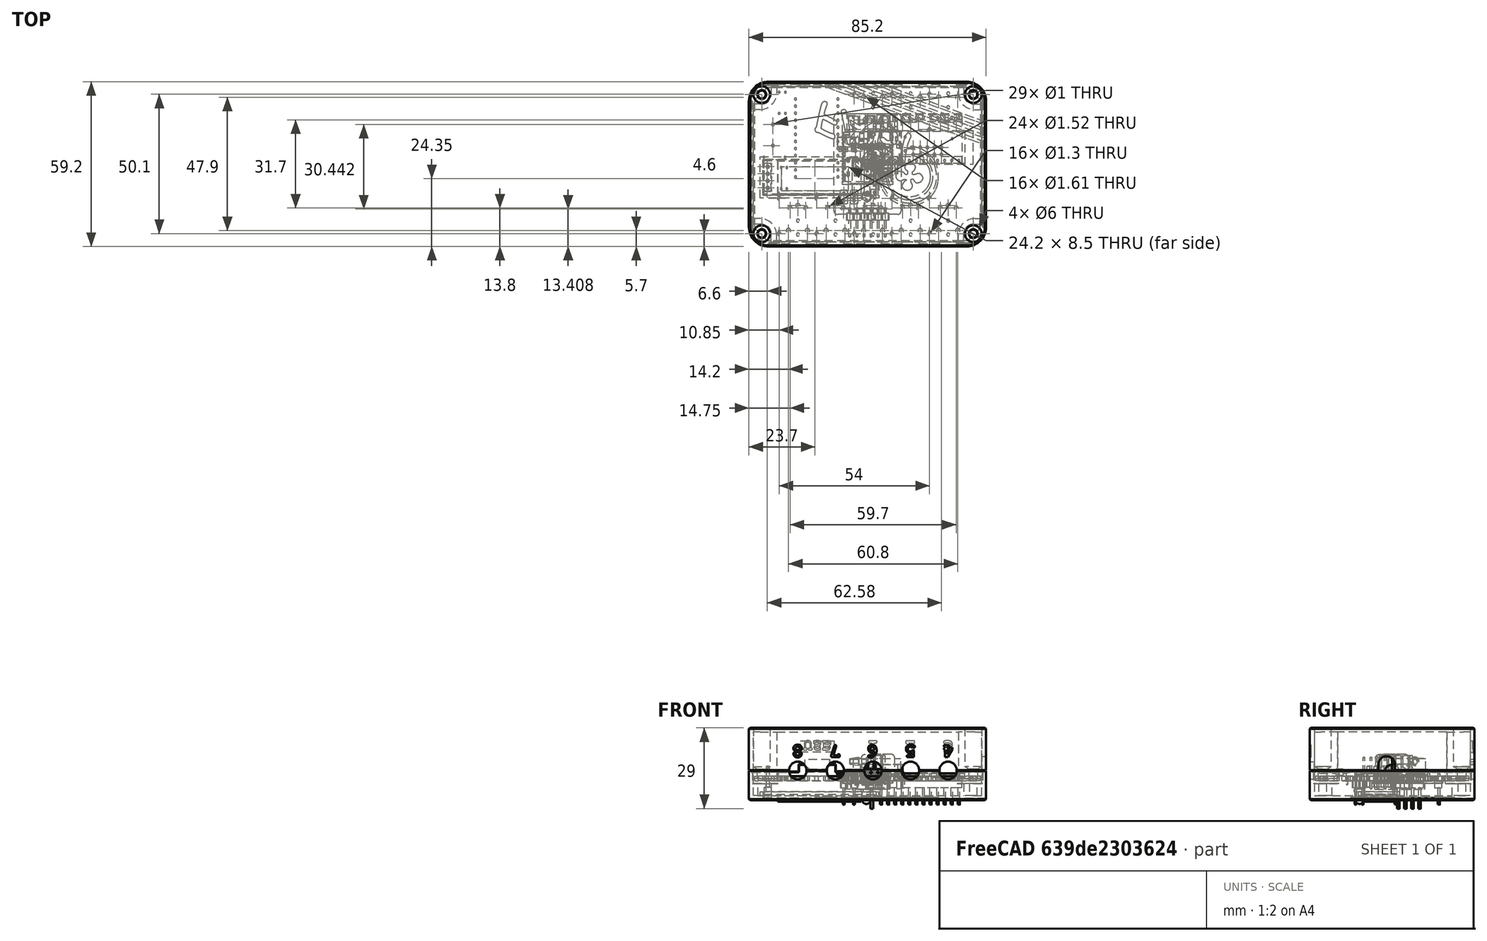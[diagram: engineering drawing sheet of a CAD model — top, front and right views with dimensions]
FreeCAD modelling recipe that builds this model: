
FCSTD DOCUMENT  (FreeCAD 0.18R4 (GitTag))
Label: FABIv3
License: All rights reserved
LicenseURL: http://en.wikipedia.org/wiki/All_rights_reserved
objects: Part::Feature×93, App::Part×90, Sketcher::SketchObject×32, PartDesign::Pocket×25, PartDesign::Mirrored×11, Mesh::Feature×7, PartDesign::Pad×5, PartDesign::MultiTransform×5, PartDesign::Plane×3, Part::Part2DObjectPython×3, PartDesign::Chamfer×2, PartDesign::Body×2, Part::FeaturePython×1, Part::Extrusion×1, PartDesign::Hole×1, PartDesign::LinearPattern×1, Part::Cut×1
note: 217 computed .brp shape members not serialized (recipe doc carries the construction recipe); baked Part::Feature solids carry a one-line shape summary decoded from their .brp

FEATURE [Part::Feature] Part__Feature086  label="SOLID080"
  Placement = pos=(-37.25,1.25,-4.85) rot=(1,0,0;3.14159rad)
  shape: bbox 38 x 12 x 12.6 mm, 32 faces (baked)
FEATURE [Part::Feature] Part__Feature176  label="SOLID162"
  shape: bbox 12.99 x 12.99 x 12.53 mm, 13 faces (baked)
FEATURE [App::Part] Buzzer_12x9_5RM7_6001  label="Buzzer_12x9.5RM7.007"
  Group = -> [Part__Feature176]
  Origin = -> Origin171
  Placement = pos=(-34.008,14.25,1.65) rot=(0,0,-1;1.5708rad)
FEATURE [Part::Feature] Part__Feature177  label="SOLID163"
  shape: bbox 15.1 x 7.1 x 8.8 mm, 33 faces (baked)
FEATURE [App::Part] JackPlug_FC68125031  label="JackPlug_FC68156"
  Group = -> [Part__Feature177]
  Origin = -> Origin172
  Placement = pos=(-1.5,27.4,2.15) rot=(0,0,-1;1.5708rad)
FEATURE [Part::Feature] Part__Feature178  label="SOLID164"
  shape: bbox 15.1 x 7.1 x 8.8 mm, 33 faces (baked)
FEATURE [App::Part] JackPlug_FC68125032  label="JackPlug_FC68157"
  Group = -> [Part__Feature178]
  Origin = -> Origin173
  Placement = pos=(12,27.4,2.15) rot=(0,0,-1;1.5708rad)
FEATURE [Part::Feature] Part__Feature179  label="SOLID165"
  shape: bbox 15.1 x 7.1 x 8.8 mm, 33 faces (baked)
FEATURE [App::Part] JackPlug_FC68125033  label="JackPlug_FC68158"
  Group = -> [Part__Feature179]
  Origin = -> Origin174
  Placement = pos=(25.5,27.4,2.15) rot=(0,0,-1;1.5708rad)
FEATURE [Part::Feature] Part__Feature180  label="SOLID166"
  shape: bbox 15.1 x 7.1 x 8.8 mm, 33 faces (baked)
FEATURE [App::Part] JackPlug_FC68125034  label="JackPlug_FC68159"
  Group = -> [Part__Feature180]
  Origin = -> Origin175
  Placement = pos=(32.5,-27.3,2.15) rot=(0,0,1;1.5708rad)
FEATURE [Part::Feature] Part__Feature181  label="SOLID167"
  shape: bbox 14.07 x 5.32 x 8.31 mm, 15 faces (baked)
FEATURE [App::Part] D_DO_201AE_P12_70mm_Horizontal031  label="D_DO-201AE_P12.70mm_Horizontal031"
  Group = -> [Part__Feature181]
  Origin = -> Origin176
  Placement = pos=(-4.75,25.1,1.65) rot=(0,0,-1;1.5708rad)
FEATURE [Part::Feature] Part__Feature182  label="SOLID168"
  shape: bbox 14.07 x 5.32 x 8.31 mm, 15 faces (baked)
FEATURE [App::Part] D_DO_201AE_P12_70mm_Horizontal032  label="D_DO-201AE_P12.70mm_Horizontal032"
  Group = -> [Part__Feature182]
  Origin = -> Origin177
  Placement = pos=(8.75,25.1,1.65) rot=(0,0,-1;1.5708rad)
FEATURE [Part::Feature] Part__Feature183  label="SOLID169"
  shape: bbox 14.07 x 5.32 x 8.31 mm, 15 faces (baked)
FEATURE [App::Part] D_DO_201AE_P12_70mm_Horizontal033  label="D_DO-201AE_P12.70mm_Horizontal033"
  Group = -> [Part__Feature183]
  Origin = -> Origin178
  Placement = pos=(22.25,25.1,1.65) rot=(0,0,-1;1.5708rad)
FEATURE [Part::Feature] Part__Feature184  label="SOLID170"
  shape: bbox 14.07 x 5.32 x 8.31 mm, 15 faces (baked)
FEATURE [App::Part] D_DO_201AE_P12_70mm_Horizontal034  label="D_DO-201AE_P12.70mm_Horizontal034"
  Group = -> [Part__Feature184]
  Origin = -> Origin179
  Placement = pos=(22.25,-25,1.65) rot=(0,0,1;1.5708rad)
FEATURE [Part::Feature] Part__Feature185  label="SOLID171"
  shape: bbox 15.1 x 7.1 x 8.8 mm, 33 faces (baked)
FEATURE [App::Part] JackPlug_FC68125035  label="JackPlug_FC68160"
  Group = -> [Part__Feature185]
  Origin = -> Origin180
  Placement = pos=(19,-27.3,2.15) rot=(0,0,1;1.5708rad)
FEATURE [Part::Feature] Part__Feature186  label="SOLID172"
  shape: bbox 15.1 x 7.1 x 8.8 mm, 33 faces (baked)
FEATURE [App::Part] JackPlug_FC68125036  label="JackPlug_FC68161"
  Group = -> [Part__Feature186]
  Origin = -> Origin181
  Placement = pos=(5.5,-27.3,2.15) rot=(0,0,1;1.5708rad)
FEATURE [Part::Feature] Part__Feature187  label="SOLID173"
  shape: bbox 15.1 x 7.1 x 8.8 mm, 33 faces (baked)
FEATURE [App::Part] JackPlug_FC68125037  label="JackPlug_FC68162"
  Group = -> [Part__Feature187]
  Origin = -> Origin182
  Placement = pos=(-8,-27.3,2.15) rot=(0,0,1;1.5708rad)
FEATURE [Part::Feature] Part__Feature188  label="SOLID174"
  shape: bbox 14.07 x 5.32 x 8.31 mm, 15 faces (baked)
FEATURE [App::Part] D_DO_201AE_P12_70mm_Horizontal035  label="D_DO-201AE_P12.70mm_Horizontal035"
  Group = -> [Part__Feature188]
  Origin = -> Origin183
  Placement = pos=(8.75,-25,1.65) rot=(0,0,1;1.5708rad)
FEATURE [Part::Feature] Part__Feature189  label="SOLID175"
  shape: bbox 14.07 x 5.32 x 8.31 mm, 15 faces (baked)
FEATURE [App::Part] D_DO_201AE_P12_70mm_Horizontal036  label="D_DO-201AE_P12.70mm_Horizontal036"
  Group = -> [Part__Feature189]
  Origin = -> Origin184
  Placement = pos=(-4.75,-25,1.65) rot=(0,0,1;1.5708rad)
FEATURE [Part::Feature] Part__Feature190  label="SOLID176"
  shape: bbox 14.07 x 5.32 x 8.31 mm, 15 faces (baked)
FEATURE [App::Part] D_DO_201AE_P12_70mm_Horizontal037  label="D_DO-201AE_P12.70mm_Horizontal037"
  Group = -> [Part__Feature190]
  Origin = -> Origin185
  Placement = pos=(-18.25,-25,1.65) rot=(0,0,1;1.5708rad)
FEATURE [Part::Feature] Part__Feature191  label="SOLID177"
  shape: bbox 15.1 x 7.1 x 8.8 mm, 33 faces (baked)
FEATURE [App::Part] JackPlug_FC68125038  label="JackPlug_FC68163"
  Group = -> [Part__Feature191]
  Origin = -> Origin186
  Placement = pos=(-21.5,-27.3,2.15) rot=(0,0,1;1.5708rad)
FEATURE [Part::Feature] Part__Feature192  label="SOLID178"
  shape: bbox 8.285 x 1.732 x 4.666 mm, 17 faces (baked)
FEATURE [App::Part] R_Axial_DIN0204_L3_6mm_D1_6mm_P7_62mm_Horizontal028  label="R_Axial_DIN0204_L3.6mm_D1.6mm_P7.62mm_Horizontal028"
  Group = -> [Part__Feature192]
  Origin = -> Origin187
  Placement = pos=(-8.1,-1.4,1.65) rot=(0,0,1;0rad)
FEATURE [Part::Feature] Part__Feature193  label="SOLID179"
  shape: bbox 8.285 x 1.732 x 4.666 mm, 17 faces (baked)
FEATURE [App::Part] R_Axial_DIN0204_L3_6mm_D1_6mm_P7_62mm_Horizontal029  label="R_Axial_DIN0204_L3.6mm_D1.6mm_P7.62mm_Horizontal029"
  Group = -> [Part__Feature193]
  Origin = -> Origin188
  Placement = pos=(-8.1,-4,1.65) rot=(0,0,1;0rad)
FEATURE [Part::Feature] Part__Feature194  label="SOLID180"
  shape: bbox 8.285 x 1.732 x 4.666 mm, 17 faces (baked)
FEATURE [App::Part] R_Axial_DIN0204_L3_6mm_D1_6mm_P7_62mm_Horizontal030  label="R_Axial_DIN0204_L3.6mm_D1.6mm_P7.62mm_Horizontal030"
  Group = -> [Part__Feature194]
  Origin = -> Origin189
  Placement = pos=(30.4,1.5,1.65) rot=(0,0,1;1.5708rad)
FEATURE [Part::Feature] Part__Feature195  label="SOLID181"
  shape: bbox 2 x 1.2 x 0.45 mm, 26 faces (baked)
FEATURE [App::Part] R_0805_2012Metric028
  Group = -> [Part__Feature195]
  Origin = -> Origin190
  Placement = pos=(30.4,5.35,1.65) rot=(0,0,1;1.5708rad)
FEATURE [Part::Feature] Part__Feature196  label="SOLID182"
  shape: bbox 35.2 x 18 x 12.54 mm, 122 faces (baked)
FEATURE [App::Part] ProMicro003
  Group = -> [Part__Feature196]
  Origin = -> Origin191
  Placement = pos=(-27.25,28.25,4.65) rot=(0,0,-1;1.5708rad)
FEATURE [Part::Feature] Part__Feature197  label="SOLID183"
  shape: bbox 2.8 x 2.9 x 1.55 mm, 109 faces (baked)
FEATURE [App::Part] SOT_23_5007  label="SOT-23-012"
  Group = -> [Part__Feature197]
  Origin = -> Origin192
  Placement = pos=(-14.2,-0.7,1.65) rot=(0,0,1;0rad)
FEATURE [Part::Feature] Part__Feature198  label="SOLID184"
  shape: bbox 38 x 12 x 12.6 mm, 32 faces (baked)
FEATURE [App::Part] OLED092_display002
  Group = -> [Part__Feature198]
  Origin = -> Origin193
  Placement = pos=(-37.5,1.25,-2.85) rot=(1,0,0;3.14159rad)
FEATURE [Part::Feature] Part__Feature199  label="COMPOUND013"
  shape: bbox 10.08 x 3.946 x 9.8 mm, 102 faces, 25 solids (baked)
FEATURE [App::Part] _1601_304LF003  label="91601-304LF003"
  Group = -> [Part__Feature199]
  Origin = -> Origin194
  Placement = pos=(-36,-4.75,1.65) rot=(0,0,-1;1.5708rad)
FEATURE [Part::Feature] Part__Feature200  label="SOLID185"
  shape: bbox 18.35 x 12 x 8.506 mm, 25 faces (baked)
FEATURE [Part::Feature] Part__Feature201  label="COMPOUND014"
  shape: bbox 8.62 x 19 x 4 mm, 48 faces, 8 solids (baked)
FEATURE [App::Part] mp003
  Group = -> [Part__Feature200,Part__Feature201]
  Origin = -> Origin195
  Placement = pos=(12.5,6,1.65) rot=(0,0,1;3.14159rad)
FEATURE [Part::Feature] Part__Feature202  label="COMPOUND015"
  shape: bbox 24.13 x 44.38 x 17.54 mm, 1943 faces, 18 solids (baked)
FEATURE [App::Part] esp32miniBT002
  Group = -> [Part__Feature202]
  Origin = -> Origin196
  Placement = pos=(20.52,0.92,14.15) rot=(0.707107,0.707107,0;3.14159rad)
FEATURE [Part::Feature] Part__Feature203  label="SOLID186"
  shape: bbox 2 x 1.2 x 0.45 mm, 26 faces (baked)
FEATURE [App::Part] R_0805_2012Metric029
  Group = -> [Part__Feature203]
  Origin = -> Origin197
  Placement = pos=(-29.5,22,1.65) rot=(0,0,-1;1.5708rad)
FEATURE [Part::Feature] Part__Feature204  label="SOLID187"
  shape: bbox 2 x 1.2 x 0.45 mm, 26 faces (baked)
FEATURE [App::Part] R_0805_2012Metric030
  Group = -> [Part__Feature204]
  Origin = -> Origin198
  Placement = pos=(-31.75,22,1.65) rot=(0,0,1;1.5708rad)
FEATURE [Part::Feature] Part__Feature205  label="SOLID188"
  shape: bbox 8.285 x 1.732 x 4.666 mm, 17 faces (baked)
FEATURE [App::Part] R_Axial_DIN0204_L3_6mm_D1_6mm_P7_62mm_Horizontal031  label="R_Axial_DIN0204_L3.6mm_D1.6mm_P7.62mm_Horizontal031"
  Group = -> [Part__Feature205]
  Origin = -> Origin199
  Placement = pos=(-31,-1.25,1.65) rot=(0,0,-1;1.5708rad)
FEATURE [Part::Feature] Part__Feature206  label="SOLID189"
  shape: bbox 5.08 x 12.7 x 11.54 mm, 214 faces (baked)
FEATURE [App::Part] PinHeader_2x05_P2_54mm_Vertical003  label="PinHeader_2x05_P2.54mm_Vertical003"
  Group = -> [Part__Feature206]
  Origin = -> Origin200
  Placement = pos=(16.42,3.46,1.65) rot=(0,0,1;1.5708rad)
FEATURE [Part::Feature] Part__Feature207  label="SOLID190"
  shape: bbox 2.54 x 7.62 x 11.54 mm, 76 faces (baked)
FEATURE [App::Part] PinHeader_1x03_P2_54mm_Vertical003  label="PinHeader_1x03_P2.54mm_Vertical003"
  Group = -> [Part__Feature207]
  Origin = -> Origin201
  Placement = pos=(-4.3,7.3,1.65) rot=(0,0,1;0rad)
FEATURE [Part::Feature] Part__Feature208  label="SOLID191"
  shape: bbox 8.285 x 1.732 x 4.666 mm, 17 faces (baked)
FEATURE [App::Part] R_Axial_DIN0204_L3_6mm_D1_6mm_P7_62mm_Horizontal032  label="R_Axial_DIN0204_L3.6mm_D1.6mm_P7.62mm_Horizontal032"
  Group = -> [Part__Feature208]
  Origin = -> Origin202
  Placement = pos=(-29,-1.25,1.65) rot=(0,0,-1;1.5708rad)
FEATURE [Part::Feature] Part__Feature209  label="SOLID192"
  shape: bbox 2 x 1.2 x 0.45 mm, 26 faces (baked)
FEATURE [App::Part] R_0805_2012Metric031
  Group = -> [Part__Feature209]
  Origin = -> Origin203
  Placement = pos=(-4.3,-4,1.65) rot=(0,0,1;0rad)
FEATURE [Part::Feature] Part__Feature210  label="SOLID193"
  shape: bbox 2 x 1.2 x 0.45 mm, 26 faces (baked)
FEATURE [App::Part] R_0805_2012Metric032
  Group = -> [Part__Feature210]
  Origin = -> Origin204
  Placement = pos=(-4.3,-1.4,1.65) rot=(0,0,1;0rad)
FEATURE [Part::Feature] Part__Feature211  label="SOLID194"
  shape: bbox 2 x 1.2 x 0.45 mm, 26 faces (baked)
FEATURE [App::Part] R_0805_2012Metric033
  Group = -> [Part__Feature211]
  Origin = -> Origin205
  Placement = pos=(-33.5,2.5,1.65) rot=(0,0,1;0rad)
FEATURE [Part::Feature] Part__Feature212  label="SOLID195"
  shape: bbox 2 x 1.2 x 0.45 mm, 26 faces (baked)
FEATURE [App::Part] R_0805_2012Metric034
  Group = -> [Part__Feature212]
  Origin = -> Origin206
  Placement = pos=(-30,-6,1.65) rot=(0,0,1;0rad)
FEATURE [Part::Feature] Part__Feature213  label="SOLID196"
  shape: bbox 2 x 1.2 x 0.45 mm, 26 faces (baked)
FEATURE [App::Part] R_0805_2012Metric035
  Group = -> [Part__Feature213]
  Origin = -> Origin207
  Placement = pos=(-30,-4,1.65) rot=(0,0,1;0rad)
FEATURE [Part::Feature] Part__Feature214  label="SOLID197"
  shape: bbox 2 x 1.25 x 1.25 mm, 28 faces (baked)
FEATURE [App::Part] C_0805_2012Metric003
  Group = -> [Part__Feature214]
  Origin = -> Origin208
  Placement = pos=(6,10.7,1.65) rot=(0,0,1;3.14159rad)
FEATURE [Part::Feature] Part__Feature215  label="SOLID198"
  shape: bbox 5.5 x 2.5 x 7.1 mm, 10 faces (baked)
FEATURE [App::Part] C_Disc_D5_0mm_W2_5mm_P5_00mm003  label="C_Disc_D5.0mm_W2.5mm_P5.00mm003"
  Group = -> [Part__Feature215]
  Origin = -> Origin209
  Placement = pos=(13.5,9.75,1.65) rot=(0,0,-1;1.5708rad)
FEATURE [Part::Feature] Part__Feature216  label="SOLID199"
  shape: bbox 14.07 x 5.32 x 8.31 mm, 15 faces (baked)
FEATURE [App::Part] D_DO_201AE_P12_70mm_Horizontal038  label="D_DO-201AE_P12.70mm_Horizontal038"
  Group = -> [Part__Feature216]
  Origin = -> Origin210
  Placement = pos=(-31.75,-25,1.65) rot=(0,0,1;1.5708rad)
FEATURE [Part::Feature] Part__Feature217  label="SOLID200"
  shape: bbox 8.285 x 1.732 x 4.666 mm, 17 faces (baked)
FEATURE [App::Part] R_Axial_DIN0204_L3_6mm_D1_6mm_P7_62mm_Horizontal033  label="R_Axial_DIN0204_L3.6mm_D1.6mm_P7.62mm_Horizontal033"
  Group = -> [Part__Feature217]
  Origin = -> Origin211
  Placement = pos=(-37.25,2.5,1.65) rot=(0,0,1;0rad)
FEATURE [Part::Feature] Part__Feature218  label="SOLID201"
  shape: bbox 8.285 x 1.732 x 4.666 mm, 17 faces (baked)
FEATURE [App::Part] R_Axial_DIN0204_L3_6mm_D1_6mm_P7_62mm_Horizontal034  label="R_Axial_DIN0204_L3.6mm_D1.6mm_P7.62mm_Horizontal034"
  Group = -> [Part__Feature218]
  Origin = -> Origin212
  Placement = pos=(-29.5,25.87,1.65) rot=(0,0,-1;1.5708rad)
FEATURE [Part::Feature] Part__Feature219  label="SOLID202"
  shape: bbox 8.285 x 1.732 x 4.666 mm, 17 faces (baked)
FEATURE [App::Part] R_Axial_DIN0204_L3_6mm_D1_6mm_P7_62mm_Horizontal035  label="R_Axial_DIN0204_L3.6mm_D1.6mm_P7.62mm_Horizontal035"
  Group = -> [Part__Feature219]
  Origin = -> Origin213
  Placement = pos=(-31.75,18.25,1.65) rot=(0,0,1;1.5708rad)
FEATURE [Part::Feature] Part__Feature220  label="SOLID203"
  shape: bbox 2.8 x 2.9 x 1.55 mm, 109 faces (baked)
FEATURE [App::Part] SOT_23_5008  label="SOT-23-013"
  Group = -> [Part__Feature220]
  Origin = -> Origin214
  Placement = pos=(-19.5,-8.7,1.65) rot=(0,0,1;1.5708rad)
FEATURE [Part::Feature] Part__Feature221  label="COMPOUND016"
  shape: bbox 81 x 55 x 1.6 mm, 174 faces (baked)
FEATURE [App::Part] Open_CASCADE_STEP_translator_6_9_1003  label="FABI_PCB001"
  Group = -> [Buzzer_12x9_5RM7_6001,JackPlug_FC68125031,JackPlug_FC68125032,JackPlug_FC68125033,JackPlug_FC68125034,D_DO_201AE_P12_70mm_Horizontal031,D_DO_201AE_P12_70mm_Horizontal032,D_DO_201AE_P12_70mm_Horizontal033,D_DO_201AE_P12_70mm_Horizontal034,JackPlug_FC68125035,JackPlug_FC68125036,JackPlug_FC68125037,D_DO_201AE_P12_70mm_Horizontal035,D_DO_201AE_P12_70mm_Horizontal036,D_DO_201AE_P12_70mm_Horizontal037,+30 more]
  Origin = -> Origin215
  Placement = pos=(0,0,-1.6) rot=(0,0,1;0rad)
FEATURE [Part::Feature] Part__Feature222  label="SOLID204"
  shape: bbox 12.99 x 12.99 x 12.53 mm, 13 faces (baked)
FEATURE [App::Part] Buzzer_12x9_5RM7_6002  label="Buzzer_12x9.5RM7.008"
  Group = -> [Part__Feature222]
  Origin = -> Origin216
  Placement = pos=(-34.008,14.25,1.65) rot=(0,0,-1;1.5708rad)
FEATURE [Part::Feature] Part__Feature223  label="SOLID205"
  shape: bbox 15.1 x 7.1 x 8.8 mm, 33 faces (baked)
FEATURE [App::Part] JackPlug_FC68125039  label="JackPlug_FC68164"
  Group = -> [Part__Feature223]
  Origin = -> Origin217
  Placement = pos=(-1.55,27.4,2.15) rot=(0,0,-1;1.5708rad)
FEATURE [Part::Feature] Part__Feature224  label="SOLID206"
  shape: bbox 15.1 x 7.1 x 8.8 mm, 33 faces (baked)
FEATURE [App::Part] JackPlug_FC68125040  label="JackPlug_FC68165"
  Group = -> [Part__Feature224]
  Origin = -> Origin218
  Placement = pos=(11.95,27.4,2.15) rot=(0,0,-1;1.5708rad)
FEATURE [Part::Feature] Part__Feature225  label="SOLID207"
  shape: bbox 15.1 x 7.1 x 8.8 mm, 33 faces (baked)
FEATURE [App::Part] JackPlug_FC68125041  label="JackPlug_FC68166"
  Group = -> [Part__Feature225]
  Origin = -> Origin219
  Placement = pos=(25.45,27.4,2.15) rot=(0,0,-1;1.5708rad)
FEATURE [Part::Feature] Part__Feature226  label="SOLID208"
  shape: bbox 15.1 x 7.1 x 8.8 mm, 33 faces (baked)
FEATURE [App::Part] JackPlug_FC68125042  label="JackPlug_FC68167"
  Group = -> [Part__Feature226]
  Origin = -> Origin220
  Placement = pos=(32.55,-27.3,2.15) rot=(0,0,1;1.5708rad)
FEATURE [Part::Feature] Part__Feature227  label="SOLID209"
  shape: bbox 14.07 x 5.32 x 8.31 mm, 15 faces (baked)
FEATURE [App::Part] D_DO_201AE_P12_70mm_Horizontal039  label="D_DO-201AE_P12.70mm_Horizontal039"
  Group = -> [Part__Feature227]
  Origin = -> Origin221
  Placement = pos=(-4.75,25.1,1.65) rot=(0,0,-1;1.5708rad)
FEATURE [Part::Feature] Part__Feature228  label="SOLID210"
  shape: bbox 14.07 x 5.32 x 8.31 mm, 15 faces (baked)
FEATURE [App::Part] D_DO_201AE_P12_70mm_Horizontal040  label="D_DO-201AE_P12.70mm_Horizontal040"
  Group = -> [Part__Feature228]
  Origin = -> Origin222
  Placement = pos=(8.75,25.1,1.65) rot=(0,0,-1;1.5708rad)
FEATURE [Part::Feature] Part__Feature229  label="SOLID211"
  shape: bbox 14.07 x 5.32 x 8.31 mm, 15 faces (baked)
FEATURE [App::Part] D_DO_201AE_P12_70mm_Horizontal041  label="D_DO-201AE_P12.70mm_Horizontal041"
  Group = -> [Part__Feature229]
  Origin = -> Origin223
  Placement = pos=(22.25,25.1,1.65) rot=(0,0,-1;1.5708rad)
FEATURE [Part::Feature] Part__Feature230  label="SOLID212"
  shape: bbox 14.07 x 5.32 x 8.31 mm, 15 faces (baked)
FEATURE [App::Part] D_DO_201AE_P12_70mm_Horizontal042  label="D_DO-201AE_P12.70mm_Horizontal042"
  Group = -> [Part__Feature230]
  Origin = -> Origin224
  Placement = pos=(22.25,-25,1.65) rot=(0,0,1;1.5708rad)
FEATURE [Part::Feature] Part__Feature231  label="SOLID213"
  shape: bbox 15.1 x 7.1 x 8.8 mm, 33 faces (baked)
FEATURE [App::Part] JackPlug_FC68125043  label="JackPlug_FC68168"
  Group = -> [Part__Feature231]
  Origin = -> Origin225
  Placement = pos=(19.05,-27.3,2.15) rot=(0,0,1;1.5708rad)
FEATURE [Part::Feature] Part__Feature232  label="SOLID214"
  shape: bbox 15.1 x 7.1 x 8.8 mm, 33 faces (baked)
FEATURE [App::Part] JackPlug_FC68125044  label="JackPlug_FC68169"
  Group = -> [Part__Feature232]
  Origin = -> Origin226
  Placement = pos=(5.55,-27.3,2.15) rot=(0,0,1;1.5708rad)
FEATURE [Part::Feature] Part__Feature233  label="SOLID215"
  shape: bbox 15.1 x 7.1 x 8.8 mm, 33 faces (baked)
FEATURE [App::Part] JackPlug_FC68125045  label="JackPlug_FC68170"
  Group = -> [Part__Feature233]
  Origin = -> Origin227
  Placement = pos=(-7.95,-27.3,2.15) rot=(0,0,1;1.5708rad)
FEATURE [Part::Feature] Part__Feature234  label="SOLID216"
  shape: bbox 14.07 x 5.32 x 8.31 mm, 15 faces (baked)
FEATURE [App::Part] D_DO_201AE_P12_70mm_Horizontal043  label="D_DO-201AE_P12.70mm_Horizontal043"
  Group = -> [Part__Feature234]
  Origin = -> Origin228
  Placement = pos=(8.75,-25,1.65) rot=(0,0,1;1.5708rad)
FEATURE [Part::Feature] Part__Feature235  label="SOLID217"
  shape: bbox 14.07 x 5.32 x 8.31 mm, 15 faces (baked)
FEATURE [App::Part] D_DO_201AE_P12_70mm_Horizontal044  label="D_DO-201AE_P12.70mm_Horizontal044"
  Group = -> [Part__Feature235]
  Origin = -> Origin229
  Placement = pos=(-4.75,-25,1.65) rot=(0,0,1;1.5708rad)
FEATURE [Part::Feature] Part__Feature236  label="SOLID218"
  shape: bbox 14.07 x 5.32 x 8.31 mm, 15 faces (baked)
FEATURE [App::Part] D_DO_201AE_P12_70mm_Horizontal045  label="D_DO-201AE_P12.70mm_Horizontal045"
  Group = -> [Part__Feature236]
  Origin = -> Origin230
  Placement = pos=(-18.25,-25,1.65) rot=(0,0,1;1.5708rad)
FEATURE [Part::Feature] Part__Feature237  label="SOLID219"
  shape: bbox 15.1 x 7.1 x 8.8 mm, 33 faces (baked)
FEATURE [App::Part] JackPlug_FC68125046  label="JackPlug_FC68171"
  Group = -> [Part__Feature237]
  Origin = -> Origin231
  Placement = pos=(-21.45,-27.3,2.15) rot=(0,0,1;1.5708rad)
FEATURE [Part::Feature] Part__Feature238  label="SOLID220"
  shape: bbox 8.285 x 1.732 x 4.666 mm, 17 faces (baked)
FEATURE [App::Part] R_Axial_DIN0204_L3_6mm_D1_6mm_P7_62mm_Horizontal036  label="R_Axial_DIN0204_L3.6mm_D1.6mm_P7.62mm_Horizontal036"
  Group = -> [Part__Feature238]
  Origin = -> Origin232
  Placement = pos=(-8.1,-1.4,1.65) rot=(0,0,1;0rad)
FEATURE [Part::Feature] Part__Feature239  label="SOLID221"
  shape: bbox 8.285 x 1.732 x 4.666 mm, 17 faces (baked)
FEATURE [App::Part] R_Axial_DIN0204_L3_6mm_D1_6mm_P7_62mm_Horizontal037  label="R_Axial_DIN0204_L3.6mm_D1.6mm_P7.62mm_Horizontal037"
  Group = -> [Part__Feature239]
  Origin = -> Origin233
  Placement = pos=(-8.1,-4,1.65) rot=(0,0,1;0rad)
FEATURE [Part::Feature] Part__Feature240  label="SOLID222"
  shape: bbox 8.285 x 1.732 x 4.666 mm, 17 faces (baked)
FEATURE [App::Part] R_Axial_DIN0204_L3_6mm_D1_6mm_P7_62mm_Horizontal038  label="R_Axial_DIN0204_L3.6mm_D1.6mm_P7.62mm_Horizontal038"
  Group = -> [Part__Feature240]
  Origin = -> Origin234
  Placement = pos=(30.4,1.5,1.65) rot=(0,0,1;1.5708rad)
FEATURE [Part::Feature] Part__Feature241  label="SOLID223"
  shape: bbox 2 x 1.2 x 0.45 mm, 26 faces (baked)
FEATURE [App::Part] R_0805_2012Metric036
  Group = -> [Part__Feature241]
  Origin = -> Origin235
  Placement = pos=(30.4,5.35,1.65) rot=(0,0,1;1.5708rad)
FEATURE [Part::Feature] Part__Feature242  label="SOLID224"
  shape: bbox 35.2 x 18 x 12.54 mm, 122 faces (baked)
FEATURE [App::Part] ProMicro004
  Group = -> [Part__Feature242]
  Origin = -> Origin236
  Placement = pos=(-27.25,28.25,4.65) rot=(0,0,-1;1.5708rad)
FEATURE [Part::Feature] Part__Feature243  label="SOLID225"
  shape: bbox 2.8 x 2.9 x 1.55 mm, 109 faces (baked)
FEATURE [App::Part] SOT_23_5009  label="SOT-23-014"
  Group = -> [Part__Feature243]
  Origin = -> Origin237
  Placement = pos=(-14.2,-0.7,1.65) rot=(0,0,1;0rad)
FEATURE [Part::Feature] Part__Feature244  label="SOLID226"
  shape: bbox 38 x 12 x 12.6 mm, 32 faces (baked)
FEATURE [App::Part] OLED092_display003
  Group = -> [Part__Feature244]
  Origin = -> Origin238
  Placement = pos=(-37.5,1.25,-2.85) rot=(1,0,0;3.14159rad)
FEATURE [Part::Feature] Part__Feature245  label="COMPOUND017"
  shape: bbox 10.08 x 3.946 x 9.8 mm, 102 faces, 25 solids (baked)
FEATURE [App::Part] _1601_304LF004  label="91601-304LF004"
  Group = -> [Part__Feature245]
  Origin = -> Origin239
  Placement = pos=(-36,-4.75,1.65) rot=(0,0,-1;1.5708rad)
FEATURE [Part::Feature] Part__Feature246  label="SOLID227"
  shape: bbox 18.35 x 12 x 8.506 mm, 25 faces (baked)
FEATURE [Part::Feature] Part__Feature247  label="COMPOUND018"
  shape: bbox 8.62 x 19 x 4 mm, 48 faces, 8 solids (baked)
FEATURE [App::Part] mp004
  Group = -> [Part__Feature246,Part__Feature247]
  Origin = -> Origin240
  Placement = pos=(12.5,6,1.65) rot=(0,0,1;3.14159rad)
FEATURE [Part::Feature] Part__Feature248  label="COMPOUND019"
  shape: bbox 24.13 x 44.38 x 17.54 mm, 1943 faces, 18 solids (baked)
FEATURE [App::Part] esp32miniBT
  Group = -> [Part__Feature248]
  Origin = -> Origin241
  Placement = pos=(20.52,0.92,14.15) rot=(0.707107,0.707107,0;3.14159rad)
FEATURE [Part::Feature] Part__Feature249  label="SOLID228"
  shape: bbox 2 x 1.2 x 0.45 mm, 26 faces (baked)
FEATURE [App::Part] R_0805_2012Metric037
  Group = -> [Part__Feature249]
  Origin = -> Origin242
  Placement = pos=(-29.5,22,1.65) rot=(0,0,-1;1.5708rad)
FEATURE [Part::Feature] Part__Feature250  label="SOLID229"
  shape: bbox 2 x 1.2 x 0.45 mm, 26 faces (baked)
FEATURE [App::Part] R_0805_2012Metric038
  Group = -> [Part__Feature250]
  Origin = -> Origin243
  Placement = pos=(-31.75,22,1.65) rot=(0,0,1;1.5708rad)
FEATURE [Part::Feature] Part__Feature251  label="SOLID230"
  shape: bbox 8.285 x 1.732 x 4.666 mm, 17 faces (baked)
FEATURE [App::Part] R_Axial_DIN0204_L3_6mm_D1_6mm_P7_62mm_Horizontal039  label="R_Axial_DIN0204_L3.6mm_D1.6mm_P7.62mm_Horizontal039"
  Group = -> [Part__Feature251]
  Origin = -> Origin244
  Placement = pos=(-31,-1.25,1.65) rot=(0,0,-1;1.5708rad)
FEATURE [Part::Feature] Part__Feature252  label="SOLID231"
  shape: bbox 5.08 x 12.7 x 11.54 mm, 214 faces (baked)
FEATURE [App::Part] PinHeader_2x05_P2_54mm_Vertical004  label="PinHeader_2x05_P2.54mm_Vertical004"
  Group = -> [Part__Feature252]
  Origin = -> Origin245
  Placement = pos=(16.42,3.46,1.65) rot=(0,0,1;1.5708rad)
FEATURE [Part::Feature] Part__Feature253  label="SOLID232"
  shape: bbox 2.54 x 7.62 x 11.54 mm, 76 faces (baked)
FEATURE [App::Part] PinHeader_1x03_P2_54mm_Vertical004  label="PinHeader_1x03_P2.54mm_Vertical004"
  Group = -> [Part__Feature253]
  Origin = -> Origin246
  Placement = pos=(-4.3,7.3,1.65) rot=(0,0,1;0rad)
FEATURE [Part::Feature] Part__Feature254  label="SOLID233"
  shape: bbox 8.285 x 1.732 x 4.666 mm, 17 faces (baked)
FEATURE [App::Part] R_Axial_DIN0204_L3_6mm_D1_6mm_P7_62mm_Horizontal040  label="R_Axial_DIN0204_L3.6mm_D1.6mm_P7.62mm_Horizontal040"
  Group = -> [Part__Feature254]
  Origin = -> Origin247
  Placement = pos=(-29,-1.25,1.65) rot=(0,0,-1;1.5708rad)
FEATURE [Part::Feature] Part__Feature255  label="SOLID234"
  shape: bbox 2 x 1.2 x 0.45 mm, 26 faces (baked)
FEATURE [App::Part] R_0805_2012Metric039
  Group = -> [Part__Feature255]
  Origin = -> Origin248
  Placement = pos=(-4.3,-4,1.65) rot=(0,0,1;0rad)
FEATURE [Part::Feature] Part__Feature256  label="SOLID235"
  shape: bbox 2 x 1.2 x 0.45 mm, 26 faces (baked)
FEATURE [App::Part] R_0805_2012Metric040
  Group = -> [Part__Feature256]
  Origin = -> Origin249
  Placement = pos=(-4.3,-1.4,1.65) rot=(0,0,1;0rad)
FEATURE [Part::Feature] Part__Feature257  label="SOLID236"
  shape: bbox 2 x 1.2 x 0.45 mm, 26 faces (baked)
FEATURE [App::Part] R_0805_2012Metric041
  Group = -> [Part__Feature257]
  Origin = -> Origin250
  Placement = pos=(-33.5,2.5,1.65) rot=(0,0,1;0rad)
FEATURE [Part::Feature] Part__Feature258  label="SOLID237"
  shape: bbox 2 x 1.2 x 0.45 mm, 26 faces (baked)
FEATURE [App::Part] R_0805_2012Metric042
  Group = -> [Part__Feature258]
  Origin = -> Origin251
  Placement = pos=(-30,-6,1.65) rot=(0,0,1;0rad)
FEATURE [Part::Feature] Part__Feature259  label="SOLID238"
  shape: bbox 2 x 1.2 x 0.45 mm, 26 faces (baked)
FEATURE [App::Part] R_0805_2012Metric043
  Group = -> [Part__Feature259]
  Origin = -> Origin252
  Placement = pos=(-30,-4,1.65) rot=(0,0,1;0rad)
FEATURE [Part::Feature] Part__Feature260  label="SOLID239"
  shape: bbox 2 x 1.25 x 1.25 mm, 28 faces (baked)
FEATURE [App::Part] C_0805_2012Metric004
  Group = -> [Part__Feature260]
  Origin = -> Origin253
  Placement = pos=(6,10.7,1.65) rot=(0,0,1;3.14159rad)
FEATURE [Part::Feature] Part__Feature261  label="SOLID240"
  shape: bbox 5.5 x 2.5 x 7.1 mm, 10 faces (baked)
FEATURE [App::Part] C_Disc_D5_0mm_W2_5mm_P5_00mm004  label="C_Disc_D5.0mm_W2.5mm_P5.00mm004"
  Group = -> [Part__Feature261]
  Origin = -> Origin254
  Placement = pos=(13.5,9.75,1.65) rot=(0,0,-1;1.5708rad)
FEATURE [Part::Feature] Part__Feature262  label="SOLID241"
  shape: bbox 14.07 x 5.32 x 8.31 mm, 15 faces (baked)
FEATURE [App::Part] D_DO_201AE_P12_70mm_Horizontal046  label="D_DO-201AE_P12.70mm_Horizontal046"
  Group = -> [Part__Feature262]
  Origin = -> Origin255
  Placement = pos=(-31.75,-25,1.65) rot=(0,0,1;1.5708rad)
FEATURE [Part::Feature] Part__Feature263  label="SOLID242"
  shape: bbox 8.285 x 1.732 x 4.666 mm, 17 faces (baked)
FEATURE [App::Part] R_Axial_DIN0204_L3_6mm_D1_6mm_P7_62mm_Horizontal041  label="R_Axial_DIN0204_L3.6mm_D1.6mm_P7.62mm_Horizontal041"
  Group = -> [Part__Feature263]
  Origin = -> Origin256
  Placement = pos=(-37.25,2.5,1.65) rot=(0,0,1;0rad)
FEATURE [Part::Feature] Part__Feature264  label="SOLID243"
  shape: bbox 8.285 x 1.732 x 4.666 mm, 17 faces (baked)
FEATURE [App::Part] R_Axial_DIN0204_L3_6mm_D1_6mm_P7_62mm_Horizontal042  label="R_Axial_DIN0204_L3.6mm_D1.6mm_P7.62mm_Horizontal042"
  Group = -> [Part__Feature264]
  Origin = -> Origin257
  Placement = pos=(-29.5,25.87,1.65) rot=(0,0,-1;1.5708rad)
FEATURE [Part::Feature] Part__Feature265  label="SOLID244"
  shape: bbox 8.285 x 1.732 x 4.666 mm, 17 faces (baked)
FEATURE [App::Part] R_Axial_DIN0204_L3_6mm_D1_6mm_P7_62mm_Horizontal043  label="R_Axial_DIN0204_L3.6mm_D1.6mm_P7.62mm_Horizontal043"
  Group = -> [Part__Feature265]
  Origin = -> Origin258
  Placement = pos=(-31.75,18.25,1.65) rot=(0,0,1;1.5708rad)
FEATURE [Part::Feature] Part__Feature266  label="SOLID245"
  shape: bbox 2.8 x 2.9 x 1.55 mm, 109 faces (baked)
FEATURE [App::Part] SOT_23_5010  label="SOT-23-015"
  Group = -> [Part__Feature266]
  Origin = -> Origin259
  Placement = pos=(-19.5,-8.7,1.65) rot=(0,0,1;1.5708rad)
FEATURE [Part::Feature] Part__Feature267  label="COMPOUND020"
  shape: bbox 81 x 55 x 1.6 mm, 174 faces (baked)
FEATURE [App::Part] Open_CASCADE_STEP_translator_6_9_1004  label="Open CASCADE STEP translator 6.9 002"
  Group = -> [Buzzer_12x9_5RM7_6002,JackPlug_FC68125039,JackPlug_FC68125040,JackPlug_FC68125041,JackPlug_FC68125042,D_DO_201AE_P12_70mm_Horizontal039,D_DO_201AE_P12_70mm_Horizontal040,D_DO_201AE_P12_70mm_Horizontal041,D_DO_201AE_P12_70mm_Horizontal042,JackPlug_FC68125043,JackPlug_FC68125044,JackPlug_FC68125045,D_DO_201AE_P12_70mm_Horizontal043,D_DO_201AE_P12_70mm_Horizontal044,D_DO_201AE_P12_70mm_Horizontal045,+30 more]
  Origin = -> Origin260
  Placement = pos=(0,0,-1.6) rot=(0,0,1;0rad)
FEATURE [Sketcher::SketchObject] CopySketch014  label="Base"
  sketch-geometry (12):
    g0: LineSegment StartX=-35.5 StartY=29.5 StartZ=0 EndX=35.5 EndY=29.5 EndZ=0
    g1: LineSegment StartX=42.5 StartY=22.5 StartZ=0 EndX=42.5 EndY=-22.5 EndZ=0
    g2: LineSegment StartX=35.5 StartY=-29.5 StartZ=0 EndX=-35.5 EndY=-29.5 EndZ=0
    g3: LineSegment [constr] StartX=-40.5 StartY=27.5 StartZ=0 EndX=40.5 EndY=27.5 EndZ=0
    g4: LineSegment [constr] StartX=40.5 StartY=27.5 StartZ=0 EndX=40.5 EndY=-27.5 EndZ=0
    g5: LineSegment [constr] StartX=40.5 StartY=-27.5 StartZ=0 EndX=-40.5 EndY=-27.5 EndZ=0
    g6: LineSegment [constr] StartX=-40.5 StartY=-27.5 StartZ=0 EndX=-40.5 EndY=27.5 EndZ=0
    g7: LineSegment StartX=-42.5 StartY=22.5 StartZ=0 EndX=-42.5 EndY=-22.5 EndZ=0
    g8: ArcOfCircle CenterX=-35.5 CenterY=-22.5 CenterZ=0 NormalX=0 NormalY=0 NormalZ=1 AngleXU=0 Radius=7 StartAngle=3.14159 EndAngle=4.71239
    g9: ArcOfCircle CenterX=35.5 CenterY=-22.5 CenterZ=0 NormalX=0 NormalY=0 NormalZ=1 AngleXU=0 Radius=7 StartAngle=4.71239 EndAngle=6.28319
    g10: ArcOfCircle CenterX=35.5 CenterY=22.5 CenterZ=0 NormalX=0 NormalY=0 NormalZ=1 AngleXU=0 Radius=7 StartAngle=0 EndAngle=1.5708
    g11: ArcOfCircle CenterX=-35.5 CenterY=22.5 CenterZ=0 NormalX=0 NormalY=0 NormalZ=1 AngleXU=0 Radius=7 StartAngle=1.5708 EndAngle=3.14159
  constraints (39):
    c: Coincident(g5,g6)
    c: Coincident(g3,g6)
    c: Coincident(g4,g5)
    c: Coincident(g3,g4)
    c: Horizontal(g0)
    c: Horizontal(g2)
    c: Vertical(g1)
    c: Vertical(g7)
    c: DistanceX(g3,g3) = 81
    c: DistanceY(g4,g3) = 55
    c: DistanceY(g4,g-1) = 27.5
    c: Horizontal(g3)
    c: Vertical(g6)
    c: Vertical(g4)
    c: Radius(g8) = 7
    c: Coincident(g7,g8)
    c: Coincident(g8,g2)
    c: DistanceY(g2,g7) = 7
    c: DistanceX(g7,g2) = 7
    c: Equal(g8,g9) = 7
    c: DistanceY(g2,g5) = 2
    c: Coincident(g2,g9)
    c: Coincident(g1,g9)
    c: DistanceY(g2,g1) = 7
    c: DistanceX(g2,g1) = 7
    c: Coincident(g0,g10)
    c: Coincident(g1,g10)
    c: Equal(g10,g9)
    c: DistanceY(g1,g0) = 7
    c: DistanceX(g0,g1) = 7
    c: Coincident(g11,g7)
    c: Coincident(g11,g0)
    c: Equal(g0,g2)
    c: Equal(g7,g1)
    c: DistanceX(g7,g3) = 2
    c: DistanceX(g3,g1) = 2
    c: DistanceY(g3,g0) = 2
    c: Equal(g11,g8)
    c: Symmetric(g5,g3,g-1)
FEATURE [Sketcher::SketchObject] Sketch002  label="AuxHoles"
  MapMode = 5
  Placement = pos=(0,-29.5,0) rot=(1,0,0;1.5708rad)
  sketch-geometry (5):
    g0: Circle CenterX=28.95 CenterY=9.55 CenterZ=0 NormalX=0 NormalY=0 NormalZ=1 AngleXU=0 Radius=3.1
    g1: Circle CenterX=15.45 CenterY=9.55 CenterZ=0 NormalX=0 NormalY=0 NormalZ=1 AngleXU=0 Radius=3.1
    g2: Circle CenterX=1.95 CenterY=9.55 CenterZ=0 NormalX=0 NormalY=0 NormalZ=1 AngleXU=0 Radius=3.1
    g3: LineSegment [constr] StartX=28.95 StartY=9.55 StartZ=0 EndX=15.45 EndY=9.55 EndZ=0
    g4: LineSegment [constr] StartX=1.95 StartY=9.55 StartZ=0 EndX=15.45 EndY=9.55 EndZ=0
  constraints (13):
    c: Radius(g0) = 3.1
    c: Equal(g0,g1) = 3
    c: Equal(g2,g1)
    c: Coincident(g3,g0)
    c: Coincident(g3,g1)
    c: Horizontal(g3)
    c: Coincident(g4,g2)
    c: Coincident(g4,g1)
    c: Horizontal(g4)
    c: Equal(g4,g3)
    c: DistanceX(g3,g3) = 13.5
    c: DistanceY(g-1,g2) = 9.55
    c: DistanceX(g-1,g2) = 1.95
FEATURE [PartDesign::Mirrored] Mirrored003
  MirrorPlane = -> XZ_Plane041
  Refine = true
FEATURE [Sketcher::SketchObject] Sketch011  label="AuxHoles001"
  MapMode = 5
  Placement = pos=(0,-29.5,0) rot=(1,0,0;1.5708rad)
  sketch-geometry (3):
    g0: Circle CenterX=-11.55 CenterY=9.55 CenterZ=0 NormalX=0 NormalY=0 NormalZ=1 AngleXU=0 Radius=3.1
    g1: Circle CenterX=-25.05 CenterY=9.55 CenterZ=0 NormalX=0 NormalY=0 NormalZ=1 AngleXU=0 Radius=3.1
    g2: LineSegment [constr] StartX=-25.05 StartY=9.55 StartZ=0 EndX=-11.55 EndY=9.55 EndZ=0
  constraints (6):
    c: Equal(g0,g1)
    c: Coincident(g2,g1)
    c: Coincident(g2,g0)
    c: Horizontal(g2)
    c: Block(g2)
    c: Radius(g1) = 3.1
FEATURE [Sketcher::SketchObject] Sketch016
  MapMode = 5
  Support = -> [XY_Plane262]
  sketch-geometry (12):
    g0: LineSegment StartX=-35.6 StartY=29.6 StartZ=0 EndX=35.6 EndY=29.6 EndZ=0
    g1: LineSegment StartX=42.6 StartY=22.6 StartZ=0 EndX=42.6 EndY=-22.6 EndZ=0
    g2: LineSegment StartX=35.6 StartY=-29.6 StartZ=0 EndX=-35.6 EndY=-29.6 EndZ=0
    g3: LineSegment [constr] StartX=-40.5 StartY=27.5 StartZ=0 EndX=40.5 EndY=27.5 EndZ=0
    g4: LineSegment [constr] StartX=40.5 StartY=27.5 StartZ=0 EndX=40.5 EndY=-27.5 EndZ=0
    g5: LineSegment [constr] StartX=40.5 StartY=-27.5 StartZ=0 EndX=-40.5 EndY=-27.5 EndZ=0
    g6: LineSegment [constr] StartX=-40.5 StartY=-27.5 StartZ=0 EndX=-40.5 EndY=27.5 EndZ=0
    g7: LineSegment StartX=-42.6 StartY=22.6 StartZ=0 EndX=-42.6 EndY=-22.6 EndZ=0
    g8: ArcOfCircle CenterX=-35.6 CenterY=-22.6 CenterZ=0 NormalX=0 NormalY=0 NormalZ=1 AngleXU=0 Radius=7 StartAngle=3.14159 EndAngle=4.71239
    g9: ArcOfCircle CenterX=35.6 CenterY=-22.6 CenterZ=0 NormalX=0 NormalY=0 NormalZ=1 AngleXU=0 Radius=7 StartAngle=4.71239 EndAngle=6.28319
    g10: ArcOfCircle CenterX=35.6 CenterY=22.6 CenterZ=0 NormalX=0 NormalY=0 NormalZ=1 AngleXU=0 Radius=7 StartAngle=0 EndAngle=1.5708
    g11: ArcOfCircle CenterX=-35.6 CenterY=22.6 CenterZ=0 NormalX=0 NormalY=0 NormalZ=1 AngleXU=0 Radius=7 StartAngle=1.5708 EndAngle=3.14159
  constraints (39):
    c: Coincident(g5,g6)
    c: Coincident(g3,g6)
    c: Coincident(g4,g5)
    c: Coincident(g3,g4)
    c: Horizontal(g0)
    c: Horizontal(g2)
    c: Vertical(g1)
    c: Vertical(g7)
    c: DistanceX(g3,g3) = 81
    c: DistanceY(g4,g3) = 55
    c: DistanceY(g4,g-1) = 27.5
    c: Horizontal(g3)
    c: Vertical(g6)
    c: Vertical(g4)
    c: Radius(g8) = 7
    c: Coincident(g7,g8)
    c: Coincident(g8,g2)
    c: DistanceY(g2,g7) = 7
    c: DistanceX(g7,g2) = 7
    c: Equal(g8,g9) = 7
    c: DistanceY(g2,g5) = 2.1
    c: Coincident(g2,g9)
    c: Coincident(g1,g9)
    c: DistanceY(g2,g1) = 7
    c: DistanceX(g2,g1) = 7
    c: Coincident(g0,g10)
    c: Coincident(g1,g10)
    c: Equal(g10,g9)
    c: DistanceY(g1,g0) = 7
    c: DistanceX(g0,g1) = 7
    c: Coincident(g11,g7)
    c: Coincident(g11,g0)
    c: Equal(g0,g2)
    c: Equal(g7,g1)
    c: DistanceX(g7,g3) = 2.1
    c: DistanceX(g3,g1) = 2.1
    c: DistanceY(g3,g0) = 2.1
    c: Equal(g11,g8)
    c: Symmetric(g5,g3,g-1)
FEATURE [Sketcher::SketchObject] Sketch017  label="AuxHoles002"
  MapMode = 5
  Placement = pos=(0,-29.5,0) rot=(1,0,0;1.5708rad)
  sketch-geometry (5):
    g0: Circle CenterX=28.95 CenterY=9.55 CenterZ=0 NormalX=0 NormalY=0 NormalZ=1 AngleXU=0 Radius=3.1
    g1: Circle CenterX=15.45 CenterY=9.55 CenterZ=0 NormalX=0 NormalY=0 NormalZ=1 AngleXU=0 Radius=3.1
    g2: Circle CenterX=1.95 CenterY=9.55 CenterZ=0 NormalX=0 NormalY=0 NormalZ=1 AngleXU=0 Radius=3.1
    g3: LineSegment [constr] StartX=28.95 StartY=9.55 StartZ=0 EndX=15.45 EndY=9.55 EndZ=0
    g4: LineSegment [constr] StartX=1.95 StartY=9.55 StartZ=0 EndX=15.45 EndY=9.55 EndZ=0
  constraints (13):
    c: Radius(g0) = 3.1
    c: Equal(g0,g1) = 3
    c: Equal(g2,g1)
    c: Coincident(g3,g0)
    c: Coincident(g3,g1)
    c: Horizontal(g3)
    c: Coincident(g4,g2)
    c: Coincident(g4,g1)
    c: Horizontal(g4)
    c: Equal(g4,g3)
    c: DistanceX(g3,g3) = 13.5
    c: DistanceY(g-1,g2) = 9.55
    c: DistanceX(g-1,g2) = 1.95
FEATURE [PartDesign::Pad] Pad003  label="body_Box"
  Length = 10.05
  Length2 = 5.7
  Profile = -> Sketch016
  Refine = true
  Type = 4
FEATURE [Sketcher::SketchObject] Sketch014  label="BoxCut002"
  AttachmentOffset = pos=(0,0,0.5) rot=(0,0,1;0rad)
  ExternalGeometry = -> [Pad003]
  MapMode = 5
  Placement = pos=(0,0,0.5) rot=(0,0,1;0rad)
  Support = -> [XY_Plane262]
  sketch-geometry (8):
    g0: LineSegment StartX=-35.6 StartY=28 StartZ=0 EndX=35.6 EndY=28 EndZ=0
    g1: ArcOfCircle CenterX=35.6 CenterY=22.6 CenterZ=0 NormalX=0 NormalY=0 NormalZ=1 AngleXU=0 Radius=5.4 StartAngle=1e-16 EndAngle=1.5708
    g2: LineSegment StartX=41 StartY=22.6 StartZ=0 EndX=41 EndY=-22.6 EndZ=0
    g3: LineSegment StartX=35.6 StartY=-28 StartZ=0 EndX=-35.6 EndY=-28 EndZ=0
    g4: ArcOfCircle CenterX=-35.6 CenterY=-22.6 CenterZ=0 NormalX=0 NormalY=0 NormalZ=1 AngleXU=0 Radius=5.4 StartAngle=3.14159 EndAngle=4.71239
    g5: LineSegment StartX=-41 StartY=-22.6 StartZ=0 EndX=-41 EndY=22.6 EndZ=0
    g6: ArcOfCircle CenterX=-35.6 CenterY=22.6 CenterZ=0 NormalX=0 NormalY=0 NormalZ=1 AngleXU=0 Radius=5.4 StartAngle=1.5708 EndAngle=3.14159
    g7: ArcOfCircle CenterX=35.6 CenterY=-22.6 CenterZ=0 NormalX=0 NormalY=0 NormalZ=1 AngleXU=0 Radius=5.4 StartAngle=4.71239 EndAngle=6.28318
  constraints (19):
    c: Horizontal(g0)
    c: Tangent(g0,g1) = 1.5708
    c: Tangent(g1,g2) = 1.5708
    c: Tangent(g3,g4) = 1.5708
    c: Tangent(g4,g5) = 1.5708
    c: Tangent(g5,g6) = 1.5708
    c: Coincident(g6,g0)
    c: Coincident(g6,g-4)
    c: Coincident(g1,g-10)
    c: Coincident(g4,g-6)
    c: Vertical(g5)
    c: Horizontal(g3)
    c: DistanceY(g0,g-4) = 1.6
    c: Vertical(g2)
    c: Tangent(g0,g6,g0) = 1.5708
    c: Equal(g4,g7)
    c: Coincident(g7,g2)
    c: Coincident(g7,g3)
    c: Coincident(g-8,g7)
FEATURE [Sketcher::SketchObject] Sketch019  label="EdgePCBHolder002"
  ExternalGeometry = -> [Pad003]
  MapMode = 5
  Support = -> [XY_Plane262]
  sketch-geometry (6):
    g0: LineSegment StartX=38.6 StartY=-19.6 StartZ=0 EndX=41.2 EndY=-19.6 EndZ=0
    g1: ArcOfCircle CenterX=38.6 CenterY=-25.6 CenterZ=0 NormalX=0 NormalY=0 NormalZ=1 AngleXU=0 Radius=6 StartAngle=1.5708 EndAngle=3.14159
    g2: LineSegment StartX=32.6 StartY=-28.2 StartZ=0 EndX=32.6 EndY=-25.6 EndZ=0
    g3: LineSegment StartX=41.2 StartY=-19.6 StartZ=0 EndX=41.2 EndY=-22.6 EndZ=0
    g4: ArcOfCircle CenterX=35.6 CenterY=-22.6 CenterZ=0 NormalX=0 NormalY=0 NormalZ=1 AngleXU=0 Radius=5.6 StartAngle=4.71239 EndAngle=6.28319
    g5: LineSegment StartX=32.6 StartY=-28.2 StartZ=0 EndX=35.6 EndY=-28.2 EndZ=0
  constraints (19):
    c: Horizontal(g0)
    c: Coincident(g1,g0)
    c: Coincident(g2,g1)
    c: Vertical(g2)
    c: Coincident(g3,g0)
    c: Vertical(g3)
    c: DistanceY(g3,g3) = 3
    c: Coincident(g2,g5)
    c: Coincident(g5,g4)
    c: Horizontal(g5)
    c: DistanceX(g5,g5) = 3
    c: Coincident(g-10,g4)
    c: Coincident(g3,g4)
    c: Radius(g1) = 6
    c: Vertical(g0,g1)
    c: Horizontal(g1,g1)
    c: Horizontal(g3,g-10)
    c: Vertical(g4,g-10)
    c: DistanceY(g-10,g4) = 1.4
FEATURE [PartDesign::Pocket] Pocket007  label="body_Box_cut"
  BaseFeature = -> Pad003
  Length = 4.7
  Length2 = 22
  Profile = -> Sketch014
  Refine = true
  Reversed = true
  Type = 4
FEATURE [Sketcher::SketchObject] Sketch020  label="AuxHoles003"
  MapMode = 5
  Placement = pos=(0,0,0) rot=(1,0,0;1.5708rad)
  sketch-geometry (3):
    g0: Circle CenterX=-11.55 CenterY=9.55 CenterZ=0 NormalX=0 NormalY=0 NormalZ=1 AngleXU=0 Radius=3.1
    g1: Circle CenterX=-25.05 CenterY=9.55 CenterZ=0 NormalX=0 NormalY=0 NormalZ=1 AngleXU=0 Radius=3.1
    g2: LineSegment [constr] StartX=-25.05 StartY=9.55 StartZ=0 EndX=-11.55 EndY=9.55 EndZ=0
  constraints (6):
    c: Equal(g0,g1)
    c: Coincident(g2,g1)
    c: Coincident(g2,g0)
    c: Horizontal(g2)
    c: Block(g2)
    c: Radius(g1) = 3.1
FEATURE [Sketcher::SketchObject] Sketch022
  ExternalGeometry = -> [Pad003]
  MapMode = 5
  Placement = pos=(0,0,9.55) rot=(0,0,1;0rad)
  sketch-geometry (12):
    g0: LineSegment StartX=-35.6 StartY=28.6 StartZ=0 EndX=35.6 EndY=28.6 EndZ=0
    g1: ArcOfCircle CenterX=35.6 CenterY=22.6 CenterZ=0 NormalX=0 NormalY=0 NormalZ=1 AngleXU=0 Radius=6 StartAngle=3e-16 EndAngle=1.5708
    g2: LineSegment StartX=41.6 StartY=22.6 StartZ=0 EndX=41.6 EndY=-22.6 EndZ=0
    g3: ArcOfCircle CenterX=35.6 CenterY=-22.6 CenterZ=0 NormalX=0 NormalY=0 NormalZ=1 AngleXU=0 Radius=6 StartAngle=4.71239 EndAngle=6.28319
    g4: LineSegment StartX=35.6 StartY=-28.6 StartZ=0 EndX=-35.6 EndY=-28.6 EndZ=0
    g5: ArcOfCircle CenterX=-35.6 CenterY=-22.6 CenterZ=0 NormalX=0 NormalY=0 NormalZ=1 AngleXU=0 Radius=6 StartAngle=3.14159 EndAngle=4.71239
    g6: LineSegment StartX=-41.6 StartY=-22.6 StartZ=0 EndX=-41.6 EndY=22.6 EndZ=0
    g7: ArcOfCircle CenterX=-35.6 CenterY=22.6 CenterZ=0 NormalX=0 NormalY=0 NormalZ=1 AngleXU=0 Radius=6 StartAngle=1.5708 EndAngle=3.14159
    g8: LineSegment StartX=-73.2412 StartY=65.8475 StartZ=0 EndX=83.9868 EndY=65.8475 EndZ=0
    g9: LineSegment StartX=83.9868 StartY=65.8475 StartZ=0 EndX=83.9868 EndY=-54.3566 EndZ=0
    g10: LineSegment StartX=83.9868 StartY=-54.3566 StartZ=0 EndX=-73.2412 EndY=-54.3566 EndZ=0
    g11: LineSegment StartX=-73.2412 StartY=-54.3566 StartZ=0 EndX=-73.2412 EndY=65.8475 EndZ=0
  constraints (25):
    c: Horizontal(g0)
    c: Tangent(g0,g1) = 1.5708
    c: Tangent(g1,g2) = 1.5708
    c: Tangent(g2,g3) = 1.5708
    c: Tangent(g3,g4) = 1.5708
    c: Tangent(g4,g5) = 1.5708
    c: Tangent(g5,g6) = 1.5708
    c: Tangent(g6,g7) = 1.5708
    c: Coincident(g7,g0)
    c: Horizontal(g4)
    c: Coincident(g5,g-6)
    c: Coincident(g3,g-8)
    c: Coincident(g-10,g1)
    c: Coincident(g7,g-4)
    c: Vertical(g6)
    c: DistanceY(g0,g-4) = 1
    c: DistanceX(g-5,g6) = 1
    c: Coincident(g8,g9)
    c: Coincident(g9,g10)
    c: Coincident(g10,g11)
    c: Coincident(g11,g8)
    c: Horizontal(g8)
    c: Horizontal(g10)
    c: Vertical(g9)
    c: Vertical(g11)
FEATURE [PartDesign::Pocket] Pocket011  label="Aux_Holes_003"
  BaseFeature = -> Pocket007
  Length = 92
  Length2 = 1
  Profile = -> Sketch020
  Refine = true
  Type = 4
FEATURE [PartDesign::Pocket] Pocket008  label="AuxHoles_007"
  BaseFeature = -> Pocket011
  Length = 60
  Length2 = 1
  Profile = -> Sketch017
  Refine = true
  Type = 4
FEATURE [PartDesign::Pocket] Pocket012  label="MountingEdge001"
  BaseFeature = -> Pocket008
  Length = 5
  Length2 = 100
  Profile = -> Sketch022
  Refine = true
  Reversed = true
  Type = 0
FEATURE [Sketcher::SketchObject] Sketch032  label="Logo"
  Placement = pos=(-2.83251,-58.1877,-7) rot=(0,1,0;3.14159rad)
  sketch-geometry (282):
    g0: BSplineCurve PolesCount=4 KnotsCount=2 Degree=3 IsPeriodic=0
    g1: BSplineCurve PolesCount=4 KnotsCount=2 Degree=3 IsPeriodic=0
    g2: BSplineCurve PolesCount=4 KnotsCount=2 Degree=3 IsPeriodic=0
    g3: BSplineCurve PolesCount=4 KnotsCount=2 Degree=3 IsPeriodic=0
    g4: BSplineCurve PolesCount=4 KnotsCount=2 Degree=3 IsPeriodic=0
    g5: BSplineCurve PolesCount=4 KnotsCount=2 Degree=3 IsPeriodic=0
    g6: BSplineCurve PolesCount=4 KnotsCount=2 Degree=3 IsPeriodic=0
    g7: BSplineCurve PolesCount=4 KnotsCount=2 Degree=3 IsPeriodic=0
    g8: BSplineCurve PolesCount=4 KnotsCount=2 Degree=3 IsPeriodic=0
    g9: BSplineCurve PolesCount=4 KnotsCount=2 Degree=3 IsPeriodic=0
    g10: BSplineCurve PolesCount=4 KnotsCount=2 Degree=3 IsPeriodic=0
    g11: BSplineCurve PolesCount=4 KnotsCount=2 Degree=3 IsPeriodic=0
    g12: BSplineCurve PolesCount=4 KnotsCount=2 Degree=3 IsPeriodic=0
    g13: BSplineCurve PolesCount=4 KnotsCount=2 Degree=3 IsPeriodic=0
    g14: BSplineCurve PolesCount=4 KnotsCount=2 Degree=3 IsPeriodic=0
    g15: BSplineCurve PolesCount=4 KnotsCount=2 Degree=3 IsPeriodic=0
    g16: BSplineCurve PolesCount=4 KnotsCount=2 Degree=3 IsPeriodic=0
    g17: BSplineCurve PolesCount=4 KnotsCount=2 Degree=3 IsPeriodic=0
    g18: BSplineCurve PolesCount=4 KnotsCount=2 Degree=3 IsPeriodic=0
    g19: BSplineCurve PolesCount=4 KnotsCount=2 Degree=3 IsPeriodic=0
    g20: BSplineCurve PolesCount=4 KnotsCount=2 Degree=3 IsPeriodic=0
    g21: BSplineCurve PolesCount=4 KnotsCount=2 Degree=3 IsPeriodic=0
    g22: BSplineCurve PolesCount=4 KnotsCount=2 Degree=3 IsPeriodic=0
    g23: BSplineCurve PolesCount=4 KnotsCount=2 Degree=3 IsPeriodic=0
    g24: BSplineCurve PolesCount=4 KnotsCount=2 Degree=3 IsPeriodic=0
    g25: BSplineCurve PolesCount=4 KnotsCount=2 Degree=3 IsPeriodic=0
    g26: BSplineCurve PolesCount=4 KnotsCount=2 Degree=3 IsPeriodic=0
    g27: BSplineCurve PolesCount=4 KnotsCount=2 Degree=3 IsPeriodic=0
    g28: BSplineCurve PolesCount=4 KnotsCount=2 Degree=3 IsPeriodic=0
    g29: BSplineCurve PolesCount=4 KnotsCount=2 Degree=3 IsPeriodic=0
    g30: BSplineCurve PolesCount=4 KnotsCount=2 Degree=3 IsPeriodic=0
    g31: BSplineCurve PolesCount=4 KnotsCount=2 Degree=3 IsPeriodic=0
    g32: BSplineCurve PolesCount=4 KnotsCount=2 Degree=3 IsPeriodic=0
    g33: BSplineCurve PolesCount=4 KnotsCount=2 Degree=3 IsPeriodic=0
    g34: BSplineCurve PolesCount=4 KnotsCount=2 Degree=3 IsPeriodic=0
    g35: BSplineCurve PolesCount=4 KnotsCount=2 Degree=3 IsPeriodic=0
    g36: BSplineCurve PolesCount=4 KnotsCount=2 Degree=3 IsPeriodic=0
    g37: BSplineCurve PolesCount=4 KnotsCount=2 Degree=3 IsPeriodic=0
    g38: BSplineCurve PolesCount=4 KnotsCount=2 Degree=3 IsPeriodic=0
    g39: BSplineCurve PolesCount=4 KnotsCount=2 Degree=3 IsPeriodic=0
    g40: BSplineCurve PolesCount=4 KnotsCount=2 Degree=3 IsPeriodic=0
    g41: BSplineCurve PolesCount=4 KnotsCount=2 Degree=3 IsPeriodic=0
    g42: BSplineCurve PolesCount=4 KnotsCount=2 Degree=3 IsPeriodic=0
    g43: BSplineCurve PolesCount=4 KnotsCount=2 Degree=3 IsPeriodic=0
    g44: BSplineCurve PolesCount=4 KnotsCount=2 Degree=3 IsPeriodic=0
    g45: BSplineCurve PolesCount=4 KnotsCount=2 Degree=3 IsPeriodic=0
    g46: BSplineCurve PolesCount=4 KnotsCount=2 Degree=3 IsPeriodic=0
    g47: BSplineCurve PolesCount=4 KnotsCount=2 Degree=3 IsPeriodic=0
    g48: BSplineCurve PolesCount=4 KnotsCount=2 Degree=3 IsPeriodic=0
    g49: BSplineCurve PolesCount=4 KnotsCount=2 Degree=3 IsPeriodic=0
    g50: BSplineCurve PolesCount=4 KnotsCount=2 Degree=3 IsPeriodic=0
    g51: BSplineCurve PolesCount=4 KnotsCount=2 Degree=3 IsPeriodic=0
    g52: BSplineCurve PolesCount=4 KnotsCount=2 Degree=3 IsPeriodic=0
    g53: BSplineCurve PolesCount=4 KnotsCount=2 Degree=3 IsPeriodic=0
    g54: BSplineCurve PolesCount=4 KnotsCount=2 Degree=3 IsPeriodic=0
    g55: BSplineCurve PolesCount=4 KnotsCount=2 Degree=3 IsPeriodic=0
    g56: BSplineCurve PolesCount=4 KnotsCount=2 Degree=3 IsPeriodic=0
    g57: BSplineCurve PolesCount=4 KnotsCount=2 Degree=3 IsPeriodic=0
    g58: BSplineCurve PolesCount=4 KnotsCount=2 Degree=3 IsPeriodic=0
    g59: BSplineCurve PolesCount=4 KnotsCount=2 Degree=3 IsPeriodic=0
    g60: BSplineCurve PolesCount=4 KnotsCount=2 Degree=3 IsPeriodic=0
    g61: BSplineCurve PolesCount=4 KnotsCount=2 Degree=3 IsPeriodic=0
    g62: BSplineCurve PolesCount=4 KnotsCount=2 Degree=3 IsPeriodic=0
    g63: BSplineCurve PolesCount=4 KnotsCount=2 Degree=3 IsPeriodic=0
    g64: BSplineCurve PolesCount=4 KnotsCount=2 Degree=3 IsPeriodic=0
    g65: BSplineCurve PolesCount=4 KnotsCount=2 Degree=3 IsPeriodic=0
    g66: BSplineCurve PolesCount=4 KnotsCount=2 Degree=3 IsPeriodic=0
    g67: BSplineCurve PolesCount=4 KnotsCount=2 Degree=3 IsPeriodic=0
    g68: BSplineCurve PolesCount=4 KnotsCount=2 Degree=3 IsPeriodic=0
    g69: BSplineCurve PolesCount=4 KnotsCount=2 Degree=3 IsPeriodic=0
    g70: BSplineCurve PolesCount=4 KnotsCount=2 Degree=3 IsPeriodic=0
    g71: BSplineCurve PolesCount=4 KnotsCount=2 Degree=3 IsPeriodic=0
    g72: BSplineCurve PolesCount=4 KnotsCount=2 Degree=3 IsPeriodic=0
    g73: BSplineCurve PolesCount=4 KnotsCount=2 Degree=3 IsPeriodic=0
    g74: BSplineCurve PolesCount=4 KnotsCount=2 Degree=3 IsPeriodic=0
    g75: BSplineCurve PolesCount=4 KnotsCount=2 Degree=3 IsPeriodic=0
    g76: BSplineCurve PolesCount=4 KnotsCount=2 Degree=3 IsPeriodic=0
    g77: BSplineCurve PolesCount=4 KnotsCount=2 Degree=3 IsPeriodic=0
    g78: BSplineCurve PolesCount=4 KnotsCount=2 Degree=3 IsPeriodic=0
    g79: BSplineCurve PolesCount=4 KnotsCount=2 Degree=3 IsPeriodic=0
    g80: BSplineCurve PolesCount=4 KnotsCount=2 Degree=3 IsPeriodic=0
    g81: BSplineCurve PolesCount=4 KnotsCount=2 Degree=3 IsPeriodic=0
    g82: BSplineCurve PolesCount=4 KnotsCount=2 Degree=3 IsPeriodic=0
    g83: BSplineCurve PolesCount=4 KnotsCount=2 Degree=3 IsPeriodic=0
    g84: BSplineCurve PolesCount=4 KnotsCount=2 Degree=3 IsPeriodic=0
    g85: BSplineCurve PolesCount=4 KnotsCount=2 Degree=3 IsPeriodic=0
    g86: BSplineCurve PolesCount=4 KnotsCount=2 Degree=3 IsPeriodic=0
    g87: BSplineCurve PolesCount=4 KnotsCount=2 Degree=3 IsPeriodic=0
    g88: BSplineCurve PolesCount=4 KnotsCount=2 Degree=3 IsPeriodic=0
    g89: BSplineCurve PolesCount=4 KnotsCount=2 Degree=3 IsPeriodic=0
    g90: BSplineCurve PolesCount=4 KnotsCount=2 Degree=3 IsPeriodic=0
    g91: BSplineCurve PolesCount=4 KnotsCount=2 Degree=3 IsPeriodic=0
    g92: BSplineCurve PolesCount=4 KnotsCount=2 Degree=3 IsPeriodic=0
    g93: BSplineCurve PolesCount=4 KnotsCount=2 Degree=3 IsPeriodic=0
    g94: BSplineCurve PolesCount=4 KnotsCount=2 Degree=3 IsPeriodic=0
    g95: BSplineCurve PolesCount=4 KnotsCount=2 Degree=3 IsPeriodic=0
    g96: BSplineCurve PolesCount=4 KnotsCount=2 Degree=3 IsPeriodic=0
    g97: BSplineCurve PolesCount=4 KnotsCount=2 Degree=3 IsPeriodic=0
    g98: BSplineCurve PolesCount=4 KnotsCount=2 Degree=3 IsPeriodic=0
    g99: BSplineCurve PolesCount=4 KnotsCount=2 Degree=3 IsPeriodic=0
    g100: BSplineCurve PolesCount=4 KnotsCount=2 Degree=3 IsPeriodic=0
    g101: BSplineCurve PolesCount=4 KnotsCount=2 Degree=3 IsPeriodic=0
    g102: BSplineCurve PolesCount=4 KnotsCount=2 Degree=3 IsPeriodic=0
    g103: BSplineCurve PolesCount=4 KnotsCount=2 Degree=3 IsPeriodic=0
    g104: BSplineCurve PolesCount=4 KnotsCount=2 Degree=3 IsPeriodic=0
    g105: BSplineCurve PolesCount=4 KnotsCount=2 Degree=3 IsPeriodic=0
    g106: BSplineCurve PolesCount=4 KnotsCount=2 Degree=3 IsPeriodic=0
    g107: BSplineCurve PolesCount=4 KnotsCount=2 Degree=3 IsPeriodic=0
    g108: BSplineCurve PolesCount=4 KnotsCount=2 Degree=3 IsPeriodic=0
    g109: BSplineCurve PolesCount=4 KnotsCount=2 Degree=3 IsPeriodic=0
    g110: BSplineCurve PolesCount=4 KnotsCount=2 Degree=3 IsPeriodic=0
    g111: BSplineCurve PolesCount=4 KnotsCount=2 Degree=3 IsPeriodic=0
    g112: BSplineCurve PolesCount=4 KnotsCount=2 Degree=3 IsPeriodic=0
    g113: BSplineCurve PolesCount=4 KnotsCount=2 Degree=3 IsPeriodic=0
    g114: BSplineCurve PolesCount=4 KnotsCount=2 Degree=3 IsPeriodic=0
    g115: BSplineCurve PolesCount=4 KnotsCount=2 Degree=3 IsPeriodic=0
    g116: BSplineCurve PolesCount=4 KnotsCount=2 Degree=3 IsPeriodic=0
    g117: BSplineCurve PolesCount=4 KnotsCount=2 Degree=3 IsPeriodic=0
    g118: BSplineCurve PolesCount=4 KnotsCount=2 Degree=3 IsPeriodic=0
    g119: BSplineCurve PolesCount=4 KnotsCount=2 Degree=3 IsPeriodic=0
    g120: BSplineCurve PolesCount=4 KnotsCount=2 Degree=3 IsPeriodic=0
    g121: BSplineCurve PolesCount=4 KnotsCount=2 Degree=3 IsPeriodic=0
    g122: BSplineCurve PolesCount=4 KnotsCount=2 Degree=3 IsPeriodic=0
    g123: BSplineCurve PolesCount=4 KnotsCount=2 Degree=3 IsPeriodic=0
    g124: BSplineCurve PolesCount=4 KnotsCount=2 Degree=3 IsPeriodic=0
    g125: BSplineCurve PolesCount=4 KnotsCount=2 Degree=3 IsPeriodic=0
    g126: BSplineCurve PolesCount=4 KnotsCount=2 Degree=3 IsPeriodic=0
    g127: BSplineCurve PolesCount=4 KnotsCount=2 Degree=3 IsPeriodic=0
    g128: BSplineCurve PolesCount=4 KnotsCount=2 Degree=3 IsPeriodic=0
    g129: BSplineCurve PolesCount=4 KnotsCount=2 Degree=3 IsPeriodic=0
    g130: BSplineCurve PolesCount=4 KnotsCount=2 Degree=3 IsPeriodic=0
    g131: BSplineCurve PolesCount=4 KnotsCount=2 Degree=3 IsPeriodic=0
    g132: BSplineCurve PolesCount=4 KnotsCount=2 Degree=3 IsPeriodic=0
    g133: BSplineCurve PolesCount=4 KnotsCount=2 Degree=3 IsPeriodic=0
    g134: BSplineCurve PolesCount=4 KnotsCount=2 Degree=3 IsPeriodic=0
    g135: BSplineCurve PolesCount=4 KnotsCount=2 Degree=3 IsPeriodic=0
    g136: BSplineCurve PolesCount=4 KnotsCount=2 Degree=3 IsPeriodic=0
    g137: BSplineCurve PolesCount=4 KnotsCount=2 Degree=3 IsPeriodic=0
    g138: BSplineCurve PolesCount=4 KnotsCount=2 Degree=3 IsPeriodic=0
    g139: BSplineCurve PolesCount=4 KnotsCount=2 Degree=3 IsPeriodic=0
    g140: BSplineCurve PolesCount=4 KnotsCount=2 Degree=3 IsPeriodic=0
    g141: BSplineCurve PolesCount=4 KnotsCount=2 Degree=3 IsPeriodic=0
    g142: BSplineCurve PolesCount=4 KnotsCount=2 Degree=3 IsPeriodic=0
    g143: BSplineCurve PolesCount=4 KnotsCount=2 Degree=3 IsPeriodic=0
    g144: BSplineCurve PolesCount=4 KnotsCount=2 Degree=3 IsPeriodic=0
    g145: BSplineCurve PolesCount=4 KnotsCount=2 Degree=3 IsPeriodic=0
    g146: BSplineCurve PolesCount=4 KnotsCount=2 Degree=3 IsPeriodic=0
    g147: BSplineCurve PolesCount=4 KnotsCount=2 Degree=3 IsPeriodic=0
    g148: BSplineCurve PolesCount=4 KnotsCount=2 Degree=3 IsPeriodic=0
    g149: BSplineCurve PolesCount=4 KnotsCount=2 Degree=3 IsPeriodic=0
    g150: BSplineCurve PolesCount=4 KnotsCount=2 Degree=3 IsPeriodic=0
    g151: BSplineCurve PolesCount=4 KnotsCount=2 Degree=3 IsPeriodic=0
    g152: BSplineCurve PolesCount=4 KnotsCount=2 Degree=3 IsPeriodic=0
    g153: BSplineCurve PolesCount=4 KnotsCount=2 Degree=3 IsPeriodic=0
    g154: BSplineCurve PolesCount=4 KnotsCount=2 Degree=3 IsPeriodic=0
    g155: BSplineCurve PolesCount=4 KnotsCount=2 Degree=3 IsPeriodic=0
    g156: BSplineCurve PolesCount=4 KnotsCount=2 Degree=3 IsPeriodic=0
    g157: BSplineCurve PolesCount=4 KnotsCount=2 Degree=3 IsPeriodic=0
    g158: BSplineCurve PolesCount=4 KnotsCount=2 Degree=3 IsPeriodic=0
    g159: BSplineCurve PolesCount=4 KnotsCount=2 Degree=3 IsPeriodic=0
    g160: BSplineCurve PolesCount=4 KnotsCount=2 Degree=3 IsPeriodic=0
    g161: BSplineCurve PolesCount=4 KnotsCount=2 Degree=3 IsPeriodic=0
    g162: BSplineCurve PolesCount=4 KnotsCount=2 Degree=3 IsPeriodic=0
    g163: BSplineCurve PolesCount=4 KnotsCount=2 Degree=3 IsPeriodic=0
    g164: BSplineCurve PolesCount=4 KnotsCount=2 Degree=3 IsPeriodic=0
    g165: BSplineCurve PolesCount=4 KnotsCount=2 Degree=3 IsPeriodic=0
    g166: BSplineCurve PolesCount=4 KnotsCount=2 Degree=3 IsPeriodic=0
    g167: BSplineCurve PolesCount=4 KnotsCount=2 Degree=3 IsPeriodic=0
    g168: BSplineCurve PolesCount=4 KnotsCount=2 Degree=3 IsPeriodic=0
    g169: BSplineCurve PolesCount=4 KnotsCount=2 Degree=3 IsPeriodic=0
    g170: BSplineCurve PolesCount=4 KnotsCount=2 Degree=3 IsPeriodic=0
    g171: BSplineCurve PolesCount=4 KnotsCount=2 Degree=3 IsPeriodic=0
    g172: BSplineCurve PolesCount=4 KnotsCount=2 Degree=3 IsPeriodic=0
    g173: BSplineCurve PolesCount=4 KnotsCount=2 Degree=3 IsPeriodic=0
    g174: BSplineCurve PolesCount=4 KnotsCount=2 Degree=3 IsPeriodic=0
    g175: BSplineCurve PolesCount=4 KnotsCount=2 Degree=3 IsPeriodic=0
    g176: BSplineCurve PolesCount=4 KnotsCount=2 Degree=3 IsPeriodic=0
    g177: BSplineCurve PolesCount=4 KnotsCount=2 Degree=3 IsPeriodic=0
    g178: BSplineCurve PolesCount=4 KnotsCount=2 Degree=3 IsPeriodic=0
    g179: BSplineCurve PolesCount=4 KnotsCount=2 Degree=3 IsPeriodic=0
    g180: BSplineCurve PolesCount=4 KnotsCount=2 Degree=3 IsPeriodic=0
    g181: BSplineCurve PolesCount=4 KnotsCount=2 Degree=3 IsPeriodic=0
    g182: BSplineCurve PolesCount=4 KnotsCount=2 Degree=3 IsPeriodic=0
    g183: BSplineCurve PolesCount=4 KnotsCount=2 Degree=3 IsPeriodic=0
    g184: BSplineCurve PolesCount=4 KnotsCount=2 Degree=3 IsPeriodic=0
    g185: BSplineCurve PolesCount=4 KnotsCount=2 Degree=3 IsPeriodic=0
    g186: BSplineCurve PolesCount=4 KnotsCount=2 Degree=3 IsPeriodic=0
    g187: BSplineCurve PolesCount=4 KnotsCount=2 Degree=3 IsPeriodic=0
    g188: BSplineCurve PolesCount=4 KnotsCount=2 Degree=3 IsPeriodic=0
    g189: BSplineCurve PolesCount=4 KnotsCount=2 Degree=3 IsPeriodic=0
    g190: BSplineCurve PolesCount=4 KnotsCount=2 Degree=3 IsPeriodic=0
    g191: BSplineCurve PolesCount=4 KnotsCount=2 Degree=3 IsPeriodic=0
    g192: BSplineCurve PolesCount=4 KnotsCount=2 Degree=3 IsPeriodic=0
    g193: BSplineCurve PolesCount=4 KnotsCount=2 Degree=3 IsPeriodic=0
    g194: BSplineCurve PolesCount=4 KnotsCount=2 Degree=3 IsPeriodic=0
    g195: BSplineCurve PolesCount=4 KnotsCount=2 Degree=3 IsPeriodic=0
    g196: BSplineCurve PolesCount=4 KnotsCount=2 Degree=3 IsPeriodic=0
    g197: BSplineCurve PolesCount=4 KnotsCount=2 Degree=3 IsPeriodic=0
    g198: BSplineCurve PolesCount=4 KnotsCount=2 Degree=3 IsPeriodic=0
    g199: BSplineCurve PolesCount=4 KnotsCount=2 Degree=3 IsPeriodic=0
    g200: BSplineCurve PolesCount=4 KnotsCount=2 Degree=3 IsPeriodic=0
    g201: BSplineCurve PolesCount=4 KnotsCount=2 Degree=3 IsPeriodic=0
    g202: BSplineCurve PolesCount=4 KnotsCount=2 Degree=3 IsPeriodic=0
    g203: BSplineCurve PolesCount=4 KnotsCount=2 Degree=3 IsPeriodic=0
    g204: BSplineCurve PolesCount=4 KnotsCount=2 Degree=3 IsPeriodic=0
    g205: BSplineCurve PolesCount=4 KnotsCount=2 Degree=3 IsPeriodic=0
    g206: BSplineCurve PolesCount=4 KnotsCount=2 Degree=3 IsPeriodic=0
    g207: BSplineCurve PolesCount=4 KnotsCount=2 Degree=3 IsPeriodic=0
    g208: BSplineCurve PolesCount=4 KnotsCount=2 Degree=3 IsPeriodic=0
    g209: BSplineCurve PolesCount=4 KnotsCount=2 Degree=3 IsPeriodic=0
    g210: BSplineCurve PolesCount=4 KnotsCount=2 Degree=3 IsPeriodic=0
    g211: BSplineCurve PolesCount=4 KnotsCount=2 Degree=3 IsPeriodic=0
    g212: BSplineCurve PolesCount=4 KnotsCount=2 Degree=3 IsPeriodic=0
    g213: BSplineCurve PolesCount=4 KnotsCount=2 Degree=3 IsPeriodic=0
    g214: BSplineCurve PolesCount=4 KnotsCount=2 Degree=3 IsPeriodic=0
    g215: BSplineCurve PolesCount=4 KnotsCount=2 Degree=3 IsPeriodic=0
    g216: BSplineCurve PolesCount=4 KnotsCount=2 Degree=3 IsPeriodic=0
    g217: BSplineCurve PolesCount=4 KnotsCount=2 Degree=3 IsPeriodic=0
    g218: BSplineCurve PolesCount=4 KnotsCount=2 Degree=3 IsPeriodic=0
    g219: BSplineCurve PolesCount=4 KnotsCount=2 Degree=3 IsPeriodic=0
    g220: BSplineCurve PolesCount=4 KnotsCount=2 Degree=3 IsPeriodic=0
    g221: BSplineCurve PolesCount=4 KnotsCount=2 Degree=3 IsPeriodic=0
    g222: BSplineCurve PolesCount=4 KnotsCount=2 Degree=3 IsPeriodic=0
    g223: BSplineCurve PolesCount=4 KnotsCount=2 Degree=3 IsPeriodic=0
    g224: BSplineCurve PolesCount=4 KnotsCount=2 Degree=3 IsPeriodic=0
    g225: BSplineCurve PolesCount=4 KnotsCount=2 Degree=3 IsPeriodic=0
    g226: BSplineCurve PolesCount=4 KnotsCount=2 Degree=3 IsPeriodic=0
    g227: BSplineCurve PolesCount=4 KnotsCount=2 Degree=3 IsPeriodic=0
    g228: BSplineCurve PolesCount=4 KnotsCount=2 Degree=3 IsPeriodic=0
    g229: BSplineCurve PolesCount=4 KnotsCount=2 Degree=3 IsPeriodic=0
    g230: BSplineCurve PolesCount=4 KnotsCount=2 Degree=3 IsPeriodic=0
    g231: BSplineCurve PolesCount=4 KnotsCount=2 Degree=3 IsPeriodic=0
    g232: BSplineCurve PolesCount=4 KnotsCount=2 Degree=3 IsPeriodic=0
    g233: BSplineCurve PolesCount=4 KnotsCount=2 Degree=3 IsPeriodic=0
    g234: BSplineCurve PolesCount=4 KnotsCount=2 Degree=3 IsPeriodic=0
    g235: BSplineCurve PolesCount=4 KnotsCount=2 Degree=3 IsPeriodic=0
    g236: BSplineCurve PolesCount=4 KnotsCount=2 Degree=3 IsPeriodic=0
    g237: BSplineCurve PolesCount=4 KnotsCount=2 Degree=3 IsPeriodic=0
    g238: BSplineCurve PolesCount=4 KnotsCount=2 Degree=3 IsPeriodic=0
    g239: BSplineCurve PolesCount=4 KnotsCount=2 Degree=3 IsPeriodic=0
    g240: BSplineCurve PolesCount=4 KnotsCount=2 Degree=3 IsPeriodic=0
    g241: BSplineCurve PolesCount=4 KnotsCount=2 Degree=3 IsPeriodic=0
    g242: BSplineCurve PolesCount=4 KnotsCount=2 Degree=3 IsPeriodic=0
    g243: BSplineCurve PolesCount=4 KnotsCount=2 Degree=3 IsPeriodic=0
    g244: BSplineCurve PolesCount=4 KnotsCount=2 Degree=3 IsPeriodic=0
    g245: BSplineCurve PolesCount=4 KnotsCount=2 Degree=3 IsPeriodic=0
    g246: BSplineCurve PolesCount=4 KnotsCount=2 Degree=3 IsPeriodic=0
    g247: BSplineCurve PolesCount=4 KnotsCount=2 Degree=3 IsPeriodic=0
    g248: BSplineCurve PolesCount=4 KnotsCount=2 Degree=3 IsPeriodic=0
    g249: BSplineCurve PolesCount=4 KnotsCount=2 Degree=3 IsPeriodic=0
    g250: BSplineCurve PolesCount=4 KnotsCount=2 Degree=3 IsPeriodic=0
    g251: BSplineCurve PolesCount=4 KnotsCount=2 Degree=3 IsPeriodic=0
    g252: BSplineCurve PolesCount=4 KnotsCount=2 Degree=3 IsPeriodic=0
    g253: BSplineCurve PolesCount=4 KnotsCount=2 Degree=3 IsPeriodic=0
    g254: BSplineCurve PolesCount=4 KnotsCount=2 Degree=3 IsPeriodic=0
    g255: BSplineCurve PolesCount=4 KnotsCount=2 Degree=3 IsPeriodic=0
    g256: BSplineCurve PolesCount=4 KnotsCount=2 Degree=3 IsPeriodic=0
    g257: BSplineCurve PolesCount=4 KnotsCount=2 Degree=3 IsPeriodic=0
    g258: BSplineCurve PolesCount=4 KnotsCount=2 Degree=3 IsPeriodic=0
    g259: BSplineCurve PolesCount=4 KnotsCount=2 Degree=3 IsPeriodic=0
    g260: BSplineCurve PolesCount=4 KnotsCount=2 Degree=3 IsPeriodic=0
    g261: BSplineCurve PolesCount=4 KnotsCount=2 Degree=3 IsPeriodic=0
    g262: BSplineCurve PolesCount=4 KnotsCount=2 Degree=3 IsPeriodic=0
    g263: BSplineCurve PolesCount=4 KnotsCount=2 Degree=3 IsPeriodic=0
    g264: BSplineCurve PolesCount=4 KnotsCount=2 Degree=3 IsPeriodic=0
    g265: BSplineCurve PolesCount=4 KnotsCount=2 Degree=3 IsPeriodic=0
    g266: BSplineCurve PolesCount=4 KnotsCount=2 Degree=3 IsPeriodic=0
    g267: BSplineCurve PolesCount=4 KnotsCount=2 Degree=3 IsPeriodic=0
    g268: BSplineCurve PolesCount=4 KnotsCount=2 Degree=3 IsPeriodic=0
    g269: BSplineCurve PolesCount=4 KnotsCount=2 Degree=3 IsPeriodic=0
    g270: BSplineCurve PolesCount=4 KnotsCount=2 Degree=3 IsPeriodic=0
    g271: BSplineCurve PolesCount=4 KnotsCount=2 Degree=3 IsPeriodic=0
    g272: BSplineCurve PolesCount=4 KnotsCount=2 Degree=3 IsPeriodic=0
    g273: BSplineCurve PolesCount=4 KnotsCount=2 Degree=3 IsPeriodic=0
    g274: BSplineCurve PolesCount=4 KnotsCount=2 Degree=3 IsPeriodic=0
    g275: BSplineCurve PolesCount=4 KnotsCount=2 Degree=3 IsPeriodic=0
    g276: BSplineCurve PolesCount=4 KnotsCount=2 Degree=3 IsPeriodic=0
    g277: BSplineCurve PolesCount=4 KnotsCount=2 Degree=3 IsPeriodic=0
    g278: LineSegment StartX=-22.7835 StartY=52.5803 StartZ=0 EndX=-24.7911 EndY=49.0325 EndZ=0
    g279: LineSegment StartX=-24.7628 StartY=52.0337 StartZ=0 EndX=-26.2775 EndY=49.1697 EndZ=0
    g280: ArcOfCircle CenterX=-26.9498 CenterY=49.5253 CenterZ=0 NormalX=0 NormalY=0 NormalZ=1 AngleXU=0 Radius=0.760523 StartAngle=4.84877 EndAngle=5.7967
    g281: ArcOfCircle CenterX=-25.03 CenterY=52.1751 CenterZ=0 NormalX=0 NormalY=0 NormalZ=1 AngleXU=0 Radius=0.302288 StartAngle=5.7967 EndAngle=8.02385
  constraints (281):
    c: Coincident(g0,g1)
    c: Coincident(g1,g2)
    c: Coincident(g2,g3)
    c: Coincident(g3,g4)
    c: Coincident(g4,g5)
    c: Coincident(g5,g6)
    c: Coincident(g6,g7)
    c: Coincident(g7,g8)
    c: Coincident(g8,g9)
    c: Coincident(g9,g10)
    c: Coincident(g10,g11)
    c: Coincident(g11,g12)
    c: Coincident(g12,g13)
    c: Coincident(g13,g14)
    c: Coincident(g14,g15)
    c: Coincident(g15,g16)
    c: Coincident(g16,g17)
    c: Coincident(g17,g18)
    c: Coincident(g18,g19)
    c: Coincident(g19,g20)
    c: Coincident(g20,g21)
    c: Coincident(g21,g22)
    c: Coincident(g22,g23)
    c: Coincident(g23,g24)
    c: Coincident(g24,g25)
    c: Coincident(g25,g26)
    c: Coincident(g26,g27)
    c: Coincident(g27,g28)
    c: Coincident(g28,g29)
    c: Coincident(g29,g30)
    c: Coincident(g30,g31)
    c: Coincident(g31,g32)
    c: Coincident(g32,g33)
    c: Coincident(g33,g34)
    c: Coincident(g34,g35)
    c: Coincident(g35,g36)
    c: Coincident(g36,g37)
    c: Coincident(g37,g38)
    c: Coincident(g38,g39)
    c: Coincident(g39,g40)
    c: Coincident(g40,g41)
    c: Coincident(g41,g42)
    c: Coincident(g42,g43)
    c: Coincident(g43,g44)
    c: Coincident(g44,g45)
    c: Coincident(g45,g46)
    c: Coincident(g46,g47)
    c: Coincident(g47,g48)
    c: Coincident(g48,g49)
    c: Coincident(g49,g50)
    c: Coincident(g50,g51)
    c: Coincident(g51,g52)
    c: Coincident(g52,g53)
    c: Coincident(g53,g54)
    c: Coincident(g54,g55)
    c: Coincident(g55,g56)
    c: Coincident(g56,g57)
    c: Coincident(g57,g58)
    c: Coincident(g58,g59)
    c: Coincident(g59,g60)
    c: Coincident(g61,g62)
    c: Coincident(g63,g64)
    c: Coincident(g64,g65)
    c: Coincident(g65,g66)
    c: Coincident(g66,g67)
    c: Coincident(g67,g68)
    c: Coincident(g68,g69)
    c: Coincident(g69,g70)
    c: Coincident(g70,g71)
    c: Coincident(g71,g72)
    c: Coincident(g72,g73)
    c: Coincident(g73,g74)
    c: Coincident(g74,g75)
    c: Coincident(g75,g76)
    c: Coincident(g76,g77)
    c: Coincident(g77,g78)
    c: Coincident(g78,g79)
    c: Coincident(g79,g80)
    c: Coincident(g80,g81)
    c: Coincident(g81,g82)
    c: Coincident(g82,g83)
    c: Coincident(g83,g84)
    c: Coincident(g84,g85)
    c: Coincident(g85,g86)
    c: Coincident(g86,g61)
    c: Coincident(g87,g88)
    c: Coincident(g88,g89)
    c: Coincident(g89,g90)
    c: Coincident(g90,g91)
    c: Coincident(g91,g92)
    c: Coincident(g92,g93)
    c: Coincident(g93,g94)
    c: Coincident(g94,g95)
    c: Coincident(g95,g96)
    c: Coincident(g96,g97)
    c: Coincident(g97,g98)
    c: Coincident(g98,g99)
    c: Coincident(g99,g100)
    c: Coincident(g100,g101)
    c: Coincident(g101,g102)
    c: Coincident(g102,g103)
    c: Coincident(g103,g104)
    c: Coincident(g104,g105)
    c: Coincident(g105,g106)
    c: Coincident(g106,g107)
    c: Coincident(g107,g108)
    c: Coincident(g109,g110)
    c: Coincident(g110,g111)
    c: Coincident(g111,g112)
    c: Coincident(g112,g113)
    c: Coincident(g113,g114)
    c: Coincident(g114,g115)
    c: Coincident(g115,g116)
    c: Coincident(g116,g117)
    c: Coincident(g117,g118)
    c: Coincident(g118,g119)
    c: Coincident(g119,g120)
    c: Coincident(g120,g121)
    c: Coincident(g121,g122)
    c: Coincident(g122,g123)
    c: Coincident(g123,g124)
    c: Coincident(g124,g125)
    c: Coincident(g125,g126)
    c: Coincident(g126,g127)
    c: Coincident(g127,g128)
    c: Coincident(g128,g129)
    c: Coincident(g129,g130)
    c: Coincident(g130,g131)
    c: Coincident(g131,g132)
    c: Coincident(g132,g133)
    c: Coincident(g133,g134)
    c: Coincident(g134,g135)
    c: Coincident(g135,g136)
    c: Coincident(g136,g137)
    c: Coincident(g137,g138)
    c: Coincident(g138,g139)
    c: Coincident(g139,g140)
    c: Coincident(g140,g141)
    c: Coincident(g141,g142)
    c: Coincident(g142,g143)
    c: Coincident(g143,g144)
    c: Coincident(g144,g145)
    c: Coincident(g145,g146)
    c: Coincident(g146,g147)
    c: Coincident(g147,g148)
    c: Coincident(g148,g149)
    c: Coincident(g149,g150)
    c: Coincident(g150,g151)
    c: Coincident(g151,g152)
    c: Coincident(g152,g109)
    c: Coincident(g153,g154)
    c: Coincident(g154,g155)
    c: Coincident(g155,g156)
    c: Coincident(g156,g157)
    c: Coincident(g157,g158)
    c: Coincident(g158,g159)
    c: Coincident(g159,g160)
    c: Coincident(g160,g161)
    c: Coincident(g161,g162)
    c: Coincident(g162,g163)
    c: Coincident(g163,g164)
    c: Coincident(g164,g165)
    c: Coincident(g165,g166)
    c: Coincident(g166,g167)
    c: Coincident(g167,g168)
    c: Coincident(g168,g169)
    c: Coincident(g169,g170)
    c: Coincident(g170,g171)
    c: Coincident(g171,g172)
    c: Coincident(g172,g173)
    c: Coincident(g173,g174)
    c: Coincident(g174,g175)
    c: Coincident(g175,g176)
    c: Coincident(g176,g177)
    c: Coincident(g177,g178)
    c: Coincident(g178,g179)
    c: Coincident(g179,g180)
    c: Coincident(g180,g181)
    c: Coincident(g181,g182)
    c: Coincident(g182,g183)
    c: Coincident(g183,g184)
    c: Coincident(g184,g185)
    c: Coincident(g185,g186)
    c: Coincident(g186,g187)
    c: Coincident(g187,g188)
    c: Coincident(g188,g189)
    c: Coincident(g189,g190)
    c: Coincident(g190,g191)
    c: Coincident(g191,g192)
    c: Coincident(g192,g193)
    c: Coincident(g193,g194)
    c: Coincident(g194,g195)
    c: Coincident(g195,g196)
    c: Coincident(g196,g197)
    c: Coincident(g197,g198)
    c: Coincident(g198,g199)
    c: Coincident(g199,g200)
    c: Coincident(g200,g201)
    c: Coincident(g201,g202)
    c: Coincident(g202,g203)
    c: Coincident(g203,g204)
    c: Coincident(g204,g205)
    c: Coincident(g205,g206)
    c: Coincident(g206,g207)
    c: Coincident(g207,g208)
    c: Coincident(g208,g209)
    c: Coincident(g209,g153)
    c: Coincident(g210,g211)
    c: Coincident(g211,g212)
    c: Coincident(g212,g213)
    c: Coincident(g213,g214)
    c: Coincident(g214,g215)
    c: Coincident(g215,g216)
    c: Coincident(g216,g217)
    c: Coincident(g217,g218)
    c: Coincident(g218,g219)
    c: Coincident(g219,g220)
    c: Coincident(g220,g221)
    c: Coincident(g221,g222)
    c: Coincident(g222,g223)
    c: Coincident(g223,g224)
    c: Coincident(g224,g225)
    c: Coincident(g225,g226)
    c: Coincident(g226,g227)
    c: Coincident(g227,g228)
    c: Coincident(g228,g229)
    c: Coincident(g229,g230)
    c: Coincident(g230,g231)
    c: Coincident(g231,g232)
    c: Coincident(g232,g233)
    c: Coincident(g233,g234)
    c: Coincident(g234,g235)
    c: Coincident(g235,g236)
    c: Coincident(g236,g237)
    c: Coincident(g237,g238)
    c: Coincident(g238,g239)
    c: Coincident(g239,g240)
    c: Coincident(g240,g241)
    c: Coincident(g241,g242)
    c: Coincident(g242,g243)
    c: Coincident(g243,g244)
    c: Coincident(g244,g245)
    c: Coincident(g245,g246)
    c: Coincident(g246,g247)
    c: Coincident(g247,g248)
    c: Coincident(g248,g210)
    c: Coincident(g249,g250)
    c: Coincident(g250,g251)
    c: Coincident(g251,g252)
    c: Coincident(g252,g253)
    c: Coincident(g253,g254)
    c: Coincident(g254,g255)
    c: Coincident(g255,g256)
    c: Coincident(g256,g257)
    c: Coincident(g257,g258)
    c: Coincident(g258,g259)
    c: Coincident(g259,g260)
    c: Coincident(g260,g261)
    c: Coincident(g261,g262)
    c: Coincident(g263,g264)
    c: Coincident(g264,g265)
    c: Coincident(g265,g266)
    c: Coincident(g266,g267)
    c: Coincident(g267,g268)
    c: Coincident(g268,g269)
    c: Coincident(g269,g270)
    c: Coincident(g270,g271)
    c: Coincident(g271,g272)
    c: Coincident(g272,g273)
    c: Coincident(g273,g274)
    c: Coincident(g275,g276)
    c: Coincident(g276,g277)
    c: Coincident(g60,g249)
    c: Coincident(g87,g262)
    c: Coincident(g263,g108)
    c: Coincident(g278,g63)
    c: Coincident(g278,g275)
    c: Tangent(g279,g280) = 1.5708
    c: Tangent(g277,g280) = -1.5708
    c: Tangent(g279,g281) = 1.5708
    c: Coincident(g62,g281)
FEATURE [Part::FeaturePython] Scale  label="Logo_small"  # Draft clone (typed FeaturePython)
  Fuse = false
  Objects = -> [Sketch032]
  Placement = pos=(-19.0302,-16.0371,-7) rot=(0,0,1;0rad)
  Scale = (-0.5,0.5,0.5)
FEATURE [Part::Extrusion] Extrude  label="Logo_body"
  Base = -> Scale
  Dir = (0,0,1)
  DirMode = 2
  FaceMakerClass = Part::FaceMakerBullseye
  LengthFwd = 0
  LengthRev = -1
  Placement = pos=(-3.4,4,0) rot=(0,0,-1;0.349066rad)
  Solid = true
  Symmetric = false
FEATURE [PartDesign::Plane] DatumPlane  label="BasePlane"
  Length = 99.404
  ResizeMode = 0
  Width = 73.404
FEATURE [Sketcher::SketchObject] Sketch
  MapMode = 5
  Support = -> [DatumPlane]
  sketch-geometry (12):
    g0: LineSegment StartX=-35.6 StartY=29.6 StartZ=0 EndX=35.6 EndY=29.6 EndZ=0
    g1: LineSegment StartX=42.6 StartY=22.6 StartZ=0 EndX=42.6 EndY=-22.6 EndZ=0
    g2: LineSegment StartX=35.6 StartY=-29.6 StartZ=0 EndX=-35.6 EndY=-29.6 EndZ=0
    g3: LineSegment [constr] StartX=-40.5 StartY=27.5 StartZ=0 EndX=40.5 EndY=27.5 EndZ=0
    g4: LineSegment [constr] StartX=40.5 StartY=27.5 StartZ=0 EndX=40.5 EndY=-27.5 EndZ=0
    g5: LineSegment [constr] StartX=40.5 StartY=-27.5 StartZ=0 EndX=-40.5 EndY=-27.5 EndZ=0
    g6: LineSegment [constr] StartX=-40.5 StartY=-27.5 StartZ=0 EndX=-40.5 EndY=27.5 EndZ=0
    g7: LineSegment StartX=-42.6 StartY=22.6 StartZ=0 EndX=-42.6 EndY=-22.6 EndZ=0
    g8: ArcOfCircle CenterX=-35.6 CenterY=-22.6 CenterZ=0 NormalX=0 NormalY=0 NormalZ=1 AngleXU=0 Radius=7 StartAngle=3.14159 EndAngle=4.71239
    g9: ArcOfCircle CenterX=35.6 CenterY=-22.6 CenterZ=0 NormalX=0 NormalY=0 NormalZ=1 AngleXU=0 Radius=7 StartAngle=4.71239 EndAngle=6.28319
    g10: ArcOfCircle CenterX=35.6 CenterY=22.6 CenterZ=0 NormalX=0 NormalY=0 NormalZ=1 AngleXU=0 Radius=7 StartAngle=0 EndAngle=1.5708
    g11: ArcOfCircle CenterX=-35.6 CenterY=22.6 CenterZ=0 NormalX=0 NormalY=0 NormalZ=1 AngleXU=0 Radius=7 StartAngle=1.5708 EndAngle=3.14159
  constraints (39):
    c: Coincident(g5,g6)
    c: Coincident(g3,g6)
    c: Coincident(g4,g5)
    c: Coincident(g3,g4)
    c: Horizontal(g0)
    c: Horizontal(g2)
    c: Vertical(g1)
    c: Vertical(g7)
    c: DistanceX(g3,g3) = 81
    c: DistanceY(g4,g3) = 55
    c: DistanceY(g4,g-1) = 27.5
    c: Horizontal(g3)
    c: Vertical(g6)
    c: Vertical(g4)
    c: Radius(g8) = 7
    c: Coincident(g7,g8)
    c: Coincident(g8,g2)
    c: DistanceY(g2,g7) = 7
    c: DistanceX(g7,g2) = 7
    c: Equal(g8,g9) = 7
    c: DistanceY(g2,g5) = 2.1
    c: Coincident(g2,g9)
    c: Coincident(g1,g9)
    c: DistanceY(g2,g1) = 7
    c: DistanceX(g2,g1) = 7
    c: Coincident(g0,g10)
    c: Coincident(g1,g10)
    c: Equal(g10,g9)
    c: DistanceY(g1,g0) = 7
    c: DistanceX(g0,g1) = 7
    c: Coincident(g11,g7)
    c: Coincident(g11,g0)
    c: Equal(g0,g2)
    c: Equal(g7,g1)
    c: DistanceX(g7,g3) = 2.1
    c: DistanceX(g3,g1) = 2.1
    c: DistanceY(g3,g0) = 2.1
    c: Equal(g11,g8)
    c: Symmetric(g5,g3,g-1)
FEATURE [PartDesign::Pad] Pad  label="top_box"
  Length = 13
  Length2 = 1
  Profile = -> Sketch
  Refine = true
  Type = 4
FEATURE [Sketcher::SketchObject] Sketch008  label="BoxCut"
  AttachmentOffset = pos=(0,0,0.6) rot=(0,0,1;0rad)
  ExternalGeometry = -> [Pad]
  MapMode = 5
  Placement = pos=(0,0,0.6) rot=(0,0,1;0rad)
  Support = -> [DatumPlane]
  sketch-geometry (8):
    g0: LineSegment StartX=-35.6 StartY=28 StartZ=0 EndX=35.6 EndY=28 EndZ=0
    g1: ArcOfCircle CenterX=35.6 CenterY=22.6 CenterZ=0 NormalX=0 NormalY=0 NormalZ=1 AngleXU=0 Radius=5.4 StartAngle=1e-16 EndAngle=1.5708
    g2: LineSegment StartX=41 StartY=22.6 StartZ=0 EndX=41 EndY=-22.6 EndZ=0
    g3: LineSegment StartX=35.6 StartY=-28 StartZ=0 EndX=-35.6 EndY=-28 EndZ=0
    g4: ArcOfCircle CenterX=-35.6 CenterY=-22.6 CenterZ=0 NormalX=0 NormalY=0 NormalZ=1 AngleXU=0 Radius=5.4 StartAngle=3.14159 EndAngle=4.71239
    g5: LineSegment StartX=-41 StartY=-22.6 StartZ=0 EndX=-41 EndY=22.6 EndZ=0
    g6: ArcOfCircle CenterX=-35.6 CenterY=22.6 CenterZ=0 NormalX=0 NormalY=0 NormalZ=1 AngleXU=0 Radius=5.4 StartAngle=1.5708 EndAngle=3.14159
    g7: ArcOfCircle CenterX=35.6 CenterY=-22.6 CenterZ=0 NormalX=0 NormalY=0 NormalZ=1 AngleXU=0 Radius=5.4 StartAngle=4.71239 EndAngle=6.28318
  constraints (19):
    c: Horizontal(g0)
    c: Tangent(g0,g1) = 1.5708
    c: Tangent(g1,g2) = 1.5708
    c: Tangent(g3,g4) = 1.5708
    c: Tangent(g4,g5) = 1.5708
    c: Tangent(g5,g6) = 1.5708
    c: Coincident(g6,g0)
    c: Coincident(g6,g-4)
    c: Coincident(g1,g-10)
    c: Coincident(g4,g-6)
    c: Vertical(g5)
    c: Horizontal(g3)
    c: DistanceY(g0,g-4) = 1.6
    c: Vertical(g2)
    c: Tangent(g0,g6,g0) = 1.5708
    c: Equal(g4,g7)
    c: Coincident(g7,g2)
    c: Coincident(g7,g3)
    c: Coincident(g-8,g7)
FEATURE [PartDesign::Pocket] Pocket  label="top_box_cut"
  BaseFeature = -> Pad
  Length = 15
  Length2 = 100
  Profile = -> Sketch008
  Refine = true
  Reversed = true
  Type = 0
FEATURE [Sketcher::SketchObject] Sketch009  label="EdgePCBHolder001"
  ExternalGeometry = -> [Pad]
  MapMode = 5
  Support = -> [DatumPlane]
  sketch-geometry (7):
    g0: LineSegment StartX=38 StartY=-21.6 StartZ=0 EndX=42.5889 EndY=-21.6 EndZ=0
    g1: ArcOfCircle CenterX=38 CenterY=-25 CenterZ=0 NormalX=0 NormalY=0 NormalZ=1 AngleXU=0 Radius=3.4 StartAngle=1.5708 EndAngle=3.14159
    g2: Circle CenterX=38 CenterY=-25 CenterZ=0 NormalX=0 NormalY=0 NormalZ=1 AngleXU=0 Radius=1.4
    g3: LineSegment StartX=34.6 StartY=-29.6 StartZ=0 EndX=34.6 EndY=-25 EndZ=0
    g4: LineSegment StartX=34.6 StartY=-29.6 StartZ=0 EndX=35.6 EndY=-29.6 EndZ=0
    g5: LineSegment StartX=42.5889 StartY=-21.6 StartZ=0 EndX=42.5889 EndY=-22.9936 EndZ=0
    g6: ArcOfCircle CenterX=35.6 CenterY=-22.6 CenterZ=0 NormalX=0 NormalY=0 NormalZ=1 AngleXU=0 Radius=7 StartAngle=4.71239 EndAngle=6.22693
  constraints (19):
    c: Horizontal(g0)
    c: Coincident(g1,g0)
    c: Radius(g2) = 1.4
    c: DistanceY(g-10,g2) = 4.6
    c: DistanceX(g1,g0) = 0
    c: Coincident(g3,g1)
    c: Vertical(g3)
    c: DistanceY(g-10,g0) = 1
    c: DistanceY(g1,g1) = 0
    c: Coincident(g1,g2)
    c: Coincident(g4,g3)
    c: Horizontal(g4)
    c: Coincident(g5,g0)
    c: Vertical(g5)
    c: DistanceX(g4,g4) = 1
    c: Coincident(g6,g-10)
    c: Coincident(g6,g5)
    c: Coincident(g6,g4)
    c: Coincident(g4,g-10)
FEATURE [PartDesign::Pad] Pad001  label="EdgePCBHolder"
  BaseFeature = -> Pocket
  Length = 5
  Length2 = 100
  Profile = -> Sketch009
  Refine = true
  Type = 0
FEATURE [PartDesign::Mirrored] Mirrored001
  MirrorPlane = -> Sketch009 [V_Axis]
  Refine = true
FEATURE [PartDesign::Mirrored] Mirrored002
  MirrorPlane = -> Sketch009 [H_Axis]
  Refine = true
FEATURE [PartDesign::MultiTransform] MultiTransform  label="PCBHolder_2Edges001"
  BaseFeature = -> Pad001
  Originals = -> [Pad001]
  Refine = true
  Transformations = -> [Mirrored001,Mirrored002,Mirrored003]
FEATURE [PartDesign::Pocket] Pocket003  label="Aux_Holes_2"
  BaseFeature = -> MultiTransform
  Length = 5
  Length2 = 100
  Midplane = true
  Profile = -> Sketch011
  Refine = true
  Type = 0
FEATURE [PartDesign::Pocket] Pocket001  label="AuxHoles_6"
  BaseFeature = -> Pocket003
  Length = 60
  Length2 = 1
  Profile = -> Sketch002
  Refine = true
  Type = 4
FEATURE [Sketcher::SketchObject] Sketch013
  AttachmentOffset = pos=(0,0,9.55) rot=(0,0,1;0rad)
  ExternalGeometry = -> [Pad]
  MapMode = 5
  Placement = pos=(0,0,9.55) rot=(0,0,1;0rad)
  Support = -> [DatumPlane]
  sketch-geometry (12):
    g0: ArcOfCircle CenterX=35.6 CenterY=22.6 CenterZ=0 NormalX=0 NormalY=0 NormalZ=1 AngleXU=0 Radius=6.2 StartAngle=0 EndAngle=1.5708
    g1: LineSegment StartX=41.8 StartY=22.6 StartZ=0 EndX=41.8 EndY=-22.6 EndZ=0
    g2: ArcOfCircle CenterX=35.6 CenterY=-22.6 CenterZ=0 NormalX=0 NormalY=0 NormalZ=1 AngleXU=0 Radius=6.2 StartAngle=4.71239 EndAngle=6.28319
    g3: LineSegment StartX=35.6 StartY=-28.8 StartZ=0 EndX=-35.6 EndY=-28.8 EndZ=0
    g4: LineSegment StartX=35.6 StartY=28.8 StartZ=0 EndX=-11.6 EndY=28.8 EndZ=0
    g5: LineSegment StartX=-24.6 StartY=23.8 StartZ=0 EndX=-11.6 EndY=23.8 EndZ=0
    g6: LineSegment StartX=-11.6 StartY=28.8 StartZ=0 EndX=-11.6 EndY=23.8 EndZ=0
    g7: LineSegment StartX=-24.6 StartY=23.8 StartZ=0 EndX=-24.6 EndY=28.8 EndZ=0
    g8: LineSegment StartX=-24.6 StartY=28.8 StartZ=0 EndX=-35.6 EndY=28.8 EndZ=0
    g9: LineSegment StartX=-41.8 StartY=-22.6 StartZ=0 EndX=-41.8 EndY=22.6 EndZ=0
    g10: ArcOfCircle CenterX=-35.6 CenterY=-22.6 CenterZ=0 NormalX=0 NormalY=0 NormalZ=1 AngleXU=0 Radius=6.2 StartAngle=3.14159 EndAngle=4.71239
    g11: ArcOfCircle CenterX=-35.6 CenterY=22.6 CenterZ=0 NormalX=0 NormalY=0 NormalZ=1 AngleXU=0 Radius=6.2 StartAngle=1.5708 EndAngle=3.14159
  constraints (34):
    c: Tangent(g0,g1) = 1.5708
    c: Tangent(g1,g2) = 1.5708
    c: Coincident(g2,g-5)
    c: Coincident(g-7,g0)
    c: Coincident(g3,g2)
    c: Horizontal(g3)
    c: Coincident(g4,g0)
    c: Horizontal(g4)
    c: Horizontal(g5)
    c: Coincident(g5,g6)
    c: Coincident(g4,g6)
    c: Vertical(g6)
    c: DistanceY(g0,g-7) = 0.8
    c: Vertical(g2,g-5)
    c: Vertical(g-5,g0)
    c: DistanceX(g5,g5) = 13
    c: Coincident(g5,g7)
    c: Vertical(g7)
    c: Coincident(g7,g8)
    c: Horizontal(g8)
    c: Vertical(g9)
    c: Coincident(g10,g-9)
    c: Coincident(g9,g10)
    c: Coincident(g10,g3)
    c: Vertical(g1)
    c: Horizontal(g9,g-9)
    c: Vertical(g3,g-9)
    c: Coincident(g11,g-8)
    c: Coincident(g11,g8)
    c: Coincident(g11,g9)
    c: Horizontal(g-8,g9)
    c: Vertical(g8,g-8)
    c: DistanceY(g7,g7) = 5
    c: DistanceX(g8,g7) = 11
FEATURE [PartDesign::Pocket] Pocket005  label="MountingEdge"
  BaseFeature = -> Pocket001
  Length = 0.5
  Length2 = 12
  Profile = -> Sketch013
  Refine = true
  Reversed = true
  Type = 4
FEATURE [Sketcher::SketchObject] Sketch046  label="aboveAuxCut1"
  AttachmentOffset = pos=(0,0,9.55) rot=(0,0,1;0rad)
  ExternalGeometry = -> [Pocket005]
  MapMode = 5
  Placement = pos=(0,0,9.55) rot=(0,0,1;0rad)
  Support = -> [DatumPlane]
  sketch-geometry (8):
    g0: LineSegment StartX=48.4 StartY=29.6 StartZ=0 EndX=48.4 EndY=-30.4 EndZ=0
    g1: LineSegment StartX=-45.6 StartY=-30.4 StartZ=0 EndX=-45.6 EndY=29.6 EndZ=0
    g2: LineSegment StartX=-45.6 StartY=-30.4 StartZ=0 EndX=48.4 EndY=-30.4 EndZ=0
    g3: LineSegment StartX=-45.6 StartY=29.6 StartZ=0 EndX=-24.6 EndY=29.6 EndZ=0
    g4: LineSegment StartX=-24.6 StartY=29.6 StartZ=0 EndX=-24.6 EndY=24.6 EndZ=0
    g5: LineSegment StartX=-24.6 StartY=24.6 StartZ=0 EndX=-11.6 EndY=24.6 EndZ=0
    g6: LineSegment StartX=-11.6 StartY=24.6 StartZ=0 EndX=-11.6 EndY=29.6 EndZ=0
    g7: LineSegment StartX=-11.6 StartY=29.6 StartZ=0 EndX=48.4 EndY=29.6 EndZ=0
  constraints (24):
    c: Vertical(g0)
    c: Horizontal(g1,g-3)
    c: Vertical(g1)
    c: Coincident(g2,g0)
    c: Horizontal(g2)
    c: Coincident(g1,g2)
    c: Coincident(g1,g3)
    c: Horizontal(g3)
    c: Coincident(g3,g4)
    c: Vertical(g4)
    c: Coincident(g4,g5)
    c: Horizontal(g5)
    c: Coincident(g5,g6)
    c: Vertical(g6)
    c: Coincident(g6,g7)
    c: Horizontal(g7)
    c: Coincident(g0,g7)
    c: Horizontal(g1,g6)
    c: DistanceX(g-3,g4) = 11
    c: DistanceX(g5,g5) = 13
    c: DistanceY(g4,g4) = 5
    c: DistanceX(g1,g-3) = 10
    c: DistanceX(g7,g7) = 60
    c: DistanceY(g0,g0) = 60
FEATURE [PartDesign::Pocket] Pocket019  label="aboveAuxCut"
  BaseFeature = -> Pocket005
  Length = 5.5
  Length2 = 100
  Profile = -> Sketch046
  Refine = true
  Reversed = true
  Type = 0
FEATURE [Sketcher::SketchObject] Sketch051
  MapMode = 5
  Placement = pos=(0,-29.6,0) rot=(1,0,0;1.5708rad)
  sketch-geometry (4):
    g0: LineSegment StartX=-22.6 StartY=7.65 StartZ=0 EndX=-13.6 EndY=7.65 EndZ=0
    g1: LineSegment StartX=-13.6 StartY=7.65 StartZ=0 EndX=-13.6 EndY=5.65 EndZ=0
    g2: LineSegment StartX=-13.6 StartY=5.65 StartZ=0 EndX=-22.6 EndY=5.65 EndZ=0
    g3: LineSegment StartX=-22.6 StartY=5.65 StartZ=0 EndX=-22.6 EndY=7.65 EndZ=0
  constraints (10):
    c: Coincident(g0,g1)
    c: Coincident(g1,g2)
    c: Coincident(g2,g3)
    c: Coincident(g3,g0)
    c: Horizontal(g0)
    c: Horizontal(g2)
    c: Vertical(g1)
    c: Vertical(g3)
    c: DistanceX(g2,g2) = 9
    c: DistanceY(g3,g3) = 2
FEATURE [PartDesign::Pocket] Pocket024  label="USB_cut"
  BaseFeature = -> Pocket012
  Length = 5
  Length2 = 100
  Profile = -> Sketch051
  Refine = true
  Type = 0
FEATURE [PartDesign::Pad] Pad002  label="EdgePCBHolder003"
  BaseFeature = -> Pocket024
  Length = 12.55
  Length2 = 4.2
  Profile = -> Sketch019
  Refine = true
  Type = 4
FEATURE [Part::Part2DObjectPython] ShapeString  # Draft 2D object (typed FeaturePython)
  FontFile = <path>
  Placement = pos=(31.0419,-30,13.5452) rot=(0,0.707107,-0.707107;3.14159rad)
  Size = 2.5
  String = 4 5 6 7 8
  Tracking = 2.5
FEATURE [Sketcher::SketchObject] Sketch057  label="45678"
  AttachmentOffset = pos=(0,14,0) rot=(0,0,1;3.14159rad)
  MapMode = 5
  Placement = pos=(0,29.6,14) rot=(-1,0,0;1.5708rad)
  sketch-geometry (119):
    g0: BSplineCurve PolesCount=3 KnotsCount=2 Degree=2 IsPeriodic=0
    g1: BSplineCurve PolesCount=3 KnotsCount=2 Degree=2 IsPeriodic=0
    g2: BSplineCurve PolesCount=3 KnotsCount=2 Degree=2 IsPeriodic=0
    g3: BSplineCurve PolesCount=3 KnotsCount=2 Degree=2 IsPeriodic=0
    g4: BSplineCurve PolesCount=3 KnotsCount=2 Degree=2 IsPeriodic=0
    g5: BSplineCurve PolesCount=3 KnotsCount=2 Degree=2 IsPeriodic=0
    g6: BSplineCurve PolesCount=3 KnotsCount=2 Degree=2 IsPeriodic=0
    g7: BSplineCurve PolesCount=3 KnotsCount=2 Degree=2 IsPeriodic=0
    g8: BSplineCurve PolesCount=3 KnotsCount=2 Degree=2 IsPeriodic=0
    g9: BSplineCurve PolesCount=3 KnotsCount=2 Degree=2 IsPeriodic=0
    g10: BSplineCurve PolesCount=3 KnotsCount=2 Degree=2 IsPeriodic=0
    g11: BSplineCurve PolesCount=3 KnotsCount=2 Degree=2 IsPeriodic=0
    g12: BSplineCurve PolesCount=3 KnotsCount=2 Degree=2 IsPeriodic=0
    g13: BSplineCurve PolesCount=3 KnotsCount=2 Degree=2 IsPeriodic=0
    g14: BSplineCurve PolesCount=3 KnotsCount=2 Degree=2 IsPeriodic=0
    g15: BSplineCurve PolesCount=3 KnotsCount=2 Degree=2 IsPeriodic=0
    g16: BSplineCurve PolesCount=3 KnotsCount=2 Degree=2 IsPeriodic=0
    g17: BSplineCurve PolesCount=3 KnotsCount=2 Degree=2 IsPeriodic=0
    g18: BSplineCurve PolesCount=3 KnotsCount=2 Degree=2 IsPeriodic=0
    g19: BSplineCurve PolesCount=3 KnotsCount=2 Degree=2 IsPeriodic=0
    g20: BSplineCurve PolesCount=3 KnotsCount=2 Degree=2 IsPeriodic=0
    g21: BSplineCurve PolesCount=3 KnotsCount=2 Degree=2 IsPeriodic=0
    g22: BSplineCurve PolesCount=3 KnotsCount=2 Degree=2 IsPeriodic=0
    g23: BSplineCurve PolesCount=3 KnotsCount=2 Degree=2 IsPeriodic=0
    g24: BSplineCurve PolesCount=3 KnotsCount=2 Degree=2 IsPeriodic=0
    g25: BSplineCurve PolesCount=3 KnotsCount=2 Degree=2 IsPeriodic=0
    g26: BSplineCurve PolesCount=3 KnotsCount=2 Degree=2 IsPeriodic=0
    g27: BSplineCurve PolesCount=3 KnotsCount=2 Degree=2 IsPeriodic=0
    g28: BSplineCurve PolesCount=3 KnotsCount=2 Degree=2 IsPeriodic=0
    g29: LineSegment StartX=27.9341 StartY=13.5452 StartZ=0 EndX=28.8653 EndY=13.5452 EndZ=0
    g30: BSplineCurve PolesCount=3 KnotsCount=2 Degree=2 IsPeriodic=0
    g31: BSplineCurve PolesCount=3 KnotsCount=2 Degree=2 IsPeriodic=0
    g32: LineSegment StartX=27.8929 StartY=12.5727 StartZ=0 EndX=27.8929 EndY=12.841 EndZ=0
    g33: BSplineCurve PolesCount=3 KnotsCount=2 Degree=2 IsPeriodic=0
    g34: BSplineCurve PolesCount=3 KnotsCount=2 Degree=2 IsPeriodic=0
    g35: LineSegment StartX=27.8929 StartY=9.16215 StartZ=0 EndX=27.8929 EndY=11.8686 EndZ=0
    g36: LineSegment StartX=28.8149 StartY=9.16215 StartZ=0 EndX=27.8929 EndY=9.16215 EndZ=0
    g37: LineSegment StartX=30.5144 StartY=11.9878 StartZ=0 EndX=28.8149 EndY=9.16215 EndZ=0
    g38: LineSegment StartX=30.5144 StartY=12.5727 StartZ=0 EndX=30.5144 EndY=11.9878 EndZ=0
    g39: LineSegment StartX=28.597 StartY=12.5727 StartZ=0 EndX=30.5144 EndY=12.5727 EndZ=0
    g40: LineSegment StartX=28.597 StartY=12.841 StartZ=0 EndX=28.597 EndY=12.5727 EndZ=0
    g41: LineSegment StartX=28.8653 StartY=12.841 StartZ=0 EndX=28.597 EndY=12.841 EndZ=0
    g42: BSplineCurve PolesCount=3 KnotsCount=2 Degree=2 IsPeriodic=0
    g43: LineSegment StartX=28.597 StartY=11.8686 StartZ=0 EndX=28.597 EndY=10.1621 EndZ=0
    g44: LineSegment StartX=29.6543 StartY=11.8686 StartZ=0 EndX=28.597 EndY=11.8686 EndZ=0
    g45: LineSegment StartX=28.597 StartY=10.1621 StartZ=0 EndX=29.6543 EndY=11.8686 EndZ=0
    g46: BSplineCurve PolesCount=3 KnotsCount=2 Degree=2 IsPeriodic=0
    g47: BSplineCurve PolesCount=3 KnotsCount=2 Degree=2 IsPeriodic=0
    g48: BSplineCurve PolesCount=3 KnotsCount=2 Degree=2 IsPeriodic=0
    g49: LineSegment StartX=16.6887 StartY=9.16215 StartZ=0 EndX=14.5626 EndY=9.16215 EndZ=0
    g50: LineSegment StartX=16.6887 StartY=11.1644 StartZ=0 EndX=16.6887 EndY=9.16215 EndZ=0
    g51: BSplineCurve PolesCount=3 KnotsCount=2 Degree=2 IsPeriodic=0
    g52: BSplineCurve PolesCount=3 KnotsCount=2 Degree=2 IsPeriodic=0
    g53: BSplineCurve PolesCount=3 KnotsCount=2 Degree=2 IsPeriodic=0
    g54: BSplineCurve PolesCount=3 KnotsCount=2 Degree=2 IsPeriodic=0
    g55: BSplineCurve PolesCount=3 KnotsCount=2 Degree=2 IsPeriodic=0
    g56: BSplineCurve PolesCount=3 KnotsCount=2 Degree=2 IsPeriodic=0
    g57: BSplineCurve PolesCount=3 KnotsCount=2 Degree=2 IsPeriodic=0
    g58: BSplineCurve PolesCount=3 KnotsCount=2 Degree=2 IsPeriodic=0
    g59: BSplineCurve PolesCount=3 KnotsCount=2 Degree=2 IsPeriodic=0
    g60: BSplineCurve PolesCount=3 KnotsCount=2 Degree=2 IsPeriodic=0
    g61: BSplineCurve PolesCount=3 KnotsCount=2 Degree=2 IsPeriodic=0
    g62: BSplineCurve PolesCount=3 KnotsCount=2 Degree=2 IsPeriodic=0
    g63: BSplineCurve PolesCount=3 KnotsCount=2 Degree=2 IsPeriodic=0
    g64: BSplineCurve PolesCount=3 KnotsCount=2 Degree=2 IsPeriodic=0
    g65: BSplineCurve PolesCount=3 KnotsCount=2 Degree=2 IsPeriodic=0
    g66: BSplineCurve PolesCount=3 KnotsCount=2 Degree=2 IsPeriodic=0
    g67: BSplineCurve PolesCount=3 KnotsCount=2 Degree=2 IsPeriodic=0
    g68: BSplineCurve PolesCount=3 KnotsCount=2 Degree=2 IsPeriodic=0
    g69: BSplineCurve PolesCount=3 KnotsCount=2 Degree=2 IsPeriodic=0
    g70: BSplineCurve PolesCount=3 KnotsCount=2 Degree=2 IsPeriodic=0
    g71: BSplineCurve PolesCount=3 KnotsCount=2 Degree=2 IsPeriodic=0
    g72: BSplineCurve PolesCount=3 KnotsCount=2 Degree=2 IsPeriodic=0
    g73: BSplineCurve PolesCount=3 KnotsCount=2 Degree=2 IsPeriodic=0
    g74: BSplineCurve PolesCount=3 KnotsCount=2 Degree=2 IsPeriodic=0
    g75: LineSegment StartX=15.9846 StartY=9.86628 StartZ=0 EndX=15.9846 EndY=10.6782 EndZ=0
    g76: LineSegment StartX=14.5626 StartY=9.86628 StartZ=0 EndX=15.9846 EndY=9.86628 EndZ=0
    g77: BSplineCurve PolesCount=3 KnotsCount=2 Degree=2 IsPeriodic=0
    g78: BSplineCurve PolesCount=3 KnotsCount=2 Degree=2 IsPeriodic=0
    g79: BSplineCurve PolesCount=3 KnotsCount=2 Degree=2 IsPeriodic=0
    g80: BSplineCurve PolesCount=3 KnotsCount=2 Degree=2 IsPeriodic=0
    g81: BSplineCurve PolesCount=3 KnotsCount=2 Degree=2 IsPeriodic=0
    g82: BSplineCurve PolesCount=3 KnotsCount=2 Degree=2 IsPeriodic=0
    g83: BSplineCurve PolesCount=3 KnotsCount=2 Degree=2 IsPeriodic=0
    g84: BSplineCurve PolesCount=3 KnotsCount=2 Degree=2 IsPeriodic=0
    g85: BSplineCurve PolesCount=3 KnotsCount=2 Degree=2 IsPeriodic=0
    g86: BSplineCurve PolesCount=3 KnotsCount=2 Degree=2 IsPeriodic=0
    g87: BSplineCurve PolesCount=3 KnotsCount=2 Degree=2 IsPeriodic=0
    g88: BSplineCurve PolesCount=3 KnotsCount=2 Degree=2 IsPeriodic=0
    g89: BSplineCurve PolesCount=3 KnotsCount=2 Degree=2 IsPeriodic=0
    g90: BSplineCurve PolesCount=3 KnotsCount=2 Degree=2 IsPeriodic=0
    g91: BSplineCurve PolesCount=3 KnotsCount=2 Degree=2 IsPeriodic=0
    g92: BSplineCurve PolesCount=3 KnotsCount=2 Degree=2 IsPeriodic=0
    g93: BSplineCurve PolesCount=3 KnotsCount=2 Degree=2 IsPeriodic=0
    g94: BSplineCurve PolesCount=3 KnotsCount=2 Degree=2 IsPeriodic=0
    g95: BSplineCurve PolesCount=3 KnotsCount=2 Degree=2 IsPeriodic=0
    g96: BSplineCurve PolesCount=3 KnotsCount=2 Degree=2 IsPeriodic=0
    g97: BSplineCurve PolesCount=3 KnotsCount=2 Degree=2 IsPeriodic=0
    g98: BSplineCurve PolesCount=3 KnotsCount=2 Degree=2 IsPeriodic=0
    g99: BSplineCurve PolesCount=3 KnotsCount=2 Degree=2 IsPeriodic=0
    g100: BSplineCurve PolesCount=3 KnotsCount=2 Degree=2 IsPeriodic=0
    g101: BSplineCurve PolesCount=3 KnotsCount=2 Degree=2 IsPeriodic=0
    g102: BSplineCurve PolesCount=3 KnotsCount=2 Degree=2 IsPeriodic=0
    g103: BSplineCurve PolesCount=3 KnotsCount=2 Degree=2 IsPeriodic=0
    g104: BSplineCurve PolesCount=3 KnotsCount=2 Degree=2 IsPeriodic=0
    g105: BSplineCurve PolesCount=3 KnotsCount=2 Degree=2 IsPeriodic=0
    g106: BSplineCurve PolesCount=3 KnotsCount=2 Degree=2 IsPeriodic=0
    g107: BSplineCurve PolesCount=3 KnotsCount=2 Degree=2 IsPeriodic=0
    g108: LineSegment StartX=-12.3388 StartY=9.86628 StartZ=0 EndX=-10.7333 EndY=9.86628 EndZ=0
    g109: LineSegment StartX=-11.2815 StartY=12.9741 StartZ=0 EndX=-12.3388 EndY=9.86628 EndZ=0
    g110: BSplineCurve PolesCount=3 KnotsCount=2 Degree=2 IsPeriodic=0
    g111: BSplineCurve PolesCount=3 KnotsCount=2 Degree=2 IsPeriodic=0
    g112: BSplineCurve PolesCount=3 KnotsCount=2 Degree=2 IsPeriodic=0
    g113: BSplineCurve PolesCount=3 KnotsCount=2 Degree=2 IsPeriodic=0
    g114: BSplineCurve PolesCount=3 KnotsCount=2 Degree=2 IsPeriodic=0
    g115: LineSegment StartX=-13.0796 StartY=9.8594 StartZ=0 EndX=-11.9581 EndY=13.208 EndZ=0
    g116: LineSegment StartX=-13.0796 StartY=9.16215 StartZ=0 EndX=-13.0796 EndY=9.8594 EndZ=0
    g117: LineSegment StartX=-10.0269 StartY=9.16215 StartZ=0 EndX=-13.0796 EndY=9.16215 EndZ=0
    g118: LineSegment StartX=-10.0269 StartY=9.78371 StartZ=0 EndX=-10.0269 EndY=9.16215 EndZ=0
  constraints (137):
    c: Coincident(g0,g1)
    c: Coincident(g1,g2)
    c: Coincident(g2,g3)
    c: Coincident(g3,g4)
    c: Coincident(g4,g5)
    c: Coincident(g5,g6)
    c: Coincident(g6,g7)
    c: Coincident(g7,g8)
    c: Coincident(g8,g9)
    c: Coincident(g9,g10)
    c: Coincident(g10,g11)
    c: Coincident(g11,g0)
    c: Coincident(g12,g13)
    c: Coincident(g13,g14)
    c: Coincident(g14,g15)
    c: Coincident(g15,g16)
    c: Coincident(g16,g17)
    c: Coincident(g17,g18)
    c: Coincident(g18,g19)
    c: Coincident(g19,g12)
    c: Coincident(g20,g21)
    c: Coincident(g21,g22)
    c: Coincident(g22,g23)
    c: Coincident(g23,g24)
    c: Coincident(g24,g25)
    c: Coincident(g25,g26)
    c: Coincident(g26,g27)
    c: Coincident(g27,g20)
    c: Coincident(g28,g29)
    c: Horizontal(g29)
    c: Coincident(g29,g30)
    c: Coincident(g30,g31)
    c: Coincident(g31,g32)
    c: Vertical(g32)
    c: Coincident(g32,g33)
    c: Coincident(g33,g34)
    c: Coincident(g34,g35)
    c: Vertical(g35)
    c: Coincident(g35,g36)
    c: Horizontal(g36)
    c: Coincident(g36,g37)
    c: Coincident(g37,g38)
    c: Vertical(g38)
    c: Coincident(g38,g39)
    c: Horizontal(g39)
    c: Coincident(g39,g40)
    c: Vertical(g40)
    c: Coincident(g40,g41)
    c: Horizontal(g41)
    c: Coincident(g41,g42)
    c: Coincident(g42,g28)
    c: Vertical(g43)
    c: Coincident(g43,g44)
    c: Horizontal(g44)
    c: Coincident(g44,g45)
    c: Coincident(g45,g43)
    c: Coincident(g46,g47)
    c: Coincident(g47,g48)
    c: Coincident(g48,g49)
    c: Horizontal(g49)
    c: Coincident(g49,g50)
    c: Vertical(g50)
    c: Coincident(g50,g51)
    c: Coincident(g51,g52)
    c: Coincident(g52,g53)
    c: Coincident(g53,g54)
    c: Coincident(g54,g55)
    c: Coincident(g55,g56)
    c: Coincident(g56,g57)
    c: Coincident(g57,g58)
    c: Coincident(g58,g59)
    c: Coincident(g59,g60)
    c: Coincident(g60,g61)
    c: Coincident(g61,g62)
    c: Coincident(g62,g63)
    c: Coincident(g63,g64)
    c: Coincident(g64,g65)
    c: Coincident(g65,g66)
    c: Coincident(g66,g67)
    c: Coincident(g67,g68)
    c: Coincident(g68,g69)
    c: Coincident(g69,g70)
    c: Coincident(g70,g71)
    c: Coincident(g71,g72)
    c: Coincident(g72,g73)
    c: Coincident(g73,g74)
    c: Coincident(g74,g75)
    c: Vertical(g75)
    c: Coincident(g75,g76)
    c: Horizontal(g76)
    c: Coincident(g76,g46)
    c: Coincident(g77,g78)
    c: Coincident(g78,g79)
    c: Coincident(g79,g80)
    c: Coincident(g80,g81)
    c: Coincident(g81,g82)
    c: Coincident(g82,g83)
    c: Coincident(g83,g84)
    c: Coincident(g84,g85)
    c: Coincident(g85,g86)
    c: Coincident(g86,g87)
    c: Coincident(g87,g88)
    c: Coincident(g88,g89)
    c: Coincident(g89,g90)
    c: Coincident(g90,g91)
    c: Coincident(g91,g92)
    c: Coincident(g92,g93)
    c: Coincident(g93,g94)
    c: Coincident(g94,g95)
    c: Coincident(g95,g96)
    c: Coincident(g96,g97)
    c: Coincident(g97,g77)
    c: Coincident(g98,g99)
    c: Coincident(g99,g100)
    c: Coincident(g100,g101)
    c: Coincident(g101,g102)
    c: Coincident(g102,g103)
    c: Coincident(g103,g104)
    c: Coincident(g104,g105)
    c: Coincident(g105,g98)
    c: Coincident(g106,g107)
    c: Coincident(g107,g108)
    c: Horizontal(g108)
    c: Coincident(g108,g109)
    c: Coincident(g109,g110)
    c: Coincident(g110,g111)
    c: Coincident(g111,g112)
    c: Coincident(g112,g113)
    c: Coincident(g113,g114)
    c: Coincident(g114,g115)
    c: Coincident(g115,g116)
    c: Vertical(g116)
    c: Coincident(g116,g117)
    c: Horizontal(g117)
    c: Coincident(g117,g118)
    c: Vertical(g118)
    c: Coincident(g118,g106)
FEATURE [Part::Part2DObjectPython] ShapeString001  # Draft 2D object (typed FeaturePython)
  FontFile = <path>
  Placement = pos=(3.79522,30,15.0185) rot=(-1,0,0;1.5708rad)
  Size = 2.5
  String = 1 2 3
  Tracking = 2.5
FEATURE [Sketcher::SketchObject] Sketch058  label="123"
  AttachmentOffset = pos=(-4,14,0) rot=(0,0,1;0rad)
  Placement = pos=(-4,-29.6,14) rot=(1,0,0;1.5708rad)
  sketch-geometry (83):
    g0: BSplineCurve PolesCount=3 KnotsCount=2 Degree=2 IsPeriodic=0
    g1: BSplineCurve PolesCount=3 KnotsCount=2 Degree=2 IsPeriodic=0
    g2: BSplineCurve PolesCount=3 KnotsCount=2 Degree=2 IsPeriodic=0
    g3: BSplineCurve PolesCount=3 KnotsCount=2 Degree=2 IsPeriodic=0
    g4: BSplineCurve PolesCount=3 KnotsCount=2 Degree=2 IsPeriodic=0
    g5: BSplineCurve PolesCount=3 KnotsCount=2 Degree=2 IsPeriodic=0
    g6: BSplineCurve PolesCount=3 KnotsCount=2 Degree=2 IsPeriodic=0
    g7: BSplineCurve PolesCount=3 KnotsCount=2 Degree=2 IsPeriodic=0
    g8: BSplineCurve PolesCount=3 KnotsCount=2 Degree=2 IsPeriodic=0
    g9: BSplineCurve PolesCount=3 KnotsCount=2 Degree=2 IsPeriodic=0
    g10: BSplineCurve PolesCount=3 KnotsCount=2 Degree=2 IsPeriodic=0
    g11: BSplineCurve PolesCount=3 KnotsCount=2 Degree=2 IsPeriodic=0
    g12: BSplineCurve PolesCount=3 KnotsCount=2 Degree=2 IsPeriodic=0
    g13: BSplineCurve PolesCount=3 KnotsCount=2 Degree=2 IsPeriodic=0
    g14: BSplineCurve PolesCount=3 KnotsCount=2 Degree=2 IsPeriodic=0
    g15: BSplineCurve PolesCount=3 KnotsCount=2 Degree=2 IsPeriodic=0
    g16: BSplineCurve PolesCount=3 KnotsCount=2 Degree=2 IsPeriodic=0
    g17: BSplineCurve PolesCount=3 KnotsCount=2 Degree=2 IsPeriodic=0
    g18: BSplineCurve PolesCount=3 KnotsCount=2 Degree=2 IsPeriodic=0
    g19: BSplineCurve PolesCount=3 KnotsCount=2 Degree=2 IsPeriodic=0
    g20: BSplineCurve PolesCount=3 KnotsCount=2 Degree=2 IsPeriodic=0
    g21: BSplineCurve PolesCount=3 KnotsCount=2 Degree=2 IsPeriodic=0
    g22: BSplineCurve PolesCount=3 KnotsCount=2 Degree=2 IsPeriodic=0
    g23: BSplineCurve PolesCount=3 KnotsCount=2 Degree=2 IsPeriodic=0
    g24: BSplineCurve PolesCount=3 KnotsCount=2 Degree=2 IsPeriodic=0
    g25: BSplineCurve PolesCount=3 KnotsCount=2 Degree=2 IsPeriodic=0
    g26: BSplineCurve PolesCount=3 KnotsCount=2 Degree=2 IsPeriodic=0
    g27: BSplineCurve PolesCount=3 KnotsCount=2 Degree=2 IsPeriodic=0
    g28: BSplineCurve PolesCount=3 KnotsCount=2 Degree=2 IsPeriodic=0
    g29: BSplineCurve PolesCount=3 KnotsCount=2 Degree=2 IsPeriodic=0
    g30: LineSegment StartX=32.7677 StartY=-12.319 StartZ=0 EndX=33.0498 EndY=-12.319 EndZ=0
    g31: BSplineCurve PolesCount=3 KnotsCount=2 Degree=2 IsPeriodic=0
    g32: BSplineCurve PolesCount=3 KnotsCount=2 Degree=2 IsPeriodic=0
    g33: BSplineCurve PolesCount=3 KnotsCount=2 Degree=2 IsPeriodic=0
    g34: BSplineCurve PolesCount=3 KnotsCount=2 Degree=2 IsPeriodic=0
    g35: BSplineCurve PolesCount=3 KnotsCount=2 Degree=2 IsPeriodic=0
    g36: BSplineCurve PolesCount=3 KnotsCount=2 Degree=2 IsPeriodic=0
    g37: BSplineCurve PolesCount=3 KnotsCount=2 Degree=2 IsPeriodic=0
    g38: LineSegment StartX=6.97183 StartY=-15.0185 StartZ=0 EndX=4.84568 EndY=-15.0185 EndZ=0
    g39: BSplineCurve PolesCount=3 KnotsCount=2 Degree=2 IsPeriodic=0
    g40: BSplineCurve PolesCount=3 KnotsCount=2 Degree=2 IsPeriodic=0
    g41: LineSegment StartX=6.26082 StartY=-14.3144 StartZ=0 EndX=6.97183 EndY=-14.3144 EndZ=0
    g42: LineSegment StartX=6.26082 StartY=-10.5231 StartZ=0 EndX=6.26082 EndY=-14.3144 EndZ=0
    g43: LineSegment StartX=5.56357 StartY=-10.5231 StartZ=0 EndX=6.26082 EndY=-10.5231 EndZ=0
    g44: LineSegment StartX=4.61173 StartY=-11.1722 StartZ=0 EndX=5.56357 EndY=-10.5231 EndZ=0
    g45: BSplineCurve PolesCount=3 KnotsCount=2 Degree=2 IsPeriodic=0
    g46: BSplineCurve PolesCount=3 KnotsCount=2 Degree=2 IsPeriodic=0
    g47: BSplineCurve PolesCount=3 KnotsCount=2 Degree=2 IsPeriodic=0
    g48: BSplineCurve PolesCount=3 KnotsCount=2 Degree=2 IsPeriodic=0
    g49: BSplineCurve PolesCount=3 KnotsCount=2 Degree=2 IsPeriodic=0
    g50: LineSegment StartX=5.55669 StartY=-11.2983 StartZ=0 EndX=4.97871 EndY=-11.7066 EndZ=0
    g51: LineSegment StartX=5.55669 StartY=-14.3144 StartZ=0 EndX=5.55669 EndY=-11.2983 EndZ=0
    g52: LineSegment StartX=4.84568 StartY=-14.3144 StartZ=0 EndX=5.55669 EndY=-14.3144 EndZ=0
    g53: BSplineCurve PolesCount=3 KnotsCount=2 Degree=2 IsPeriodic=0
    g54: BSplineCurve PolesCount=3 KnotsCount=2 Degree=2 IsPeriodic=0
    g55: BSplineCurve PolesCount=3 KnotsCount=2 Degree=2 IsPeriodic=0
    g56: BSplineCurve PolesCount=3 KnotsCount=2 Degree=2 IsPeriodic=0
    g57: BSplineCurve PolesCount=3 KnotsCount=2 Degree=2 IsPeriodic=0
    g58: BSplineCurve PolesCount=3 KnotsCount=2 Degree=2 IsPeriodic=0
    g59: BSplineCurve PolesCount=3 KnotsCount=2 Degree=2 IsPeriodic=0
    g60: BSplineCurve PolesCount=3 KnotsCount=2 Degree=2 IsPeriodic=0
    g61: BSplineCurve PolesCount=3 KnotsCount=2 Degree=2 IsPeriodic=0
    g62: BSplineCurve PolesCount=3 KnotsCount=2 Degree=2 IsPeriodic=0
    g63: BSplineCurve PolesCount=3 KnotsCount=2 Degree=2 IsPeriodic=0
    g64: BSplineCurve PolesCount=3 KnotsCount=2 Degree=2 IsPeriodic=0
    g65: BSplineCurve PolesCount=3 KnotsCount=2 Degree=2 IsPeriodic=0
    g66: BSplineCurve PolesCount=3 KnotsCount=2 Degree=2 IsPeriodic=0
    g67: BSplineCurve PolesCount=3 KnotsCount=2 Degree=2 IsPeriodic=0
    g68: BSplineCurve PolesCount=3 KnotsCount=2 Degree=2 IsPeriodic=0
    g69: BSplineCurve PolesCount=3 KnotsCount=2 Degree=2 IsPeriodic=0
    g70: BSplineCurve PolesCount=3 KnotsCount=2 Degree=2 IsPeriodic=0
    g71: BSplineCurve PolesCount=3 KnotsCount=2 Degree=2 IsPeriodic=0
    g72: BSplineCurve PolesCount=3 KnotsCount=2 Degree=2 IsPeriodic=0
    g73: BSplineCurve PolesCount=3 KnotsCount=2 Degree=2 IsPeriodic=0
    g74: BSplineCurve PolesCount=3 KnotsCount=2 Degree=2 IsPeriodic=0
    g75: LineSegment StartX=17.6897 StartY=-15.0185 StartZ=0 EndX=17.6897 EndY=-14.2777 EndZ=0
    g76: LineSegment StartX=20.8893 StartY=-15.0185 StartZ=0 EndX=17.6897 EndY=-15.0185 EndZ=0
    g77: LineSegment StartX=20.8893 StartY=-14.3992 StartZ=0 EndX=20.8893 EndY=-15.0185 EndZ=0
    g78: BSplineCurve PolesCount=3 KnotsCount=2 Degree=2 IsPeriodic=0
    g79: BSplineCurve PolesCount=3 KnotsCount=2 Degree=2 IsPeriodic=0
    g80: LineSegment StartX=18.7677 StartY=-14.3144 StartZ=0 EndX=20.1828 EndY=-14.3144 EndZ=0
    g81: BSplineCurve PolesCount=3 KnotsCount=2 Degree=2 IsPeriodic=0
    g82: BSplineCurve PolesCount=3 KnotsCount=2 Degree=2 IsPeriodic=0
  constraints (94):
    c: Coincident(g0,g1)
    c: Coincident(g1,g2)
    c: Coincident(g2,g3)
    c: Coincident(g3,g4)
    c: Coincident(g4,g5)
    c: Coincident(g5,g6)
    c: Coincident(g6,g7)
    c: Coincident(g7,g8)
    c: Coincident(g8,g9)
    c: Coincident(g9,g10)
    c: Coincident(g10,g11)
    c: Coincident(g11,g12)
    c: Coincident(g12,g13)
    c: Coincident(g13,g14)
    c: Coincident(g14,g15)
    c: Coincident(g15,g16)
    c: Coincident(g16,g17)
    c: Coincident(g17,g18)
    c: Coincident(g18,g19)
    c: Coincident(g19,g20)
    c: Coincident(g20,g21)
    c: Coincident(g21,g22)
    c: Coincident(g22,g23)
    c: Coincident(g23,g24)
    c: Coincident(g24,g25)
    c: Coincident(g25,g26)
    c: Coincident(g26,g27)
    c: Coincident(g27,g28)
    c: Coincident(g28,g29)
    c: Coincident(g29,g30)
    c: Horizontal(g30)
    c: Coincident(g30,g31)
    c: Coincident(g31,g32)
    c: Coincident(g32,g33)
    c: Coincident(g33,g34)
    c: Coincident(g34,g35)
    c: Coincident(g35,g0)
    c: Coincident(g36,g37)
    c: Coincident(g37,g38)
    c: Horizontal(g38)
    c: Coincident(g38,g39)
    c: Coincident(g39,g40)
    c: Coincident(g40,g41)
    c: Horizontal(g41)
    c: Coincident(g41,g42)
    c: Vertical(g42)
    c: Coincident(g42,g43)
    c: Horizontal(g43)
    c: Coincident(g43,g44)
    c: Coincident(g44,g45)
    c: Coincident(g45,g46)
    c: Coincident(g46,g47)
    c: Coincident(g47,g48)
    c: Coincident(g48,g49)
    c: Coincident(g49,g50)
    c: Coincident(g50,g51)
    c: Vertical(g51)
    c: Coincident(g51,g52)
    c: Horizontal(g52)
    c: Coincident(g52,g53)
    c: Coincident(g53,g36)
    c: Coincident(g54,g55)
    c: Coincident(g55,g56)
    c: Coincident(g56,g57)
    c: Coincident(g57,g58)
    c: Coincident(g58,g59)
    c: Coincident(g59,g60)
    c: Coincident(g60,g61)
    c: Coincident(g61,g62)
    c: Coincident(g62,g63)
    c: Coincident(g63,g64)
    c: Coincident(g64,g65)
    c: Coincident(g65,g66)
    c: Coincident(g66,g67)
    c: Coincident(g67,g68)
    c: Coincident(g68,g69)
    c: Coincident(g69,g70)
    c: Coincident(g70,g71)
    c: Coincident(g71,g72)
    c: Coincident(g72,g73)
    c: Coincident(g73,g74)
    c: Coincident(g74,g75)
    c: Vertical(g75)
    c: Coincident(g75,g76)
    c: Horizontal(g76)
    c: Coincident(g76,g77)
    c: Vertical(g77)
    c: Coincident(g77,g78)
    c: Coincident(g78,g79)
    c: Coincident(g79,g80)
    c: Horizontal(g80)
    c: Coincident(g80,g81)
    c: Coincident(g81,g82)
    c: Coincident(g82,g54)
FEATURE [Sketcher::SketchObject] Sketch059  label="USB"
  AttachmentOffset = pos=(3,13,0) rot=(0,0,1;0rad)
  Placement = pos=(3.5,-29.6,13) rot=(1,0,0;1.5708rad)
  sketch-geometry (108):
    g0: BSplineCurve PolesCount=3 KnotsCount=2 Degree=2 IsPeriodic=0
    g1: LineSegment StartX=-23.6639 StartY=-11.3569 StartZ=0 EndX=-23.6639 EndY=-12.9238 EndZ=0
    g2: BSplineCurve PolesCount=3 KnotsCount=2 Degree=2 IsPeriodic=0
    g3: BSplineCurve PolesCount=3 KnotsCount=2 Degree=2 IsPeriodic=0
    g4: BSplineCurve PolesCount=3 KnotsCount=2 Degree=2 IsPeriodic=0
    g5: LineSegment StartX=-24.4254 StartY=-10.7936 StartZ=0 EndX=-23.6915 EndY=-10.7936 EndZ=0
    g6: BSplineCurve PolesCount=3 KnotsCount=2 Degree=2 IsPeriodic=0
    g7: BSplineCurve PolesCount=3 KnotsCount=2 Degree=2 IsPeriodic=0
    g8: BSplineCurve PolesCount=3 KnotsCount=2 Degree=2 IsPeriodic=0
    g9: LineSegment StartX=-24.2273 StartY=-11.3569 StartZ=0 EndX=-24.4254 EndY=-11.3569 EndZ=0
    g10: LineSegment StartX=-24.2273 StartY=-12.9752 StartZ=0 EndX=-24.2273 EndY=-11.3569 EndZ=0
    g11: BSplineCurve PolesCount=3 KnotsCount=2 Degree=2 IsPeriodic=0
    g12: BSplineCurve PolesCount=3 KnotsCount=2 Degree=2 IsPeriodic=0
    g13: BSplineCurve PolesCount=3 KnotsCount=2 Degree=2 IsPeriodic=0
    g14: BSplineCurve PolesCount=3 KnotsCount=2 Degree=2 IsPeriodic=0
    g15: LineSegment StartX=-25.6823 StartY=-11.3569 StartZ=0 EndX=-25.6823 EndY=-12.9752 EndZ=0
    g16: LineSegment StartX=-25.4841 StartY=-11.3569 StartZ=0 EndX=-25.6823 EndY=-11.3569 EndZ=0
    g17: BSplineCurve PolesCount=3 KnotsCount=2 Degree=2 IsPeriodic=0
    g18: BSplineCurve PolesCount=3 KnotsCount=2 Degree=2 IsPeriodic=0
    g19: BSplineCurve PolesCount=3 KnotsCount=2 Degree=2 IsPeriodic=0
    g20: LineSegment StartX=-26.2181 StartY=-10.7936 StartZ=0 EndX=-25.4841 EndY=-10.7936 EndZ=0
    g21: BSplineCurve PolesCount=3 KnotsCount=2 Degree=2 IsPeriodic=0
    g22: BSplineCurve PolesCount=3 KnotsCount=2 Degree=2 IsPeriodic=0
    g23: BSplineCurve PolesCount=3 KnotsCount=2 Degree=2 IsPeriodic=0
    g24: LineSegment StartX=-26.2456 StartY=-12.9238 StartZ=0 EndX=-26.2456 EndY=-11.3569 EndZ=0
    g25: BSplineCurve PolesCount=3 KnotsCount=2 Degree=2 IsPeriodic=0
    g26: BSplineCurve PolesCount=3 KnotsCount=2 Degree=2 IsPeriodic=0
    g27: BSplineCurve PolesCount=3 KnotsCount=2 Degree=2 IsPeriodic=0
    g28: BSplineCurve PolesCount=3 KnotsCount=2 Degree=2 IsPeriodic=0
    g29: BSplineCurve PolesCount=3 KnotsCount=2 Degree=2 IsPeriodic=0
    g30: BSplineCurve PolesCount=3 KnotsCount=2 Degree=2 IsPeriodic=0
    g31: BSplineCurve PolesCount=3 KnotsCount=2 Degree=2 IsPeriodic=0
    g32: BSplineCurve PolesCount=3 KnotsCount=2 Degree=2 IsPeriodic=0
    g33: BSplineCurve PolesCount=3 KnotsCount=2 Degree=2 IsPeriodic=0
    g34: BSplineCurve PolesCount=3 KnotsCount=2 Degree=2 IsPeriodic=0
    g35: BSplineCurve PolesCount=3 KnotsCount=2 Degree=2 IsPeriodic=0
    g36: BSplineCurve PolesCount=3 KnotsCount=2 Degree=2 IsPeriodic=0
    g37: BSplineCurve PolesCount=3 KnotsCount=2 Degree=2 IsPeriodic=0
    g38: BSplineCurve PolesCount=3 KnotsCount=2 Degree=2 IsPeriodic=0
    g39: BSplineCurve PolesCount=3 KnotsCount=2 Degree=2 IsPeriodic=0
    g40: BSplineCurve PolesCount=3 KnotsCount=2 Degree=2 IsPeriodic=0
    g41: BSplineCurve PolesCount=3 KnotsCount=2 Degree=2 IsPeriodic=0
    g42: BSplineCurve PolesCount=3 KnotsCount=2 Degree=2 IsPeriodic=0
    g43: BSplineCurve PolesCount=3 KnotsCount=2 Degree=2 IsPeriodic=0
    g44: BSplineCurve PolesCount=3 KnotsCount=2 Degree=2 IsPeriodic=0
    g45: BSplineCurve PolesCount=3 KnotsCount=2 Degree=2 IsPeriodic=0
    g46: BSplineCurve PolesCount=3 KnotsCount=2 Degree=2 IsPeriodic=0
    g47: BSplineCurve PolesCount=3 KnotsCount=2 Degree=2 IsPeriodic=0
    g48: BSplineCurve PolesCount=3 KnotsCount=2 Degree=2 IsPeriodic=0
    g49: BSplineCurve PolesCount=3 KnotsCount=2 Degree=2 IsPeriodic=0
    g50: BSplineCurve PolesCount=3 KnotsCount=2 Degree=2 IsPeriodic=0
    g51: BSplineCurve PolesCount=3 KnotsCount=2 Degree=2 IsPeriodic=0
    g52: BSplineCurve PolesCount=3 KnotsCount=2 Degree=2 IsPeriodic=0
    g53: LineSegment StartX=-22.8915 StartY=-13.7018 StartZ=0 EndX=-22.8915 EndY=-13.3293 EndZ=0
    g54: BSplineCurve PolesCount=3 KnotsCount=2 Degree=2 IsPeriodic=0
    g55: BSplineCurve PolesCount=3 KnotsCount=2 Degree=2 IsPeriodic=0
    g56: BSplineCurve PolesCount=3 KnotsCount=2 Degree=2 IsPeriodic=0
    g57: BSplineCurve PolesCount=3 KnotsCount=2 Degree=2 IsPeriodic=0
    g58: BSplineCurve PolesCount=3 KnotsCount=2 Degree=2 IsPeriodic=0
    g59: BSplineCurve PolesCount=3 KnotsCount=2 Degree=2 IsPeriodic=0
    g60: BSplineCurve PolesCount=3 KnotsCount=2 Degree=2 IsPeriodic=0
    g61: BSplineCurve PolesCount=3 KnotsCount=2 Degree=2 IsPeriodic=0
    g62: BSplineCurve PolesCount=3 KnotsCount=2 Degree=2 IsPeriodic=0
    g63: BSplineCurve PolesCount=3 KnotsCount=2 Degree=2 IsPeriodic=0
    g64: BSplineCurve PolesCount=3 KnotsCount=2 Degree=2 IsPeriodic=0
    g65: BSplineCurve PolesCount=3 KnotsCount=2 Degree=2 IsPeriodic=0
    g66: BSplineCurve PolesCount=3 KnotsCount=2 Degree=2 IsPeriodic=0
    g67: BSplineCurve PolesCount=3 KnotsCount=2 Degree=2 IsPeriodic=0
    g68: BSplineCurve PolesCount=3 KnotsCount=2 Degree=2 IsPeriodic=0
    g69: BSplineCurve PolesCount=3 KnotsCount=2 Degree=2 IsPeriodic=0
    g70: BSplineCurve PolesCount=3 KnotsCount=2 Degree=2 IsPeriodic=0
    g71: BSplineCurve PolesCount=3 KnotsCount=2 Degree=2 IsPeriodic=0
    g72: BSplineCurve PolesCount=3 KnotsCount=2 Degree=2 IsPeriodic=0
    g73: BSplineCurve PolesCount=3 KnotsCount=2 Degree=2 IsPeriodic=0
    g74: BSplineCurve PolesCount=3 KnotsCount=2 Degree=2 IsPeriodic=0
    g75: BSplineCurve PolesCount=3 KnotsCount=2 Degree=2 IsPeriodic=0
    g76: BSplineCurve PolesCount=3 KnotsCount=2 Degree=2 IsPeriodic=0
    g77: LineSegment StartX=-20.3263 StartY=-11.0871 StartZ=0 EndX=-20.3263 EndY=-11.5826 EndZ=0
    g78: BSplineCurve PolesCount=3 KnotsCount=2 Degree=2 IsPeriodic=0
    g79: BSplineCurve PolesCount=3 KnotsCount=2 Degree=2 IsPeriodic=0
    g80: LineSegment StartX=-17.7263 StartY=-14.0798 StartZ=0 EndX=-19.3887 EndY=-14.0798 EndZ=0
    g81: BSplineCurve PolesCount=3 KnotsCount=2 Degree=2 IsPeriodic=0
    g82: BSplineCurve PolesCount=3 KnotsCount=2 Degree=2 IsPeriodic=0
    g83: BSplineCurve PolesCount=3 KnotsCount=2 Degree=2 IsPeriodic=0
    g84: BSplineCurve PolesCount=3 KnotsCount=2 Degree=2 IsPeriodic=0
    g85: BSplineCurve PolesCount=3 KnotsCount=2 Degree=2 IsPeriodic=0
    g86: BSplineCurve PolesCount=3 KnotsCount=2 Degree=2 IsPeriodic=0
    g87: LineSegment StartX=-19.3887 StartY=-10.7936 StartZ=0 EndX=-17.963 EndY=-10.7936 EndZ=0
    g88: BSplineCurve PolesCount=3 KnotsCount=2 Degree=2 IsPeriodic=0
    g89: BSplineCurve PolesCount=3 KnotsCount=2 Degree=2 IsPeriodic=0
    g90: BSplineCurve PolesCount=3 KnotsCount=2 Degree=2 IsPeriodic=0
    g91: LineSegment StartX=-19.3043 StartY=-11.3569 StartZ=0 EndX=-19.3887 EndY=-11.3569 EndZ=0
    g92: LineSegment StartX=-19.3043 StartY=-13.5165 StartZ=0 EndX=-19.3043 EndY=-11.3569 EndZ=0
    g93: LineSegment StartX=-19.3887 StartY=-13.5165 StartZ=0 EndX=-19.3043 EndY=-13.5165 EndZ=0
    g94: BSplineCurve PolesCount=3 KnotsCount=2 Degree=2 IsPeriodic=0
    g95: BSplineCurve PolesCount=3 KnotsCount=2 Degree=2 IsPeriodic=0
    g96: BSplineCurve PolesCount=3 KnotsCount=2 Degree=2 IsPeriodic=0
    g97: LineSegment StartX=-18.741 StartY=-13.5165 StartZ=0 EndX=-17.7539 EndY=-13.5165 EndZ=0
    g98: LineSegment StartX=-18.741 StartY=-12.7165 StartZ=0 EndX=-18.741 EndY=-13.5165 EndZ=0
    g99: LineSegment StartX=-17.9795 StartY=-12.7165 StartZ=0 EndX=-18.741 EndY=-12.7165 EndZ=0
    g100: BSplineCurve PolesCount=3 KnotsCount=2 Degree=2 IsPeriodic=0
    g101: LineSegment StartX=-18.741 StartY=-12.1514 StartZ=0 EndX=-18.1043 EndY=-12.1514 EndZ=0
    g102: LineSegment StartX=-18.741 StartY=-11.3569 StartZ=0 EndX=-18.741 EndY=-12.1514 EndZ=0
    g103: LineSegment StartX=-17.9906 StartY=-11.3569 StartZ=0 EndX=-18.741 EndY=-11.3569 EndZ=0
    g104: BSplineCurve PolesCount=3 KnotsCount=2 Degree=2 IsPeriodic=0
    g105: BSplineCurve PolesCount=3 KnotsCount=2 Degree=2 IsPeriodic=0
    g106: BSplineCurve PolesCount=3 KnotsCount=2 Degree=2 IsPeriodic=0
    g107: BSplineCurve PolesCount=3 KnotsCount=2 Degree=2 IsPeriodic=0
  constraints (129):
    c: Coincident(g0,g1)
    c: Vertical(g1)
    c: Coincident(g1,g2)
    c: Coincident(g2,g3)
    c: Coincident(g3,g4)
    c: Coincident(g4,g5)
    c: Horizontal(g5)
    c: Coincident(g5,g6)
    c: Coincident(g6,g7)
    c: Coincident(g7,g8)
    c: Coincident(g8,g9)
    c: Horizontal(g9)
    c: Coincident(g9,g10)
    c: Vertical(g10)
    c: Coincident(g10,g11)
    c: Coincident(g11,g12)
    c: Coincident(g12,g13)
    c: Coincident(g13,g14)
    c: Coincident(g14,g15)
    c: Vertical(g15)
    c: Coincident(g15,g16)
    c: Horizontal(g16)
    c: Coincident(g16,g17)
    c: Coincident(g17,g18)
    c: Coincident(g18,g19)
    c: Coincident(g19,g20)
    c: Horizontal(g20)
    c: Coincident(g20,g21)
    c: Coincident(g21,g22)
    c: Coincident(g22,g23)
    c: Coincident(g23,g24)
    c: Vertical(g24)
    c: Coincident(g24,g25)
    c: Coincident(g25,g26)
    c: Coincident(g26,g27)
    c: Coincident(g27,g0)
    c: Coincident(g28,g29)
    c: Coincident(g29,g30)
    c: Coincident(g30,g31)
    c: Coincident(g31,g32)
    c: Coincident(g32,g33)
    c: Coincident(g33,g34)
    c: Coincident(g34,g35)
    c: Coincident(g35,g36)
    c: Coincident(g36,g37)
    c: Coincident(g37,g38)
    c: Coincident(g38,g39)
    c: Coincident(g39,g40)
    c: Coincident(g40,g41)
    c: Coincident(g41,g42)
    c: Coincident(g42,g43)
    c: Coincident(g43,g44)
    c: Coincident(g44,g45)
    c: Coincident(g45,g46)
    c: Coincident(g46,g47)
    c: Coincident(g47,g48)
    c: Coincident(g48,g49)
    c: Coincident(g49,g50)
    c: Coincident(g50,g51)
    c: Coincident(g51,g52)
    c: Coincident(g52,g53)
    c: Vertical(g53)
    c: Coincident(g53,g54)
    c: Coincident(g54,g55)
    c: Coincident(g55,g56)
    c: Coincident(g56,g57)
    c: Coincident(g57,g58)
    c: Coincident(g58,g59)
    c: Coincident(g59,g60)
    c: Coincident(g60,g61)
    c: Coincident(g61,g62)
    c: Coincident(g62,g63)
    c: Coincident(g63,g64)
    c: Coincident(g64,g65)
    c: Coincident(g65,g66)
    c: Coincident(g66,g67)
    c: Coincident(g67,g68)
    c: Coincident(g68,g69)
    c: Coincident(g69,g70)
    c: Coincident(g70,g71)
    c: Coincident(g71,g72)
    c: Coincident(g72,g73)
    c: Coincident(g73,g74)
    c: Coincident(g74,g75)
    c: Coincident(g75,g76)
    c: Coincident(g76,g77)
    c: Vertical(g77)
    c: Coincident(g77,g78)
    c: Coincident(g78,g28)
    c: Coincident(g79,g80)
    c: Horizontal(g80)
    c: Coincident(g80,g81)
    c: Coincident(g81,g82)
    c: Coincident(g82,g83)
    c: Coincident(g83,g84)
    c: Coincident(g84,g85)
    c: Coincident(g85,g86)
    c: Coincident(g86,g87)
    c: Horizontal(g87)
    c: Coincident(g87,g88)
    c: Coincident(g88,g89)
    c: Coincident(g89,g90)
    c: Coincident(g90,g91)
    c: Horizontal(g91)
    c: Coincident(g91,g92)
    c: Vertical(g92)
    c: Coincident(g92,g93)
    c: Horizontal(g93)
    c: Coincident(g93,g94)
    c: Coincident(g94,g79)
    c: Coincident(g95,g96)
    c: Coincident(g96,g97)
    c: Horizontal(g97)
    c: Coincident(g97,g98)
    c: Vertical(g98)
    c: Coincident(g98,g99)
    c: Horizontal(g99)
    c: Coincident(g99,g100)
    c: Coincident(g100,g95)
    c: Horizontal(g101)
    c: Coincident(g101,g102)
    c: Vertical(g102)
    c: Coincident(g102,g103)
    c: Horizontal(g103)
    c: Coincident(g103,g104)
    c: Coincident(g104,g105)
    c: Coincident(g105,g106)
    c: Coincident(g106,g107)
    c: Coincident(g107,g101)
FEATURE [Sketcher::SketchObject] Sketch060  label="makeUSB_lighted1"
  Placement = pos=(0,-28,-1) rot=(0,0.707107,0.707107;3.14159rad)
  sketch-geometry (4):
    g0: LineSegment StartX=12.1 StartY=4 StartZ=0 EndX=24.1 EndY=4 EndZ=0
    g1: LineSegment StartX=24.1 StartY=4 StartZ=0 EndX=24.1 EndY=0 EndZ=0
    g2: LineSegment StartX=24.1 StartY=0 StartZ=0 EndX=12.1 EndY=0 EndZ=0
    g3: LineSegment StartX=12.1 StartY=0 StartZ=0 EndX=12.1 EndY=4 EndZ=0
  constraints (12):
    c: Coincident(g0,g1)
    c: Coincident(g1,g2)
    c: Coincident(g2,g3)
    c: Coincident(g3,g0)
    c: Horizontal(g0)
    c: Horizontal(g2)
    c: Vertical(g1)
    c: Vertical(g3)
    c: DistanceX(g0,g0) = 12
    c: DistanceY(g3,g3) = 4
    c: DistanceX(g-1,g2) = 12.1
    c: Horizontal(g2,g-1)
FEATURE [Sketcher::SketchObject] Sketch061  label="holes"
  MapMode = 5
  Placement = pos=(0,0,-6) rot=(0,0,1;0rad)
  sketch-geometry (1):
    g0: Circle CenterX=-38 CenterY=25 CenterZ=0 NormalX=0 NormalY=0 NormalZ=1 AngleXU=0 Radius=1.6
  constraints (3):
    c: DistanceX(g0,g-1) = 38
    c: DistanceY(g-1,g0) = 25
    c: Radius(g0) = 1.6
FEATURE [PartDesign::Mirrored] Mirrored009
  MirrorPlane = -> Sketch061 [V_Axis]
  Refine = true
FEATURE [PartDesign::Mirrored] Mirrored010
  MirrorPlane = -> Sketch061 [H_Axis]
  Refine = true
FEATURE [PartDesign::Mirrored] Mirrored011
  MirrorPlane = -> Sketch061 [V_Axis]
  Refine = true
FEATURE [PartDesign::Mirrored] Mirrored012
  MirrorPlane = -> Sketch061 [H_Axis]
  Refine = true
FEATURE [Sketcher::SketchObject] Sketch066
  MapMode = 5
  Placement = pos=(0,0,10.05) rot=(0,0,1;0rad)
  sketch-geometry (4):
    g0: LineSegment StartX=-24.8 StartY=-30 StartZ=0 EndX=-11.4 EndY=-30 EndZ=0
    g1: LineSegment StartX=-11.4 StartY=-30 StartZ=0 EndX=-11.4 EndY=-28 EndZ=0
    g2: LineSegment StartX=-11.4 StartY=-28 StartZ=0 EndX=-24.8 EndY=-28 EndZ=0
    g3: LineSegment StartX=-24.8 StartY=-28 StartZ=0 EndX=-24.8 EndY=-30 EndZ=0
  constraints (12):
    c: DistanceY(g1,g-1) = 28
    c: DistanceX(g1,g-1) = 11.4
    c: Coincident(g1,g2)
    c: Coincident(g0,g1)
    c: Coincident(g2,g3)
    c: Coincident(g0,g3)
    c: DistanceX(g2,g2) = 13.4
    c: DistanceY(g3,g3) = 2
    c: Horizontal(g0)
    c: Horizontal(g2)
    c: Vertical(g3)
    c: Vertical(g1)
FEATURE [PartDesign::Mirrored] Mirrored
  MirrorPlane = -> Sketch019 [V_Axis]
  Refine = true
FEATURE [PartDesign::Mirrored] Mirrored013
  MirrorPlane = -> Sketch019 [H_Axis]
  Refine = true
FEATURE [PartDesign::MultiTransform] MultiTransform006
  BaseFeature = -> Pad002
  Originals = -> [Pad002]
  Refine = true
  Transformations = -> [Mirrored,Mirrored013]
FEATURE [PartDesign::Pocket] Pocket025  label="text_45678"
  BaseFeature = -> MultiTransform006
  Length = 0.4
  Length2 = 100
  Profile = -> Sketch057
  Refine = true
  Type = 0
FEATURE [PartDesign::Pocket] Pocket026  label="text_123"
  BaseFeature = -> Pocket025
  Length = 0.4
  Length2 = 100
  Profile = -> Sketch058
  Refine = true
  Type = 0
FEATURE [Part::Part2DObjectPython] ShapeString002  # Draft 2D object (typed FeaturePython)
  FontFile = <path>
  Placement = pos=(-26.6456,30,14.0798) rot=(-1,0,0;1.5708rad)
  Size = 2
  String = USB
  Support = -> [Pocket026]
  Tracking = 0
FEATURE [PartDesign::Pocket] Pocket027  label="text_USB"
  BaseFeature = -> Pocket026
  Length = 0.4
  Length2 = 100
  Profile = -> Sketch059
  Refine = true
  Type = 0
FEATURE [PartDesign::Pocket] Pocket028  label="makeUSB_lighted"
  BaseFeature = -> Pocket027
  Length = 0.75
  Length2 = 100
  Profile = -> Sketch060
  Refine = true
  Type = 0
FEATURE [PartDesign::Hole] Hole  label="headHole"
  BaseFeature = -> Pocket028
  Depth = 16
  DepthType = 0
  Diameter = 6
  DrillPoint = 1
  DrillPointAngle = 120
  HoleCutCountersinkAngle = 90
  HoleCutDepth = 0
  HoleCutDiameter = 0
  HoleCutType = 0
  ModelActualThread = false
  Profile = -> Sketch061
  Refine = true
  Reversed = true
  Tapered = false
  TaperedAngle = 90
  ThreadAngle = 0
  ThreadClass = 0
  ThreadCutOffInner = 0
  ThreadCutOffOuter = 0
  ThreadDirection = 0
  ThreadFit = 0
  ThreadPitch = 0
  ThreadSize = 0
  ThreadType = 0
  Threaded = false
FEATURE [PartDesign::Pocket] Pocket029  label="holeThrough"
  BaseFeature = -> Hole
  Length = 30
  Length2 = 100
  Profile = -> Sketch061
  Refine = true
  Reversed = true
  Type = 0
FEATURE [PartDesign::MultiTransform] MultiTransform004  label="holeThrough_multiplied"
  BaseFeature = -> Pocket029
  Originals = -> [Pocket029]
  Refine = true
  Transformations = -> [Mirrored009,Mirrored010]
FEATURE [PartDesign::MultiTransform] MultiTransform005  label="headHole_multiplied"
  BaseFeature = -> MultiTransform004
  Originals = -> [Hole]
  Refine = true
  Transformations = -> [Mirrored011,Mirrored012]
FEATURE [PartDesign::Pocket] Pocket033  label="USB_Holder_cut_inner"
  BaseFeature = -> MultiTransform005
  Length = 2.65
  Length2 = 100
  Profile = -> Sketch066
  Refine = true
  Type = 0
FEATURE [Sketcher::SketchObject] Sketch070
  MapMode = 5
  Placement = pos=(42.6,0,0) rot=(0.57735,0.57735,0.57735;2.0944rad)
  Support = -> [Pocket033]
  sketch-geometry (4):
    g0: LineSegment StartX=-1 StartY=11 StartZ=0 EndX=5 EndY=11 EndZ=0
    g1: LineSegment StartX=5 StartY=11 StartZ=0 EndX=5 EndY=7.5 EndZ=0
    g2: ArcOfCircle CenterX=2 CenterY=7.5 CenterZ=0 NormalX=0 NormalY=0 NormalZ=1 AngleXU=0 Radius=3 StartAngle=3.14159 EndAngle=6.28319
    g3: LineSegment StartX=-1 StartY=7.5 StartZ=0 EndX=-1 EndY=11 EndZ=0
  constraints (11):
    c: Horizontal(g0)
    c: Coincident(g0,g1)
    c: Vertical(g1)
    c: Tangent(g1,g2) = 1.5708
    c: Tangent(g2,g3) = 1.5708
    c: Coincident(g0,g3)
    c: Horizontal(g2,g2)
    c: Radius(g2) = 3
    c: DistanceY(g3,g3) = 3.5
    c: DistanceY(g-1,g0) = 11
    c: DistanceX(g-1,g0) = -1
FEATURE [PartDesign::Chamfer] Chamfer001
  Base = -> Pocket033 [Edge113]
  BaseFeature = -> Pocket033
  Size = 0.4
FEATURE [PartDesign::Pocket] Pocket037  label="PressureLineCut"
  BaseFeature = -> Chamfer001
  Length = 5
  Length2 = 100
  Profile = -> Sketch070
  Refine = true
  Type = 0
FEATURE [PartDesign::Body] Body001  label="Case_body"
  Group = -> [Sketch016,Pad003,Pocket007,Sketch014,Sketch017,Sketch019,Sketch020,Pocket011,Pocket008,Sketch022,Pocket012,Sketch051,Pocket024,Sketch057,Pad002,MultiTransform006,Pocket025,Sketch058,Pocket026,Sketch059,Pocket027,Sketch060,Pocket028,Sketch061,Hole,Pocket029,MultiTransform004,Mirrored009,Mirrored010,MultiTransform005,Mirrored011,Mirrored012,Sketch066,Pocket033,Chamfer001,Mirrored,Mirrored013,+2 more]
  Origin = -> Origin261
  Placement = pos=(0,0,13.3) rot=(1,0,0;3.14159rad)
  Tip = -> Pocket037
FEATURE [Mesh::Feature] Mesh  label="FABI_Bottom_PressureHole (Meshed)"
FEATURE [Mesh::Feature] Mesh001  label="FABI_Top (Meshed)"
FEATURE [Sketcher::SketchObject] Sketch037  label="DisplayBox1"
  MapMode = 5
  Support = -> [DatumPlane]
  sketch-geometry (6):
    g0: LineSegment StartX=-38.6 StartY=2.65 StartZ=0 EndX=2.2 EndY=2.65 EndZ=0
    g1: LineSegment StartX=2.2 StartY=-12.15 StartZ=0 EndX=-38.6 EndY=-12.15 EndZ=0
    g2: LineSegment StartX=-38.6 StartY=-12.15 StartZ=0 EndX=-38.6 EndY=2.65 EndZ=0
    g3: LineSegment StartX=2.2 StartY=2.65 StartZ=0 EndX=4.1 EndY=2.65 EndZ=0
    g4: LineSegment StartX=4.1 StartY=2.65 StartZ=0 EndX=4.1 EndY=-12.15 EndZ=0
    g5: LineSegment StartX=4.1 StartY=-12.15 StartZ=0 EndX=2.2 EndY=-12.15 EndZ=0
  constraints (16):
    c: Coincident(g1,g2)
    c: Coincident(g2,g0)
    c: Horizontal(g0)
    c: Horizontal(g1)
    c: Vertical(g2)
    c: Block(g0)
    c: Block(g2)
    c: Block(g1)
    c: Coincident(g3,g0)
    c: Horizontal(g3)
    c: Coincident(g3,g4)
    c: Vertical(g4)
    c: Coincident(g4,g5)
    c: Horizontal(g5)
    c: DistanceX(g3,g3) = 1.9
    c: Coincident(g5,g1)
FEATURE [PartDesign::Pad] Pad004  label="DisplayBox"
  BaseFeature = -> Pocket019
  Length = 2
  Length2 = 100
  Profile = -> Sketch037
  Refine = true
  Type = 0
FEATURE [Sketcher::SketchObject] Sketch040  label="PCBCut002"
  AttachmentOffset = pos=(0,0,2.4) rot=(0,0,1;0rad)
  ExternalGeometry = -> [Pad004]
  MapMode = 5
  Placement = pos=(0,0,2.4) rot=(0,0,1;0rad)
  Support = -> [DatumPlane]
  sketch-geometry (4):
    g0: LineSegment StartX=-37.6 StartY=1.65 StartZ=0 EndX=3.1 EndY=1.65 EndZ=0
    g1: LineSegment StartX=3.1 StartY=1.65 StartZ=0 EndX=3.1 EndY=-11.15 EndZ=0
    g2: LineSegment StartX=3.1 StartY=-11.15 StartZ=0 EndX=-37.6 EndY=-11.15 EndZ=0
    g3: LineSegment StartX=-37.6 StartY=-11.15 StartZ=0 EndX=-37.6 EndY=1.65 EndZ=0
  constraints (12):
    c: Coincident(g0,g1)
    c: Coincident(g1,g2)
    c: Coincident(g2,g3)
    c: Coincident(g3,g0)
    c: Horizontal(g0)
    c: Horizontal(g2)
    c: Vertical(g1)
    c: Vertical(g3)
    c: DistanceY(g-1,g0) = 1.65
    c: DistanceX(g-1,g0) = 3.1
    c: DistanceY(g3,g3) = 12.8
    c: DistanceX(g0,g0) = 40.7
FEATURE [PartDesign::Pocket] Pocket013  label="d_PCBCut"
  BaseFeature = -> Pad004
  Length = 1.5
  Length2 = 100
  Profile = -> Sketch040
  Refine = true
  Type = 0
FEATURE [Sketcher::SketchObject] Sketch041  label="OLEDCut1"
  AttachmentOffset = pos=(0,0,2.4) rot=(0,0,1;0rad)
  ExternalGeometry = -> [Pocket013]
  MapMode = 5
  Placement = pos=(0,0,2.4) rot=(0,0,1;0rad)
  Support = -> [DatumPlane]
  sketch-geometry (4):
    g0: LineSegment StartX=-32.2 StartY=1.65 StartZ=0 EndX=-5.6 EndY=1.65 EndZ=0
    g1: LineSegment StartX=-5.6 StartY=1.65 StartZ=0 EndX=-5.6 EndY=-11.15 EndZ=0
    g2: LineSegment StartX=-5.6 StartY=-11.15 StartZ=0 EndX=-32.2 EndY=-11.15 EndZ=0
    g3: LineSegment StartX=-32.2 StartY=-11.15 StartZ=0 EndX=-32.2 EndY=1.65 EndZ=0
  constraints (12):
    c: Coincident(g0,g1)
    c: Coincident(g1,g2)
    c: Coincident(g2,g3)
    c: Coincident(g3,g0)
    c: Horizontal(g0)
    c: Horizontal(g2)
    c: Vertical(g1)
    c: Vertical(g3)
    c: DistanceY(g1,g1) = 12.8
    c: DistanceX(g0,g0) = 26.6
    c: DistanceY(g-1,g0) = 1.65
    c: DistanceX(g0,g-1) = 5.6
FEATURE [Sketcher::SketchObject] Sketch045  label="DisplayCableCut1"
  AttachmentOffset = pos=(0,0,2.4) rot=(0,0,1;0rad)
  ExternalGeometry = -> [Sketch041]
  MapMode = 5
  Placement = pos=(0,0,2.4) rot=(0,0,1;0rad)
  Support = -> [DatumPlane]
  sketch-geometry (6):
    g0: LineSegment StartX=-5.6 StartY=1.65 StartZ=0 EndX=3.1 EndY=1.65 EndZ=0
    g1: LineSegment StartX=3.1 StartY=1.65 StartZ=0 EndX=3.1 EndY=-9.15 EndZ=0
    g2: LineSegment StartX=3.1 StartY=-9.15 StartZ=0 EndX=1.1 EndY=-9.15 EndZ=0
    g3: LineSegment StartX=1.1 StartY=-9.15 StartZ=0 EndX=1.1 EndY=-11.15 EndZ=0
    g4: LineSegment StartX=1.1 StartY=-11.15 StartZ=0 EndX=-5.6 EndY=-11.15 EndZ=0
    g5: LineSegment StartX=-5.6 StartY=1.65 StartZ=0 EndX=-5.6 EndY=-11.15 EndZ=0
  constraints (16):
    c: Coincident(g-3,g0)
    c: Horizontal(g0)
    c: Coincident(g0,g1)
    c: Vertical(g1)
    c: Coincident(g1,g2)
    c: Coincident(g2,g3)
    c: Vertical(g3)
    c: Coincident(g3,g4)
    c: Coincident(g4,g-3)
    c: Horizontal(g4)
    c: Horizontal(g2)
    c: DistanceY(g3,g3) = 2
    c: DistanceX(g2,g2) = 2
    c: DistanceX(g0,g0) = 8.7
    c: Coincident(g5,g0)
    c: Coincident(g5,g4)
FEATURE [PartDesign::Pocket] Pocket014  label="d_OLEDCut"
  BaseFeature = -> Pocket013
  Length = 2.8
  Length2 = 100
  Profile = -> Sketch041
  Refine = true
  Type = 0
FEATURE [Sketcher::SketchObject] Sketch042  label="OLEDCutThrough1"
  AttachmentOffset = pos=(0,0,2) rot=(0,0,1;0rad)
  ExternalGeometry = -> [Pocket014]
  MapMode = 5
  Placement = pos=(0,0,2) rot=(0,0,1;0rad)
  Support = -> [DatumPlane]
  sketch-geometry (4):
    g0: LineSegment StartX=-31 StartY=-1 StartZ=0 EndX=-6.8 EndY=-1 EndZ=0
    g1: LineSegment StartX=-6.8 StartY=-1 StartZ=0 EndX=-6.8 EndY=-9.5 EndZ=0
    g2: LineSegment StartX=-6.8 StartY=-9.5 StartZ=0 EndX=-31 EndY=-9.5 EndZ=0
    g3: LineSegment StartX=-31 StartY=-9.5 StartZ=0 EndX=-31 EndY=-1 EndZ=0
  constraints (8):
    c: Coincident(g0,g1)
    c: Coincident(g1,g2)
    c: Coincident(g2,g3)
    c: Coincident(g3,g0)
    c: Horizontal(g0)
    c: Horizontal(g2)
    c: Vertical(g1)
    c: Vertical(g3)
FEATURE [PartDesign::Pocket] Pocket015  label="d_OLEDCutThrough"
  BaseFeature = -> Pocket014
  Length = 5
  Length2 = 100
  Profile = -> Sketch042
  Refine = true
  Type = 0
FEATURE [Sketcher::SketchObject] Sketch043  label="PinHeaderPocket1"
  AttachmentOffset = pos=(0,0,2) rot=(0,0,1;0rad)
  ExternalGeometry = -> [Pocket015]
  MapMode = 5
  Placement = pos=(0,0,2) rot=(0,0,1;0rad)
  Support = -> [DatumPlane]
  sketch-geometry (4):
    g0: LineSegment StartX=-37.6 StartY=0.25 StartZ=0 EndX=-34.7 EndY=0.25 EndZ=0
    g1: LineSegment StartX=-34.7 StartY=0.25 StartZ=0 EndX=-34.7 EndY=-9.75 EndZ=0
    g2: LineSegment StartX=-34.7 StartY=-9.75 StartZ=0 EndX=-37.6 EndY=-9.75 EndZ=0
    g3: LineSegment StartX=-37.6 StartY=-9.75 StartZ=0 EndX=-37.6 EndY=0.25 EndZ=0
  constraints (12):
    c: Coincident(g0,g1)
    c: Coincident(g1,g2)
    c: Coincident(g2,g3)
    c: Coincident(g3,g0)
    c: Horizontal(g0)
    c: Horizontal(g2)
    c: Vertical(g1)
    c: Vertical(g3)
    c: DistanceX(g0,g0) = 2.9
    c: DistanceY(g1,g1) = 10
    c: DistanceX(g0,g-1) = 34.7
    c: DistanceY(g-1,g0) = 0.25
FEATURE [PartDesign::Pocket] Pocket016  label="d_PinHeaderPocket"
  BaseFeature = -> Pocket015
  Length = 2.6
  Length2 = 100
  Profile = -> Sketch043
  Refine = true
  Type = 0
FEATURE [PartDesign::Pocket] Pocket018  label="d_DisplayCableCut"
  BaseFeature = -> Pocket016
  Length = 2.6
  Length2 = 100
  Profile = -> Sketch045
  Refine = true
  Type = 0
FEATURE [PartDesign::Plane] DatumPlane001
  Length = 94.0535
  MapMode = 5
  Placement = pos=(0,29.6,0) rot=(0,0.707107,0.707107;3.14159rad)
  ResizeMode = 0
  Support = -> [Pocket018]
  Width = 31.8535
FEATURE [Sketcher::SketchObject] Sketch047  label="MicroUSB_cut1"
  ExternalGeometry = -> [Pocket018]
  MapMode = 5
  Placement = pos=(0,29.6,0) rot=(0,0.707107,0.707107;3.14159rad)
  Support = -> [DatumPlane001]
  sketch-geometry (10):
    g0: LineSegment StartX=13.6 StartY=13 StartZ=0 EndX=22.6 EndY=13 EndZ=0
    g1: LineSegment StartX=22.6 StartY=11.7 StartZ=0 EndX=20.9996 EndY=10.2 EndZ=0
    g2: LineSegment StartX=20.9996 StartY=10.2 StartZ=0 EndX=15.1996 EndY=10.2 EndZ=0
    g3: LineSegment StartX=15.1996 StartY=10.2 StartZ=0 EndX=13.5992 EndY=11.7 EndZ=0
    g4: LineSegment StartX=13.5992 StartY=11.7 StartZ=0 EndX=11.6 EndY=11.7 EndZ=0
    g5: LineSegment StartX=11.6 StartY=11.7 StartZ=0 EndX=11.6 EndY=13 EndZ=0
    g6: LineSegment StartX=22.6 StartY=11.7 StartZ=0 EndX=24.6 EndY=11.7 EndZ=0
    g7: LineSegment StartX=11.6 StartY=13 StartZ=0 EndX=13.6 EndY=13 EndZ=0
    g8: LineSegment StartX=22.6 StartY=13 StartZ=0 EndX=24.6 EndY=13 EndZ=0
    g9: LineSegment StartX=24.6 StartY=13 StartZ=0 EndX=24.6 EndY=11.7 EndZ=0
  constraints (30):
    c: Horizontal(g0)
    c: Coincident(g1,g2)
    c: Horizontal(g2)
    c: Coincident(g2,g3)
    c: Equal(g3,g1)
    c: DistanceX(g2,g2) = 5.8
    c: DistanceY(g1,g0) = 2.8
    c: DistanceY(g1,g0) = 1.3
    c: DistanceX(g0,g-3) = 13
    c: DistanceY(g-3,g0) = 14
    c: Coincident(g3,g4)
    c: Horizontal(g4)
    c: Coincident(g4,g5)
    c: Vertical(g5)
    c: Coincident(g1,g6)
    c: Horizontal(g6)
    c: DistanceX(g0,g0) = 9
    c: Coincident(g7,g0)
    c: Coincident(g5,g7)
    c: Horizontal(g7)
    c: DistanceY(g3,g0) = 1.3
    c: DistanceX(g7,g7) = 2
    c: Coincident(g0,g8)
    c: Horizontal(g8)
    c: Coincident(g8,g9)
    c: Vertical(g9)
    c: Coincident(g6,g9)
    c: DistanceX(g8,g8) = 2
    c: DistanceX(g6,g6) = 2
    c: DistanceX(g3,g2) = 1.6004
FEATURE [PartDesign::Pocket] Pocket020  label="MicroUSB_cut"
  BaseFeature = -> Pocket018
  Length = 5
  Length2 = 100
  Profile = -> Sketch047
  Refine = true
  Type = 0
FEATURE [PartDesign::Plane] DatumPlane002  label="top_face"
  Length = 99.404
  Placement = pos=(0,0,13) rot=(0,0,1;0rad)
  ResizeMode = 0
  Support = -> [Pocket020]
  Width = 73.404
FEATURE [Sketcher::SketchObject] Sketch068
  MapMode = 5
  Placement = pos=(0,0,9.05) rot=(0,0,1;0rad)
  Support = -> [Pocket020]
  sketch-geometry (5):
    g0: LineSegment StartX=32.1 StartY=28.4 StartZ=0 EndX=35.6 EndY=28.4 EndZ=0
    g1: ArcOfCircle CenterX=35.6 CenterY=22.6 CenterZ=0 NormalX=0 NormalY=0 NormalZ=1 AngleXU=0 Radius=5.8 StartAngle=1e-16 EndAngle=1.5708
    g2: LineSegment StartX=41.4 StartY=22.6 StartZ=0 EndX=41.4 EndY=19.1 EndZ=0
    g3: LineSegment StartX=41.4 StartY=19.1 StartZ=0 EndX=32.1 EndY=19.1 EndZ=0
    g4: LineSegment StartX=32.1 StartY=19.1 StartZ=0 EndX=32.1 EndY=28.4 EndZ=0
  constraints (14):
    c: Tangent(g0,g1) = 1.5708
    c: Tangent(g1,g2) = 1.5708
    c: Coincident(g2,g3)
    c: Horizontal(g3)
    c: Coincident(g3,g4)
    c: Vertical(g4)
    c: Horizontal(g0)
    c: Coincident(g0,g4)
    c: Vertical(g2)
    c: DistanceX(g0,g0) = 3.5
    c: Equal(g2,g0)
    c: DistanceY(g-1,g3) = 19.1
    c: DistanceX(g-1,g3) = 32.1
    c: DistanceY(g4,g4) = 9.3
FEATURE [PartDesign::Pocket] Pocket035  label="BottomMountCut"
  BaseFeature = -> Pocket020
  Length = 4.05
  Length2 = 100
  Profile = -> Sketch068
  Refine = true
  Type = 0
FEATURE [PartDesign::Mirrored] Mirrored014
  MirrorPlane = -> Sketch068 [V_Axis]
  Refine = true
FEATURE [PartDesign::Mirrored] Mirrored015
  MirrorPlane = -> Sketch068 [H_Axis]
  Refine = true
FEATURE [PartDesign::Chamfer] Chamfer
  Base = -> Pocket035 [Edge1]
  BaseFeature = -> Pocket035
  Size = 0.4
FEATURE [PartDesign::MultiTransform] MultiTransform007
  BaseFeature = -> Chamfer
  Originals = -> [Pocket035]
  Refine = true
  Transformations = -> [Mirrored014,Mirrored015]
FEATURE [Sketcher::SketchObject] Sketch069
  MapMode = 5
  Placement = pos=(0,0,-1) rot=(1,0,0;3.14159rad)
  Support = -> [MultiTransform007]
  sketch-geometry (4):
    g0: LineSegment StartX=-43.273 StartY=-38.05 StartZ=0 EndX=61.2686 EndY=0 EndZ=0
    g1: LineSegment StartX=61.2686 StartY=0 StartZ=0 EndX=61.2686 EndY=-1 EndZ=0
    g2: LineSegment StartX=61.2686 StartY=-1 StartZ=0 EndX=-40.5255 EndY=-38.05 EndZ=0
    g3: LineSegment StartX=-40.5255 StartY=-38.05 StartZ=0 EndX=-43.273 EndY=-38.05 EndZ=0
  constraints (10):
    c: Coincident(g0,g1)
    c: Vertical(g1)
    c: Coincident(g1,g2)
    c: Coincident(g2,g3)
    c: Coincident(g3,g0)
    c: Horizontal(g3)
    c: DistanceY(g1,g1) = 1
    c: Parallel(g0,g2)
    c: Horizontal(g0,g-1)
    c: Angle(g3,g2,g2) = 0.349066
FEATURE [PartDesign::Pocket] Pocket036
  BaseFeature = -> MultiTransform007
  Length = 0.6
  Length2 = 100
  Profile = -> Sketch069
  Refine = true
  Type = 0
FEATURE [PartDesign::LinearPattern] LinearPattern
  BaseFeature = -> Pocket036
  Direction = -> Sketch069 [H_Axis]
  Length = 20
  Occurrences = 4
  Originals = -> [Pocket036]
  Refine = true
FEATURE [PartDesign::Body] Body  label="Case_top"
  Group = -> [Sketch,Pad,Pocket,Sketch037,Sketch008,Pad001,MultiTransform,Sketch002,Sketch009,Mirrored001,Mirrored002,Mirrored003,Sketch011,Pocket003,Pocket001,Sketch013,Pocket005,Pocket019,Pad004,Sketch040,Pocket013,Sketch041,Pocket014,Sketch042,Pocket015,Sketch043,Pocket016,Pocket018,DatumPlane,Sketch045,Sketch046,DatumPlane001,Sketch047,Pocket020,DatumPlane002,Sketch068,Pocket035,Chamfer,MultiTransform007,+5 more]
  Origin = -> Origin041
  Placement = pos=(0,0,-6) rot=(0,0,1;0rad)
  Tip = -> LinearPattern
FEATURE [Part::Cut] Cut  label="FABI_Top"
  Base = -> Body
  Refine = true
  Tool = -> Extrude
FEATURE [Mesh::Feature] Mesh002  label="FABI_Bottom (Meshed)"
FEATURE [Mesh::Feature] Mesh003  label="FABI_Top (Meshed)001"
FEATURE [Mesh::Feature] Mesh004  label="FABI_Top (Meshed)002"
FEATURE [Mesh::Feature] Mesh005  label="Case_body (Meshed)"
FEATURE [Mesh::Feature] Mesh006  label="Chamfer001 (Meshed)"
note: 3 file-system paths scrubbed to <path> (originals preserved in the JSON sidecar)
